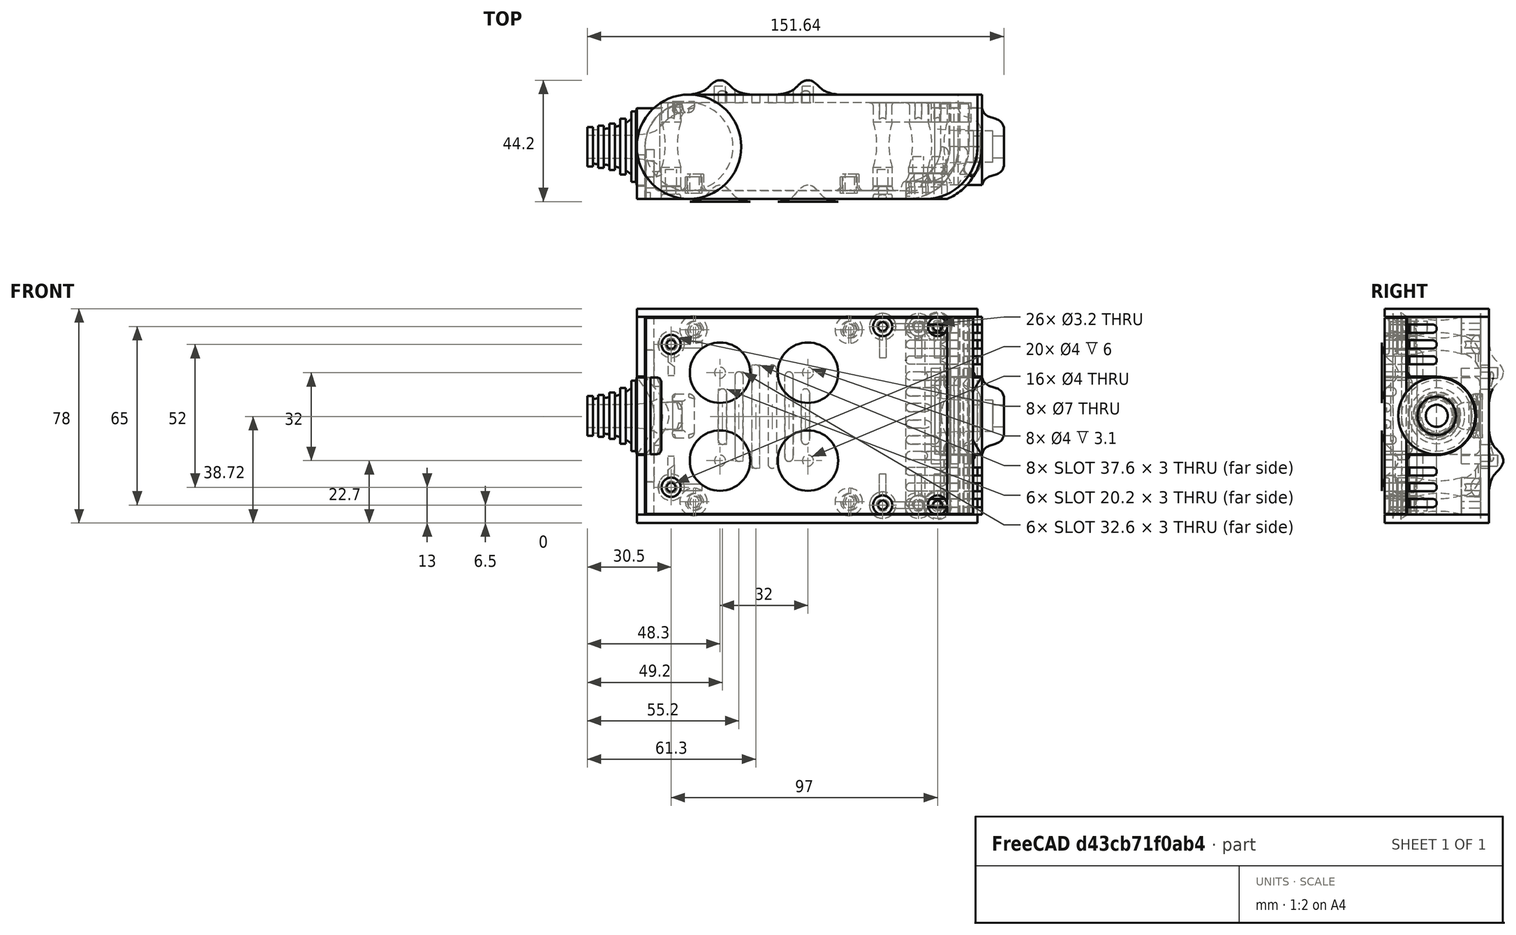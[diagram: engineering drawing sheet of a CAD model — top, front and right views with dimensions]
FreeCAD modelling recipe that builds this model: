
FCSTD DOCUMENT  (FreeCAD 0.19R0.19.2)
Label: enclosure_162
License: All rights reserved
LicenseURL: http://en.wikipedia.org/wiki/All_rights_reserved
objects: Part::Feature×140, Part::Revolution×140, Part::MultiFuse×121, Sketcher::SketchObject×67, Part::Extrusion×52, Part::Fillet×51, Part::Cut×51, Part::Cylinder×50, Part::Box×33, App::MeasureDistance×4
note: 705 computed .brp shape members not serialized (recipe doc carries the construction recipe); baked Part::Feature solids carry a one-line shape summary decoded from their .brp

FEATURE [Sketcher::SketchObject] Sketch  label="topSketch"
  FullyConstrained = true
  sketch-geometry (20):
    g0: LineSegment StartX=5.21097e-06 StartY=3 StartZ=0 EndX=5.21097e-06 EndY=19 EndZ=0
    g1: ArcOfCircle CenterX=19 CenterY=19 CenterZ=0 NormalX=0 NormalY=0 NormalZ=1 AngleXU=0 Radius=19 StartAngle=1.5708 EndAngle=3.14159
    g2: ArcOfCircle CenterX=19 CenterY=19 CenterZ=0 NormalX=0 NormalY=0 NormalZ=1 AngleXU=0 Radius=16 StartAngle=1.5708 EndAngle=3.14159
    g3: LineSegment StartX=114 StartY=35 StartZ=0 EndX=19 EndY=35 EndZ=0
    g4: LineSegment StartX=5.21097e-06 StartY=3 StartZ=0 EndX=5.21097e-06 EndY=0 EndZ=0
    g5: LineSegment StartX=3 StartY=0 StartZ=0 EndX=5.21097e-06 EndY=0 EndZ=0
    g6: LineSegment StartX=3 StartY=19 StartZ=0 EndX=3 EndY=0 EndZ=0
    g7: LineSegment StartX=19 StartY=38 StartZ=0 EndX=124 EndY=38 EndZ=0
    g8: Circle CenterX=119 CenterY=35 CenterZ=0 NormalX=0 NormalY=0 NormalZ=1 AngleXU=0 Radius=1
    g9: Circle CenterX=121 CenterY=35 CenterZ=0 NormalX=0 NormalY=0 NormalZ=1 AngleXU=0 Radius=1
    g10: Circle CenterX=121 CenterY=33 CenterZ=0 NormalX=0 NormalY=0 NormalZ=1 AngleXU=0 Radius=1
    g11: BSplineCurve PolesCount=3 KnotsCount=2 Degree=2 IsPeriodic=0
    g12: GeomPoint X=119 Y=35 Z=0
    g13: GeomPoint X=121 Y=33 Z=0
    g14: LineSegment StartX=119 StartY=35 StartZ=0 EndX=114 EndY=35 EndZ=0
    g15: ArcOfCircle CenterX=105 CenterY=19 CenterZ=0 NormalX=0 NormalY=0 NormalZ=1 AngleXU=0 Radius=19 StartAngle=5.7297 EndAngle=6.28319
    g16: ArcOfCircle CenterX=105 CenterY=19 CenterZ=0 NormalX=0 NormalY=0 NormalZ=1 AngleXU=0 Radius=16 StartAngle=5.60905 EndAngle=6.28319
    g17: LineSegment StartX=121 StartY=33 StartZ=0 EndX=121 EndY=19 EndZ=0
    g18: LineSegment StartX=124 StartY=38 StartZ=0 EndX=124 EndY=19 EndZ=0
    g19: LineSegment StartX=117.5 StartY=9.01251 StartZ=0 EndX=121.163 EndY=9.0125 EndZ=0
  constraints (46):
    c: Vertical(g0)
    c: Block(g0)
    c: Coincident(g1,g0)
    c: Block(g1)
    c: Coincident(g2,g1)
    c: Block(g2)
    c: Coincident(g3,g2)
    c: Horizontal(g3)
    c: Tangent(g3,g2)
    c: Coincident(g4,g0)
    c: Distance(g4) = 3
    c: Vertical(g4)
    c: Coincident(g5,g4)
    c: Horizontal(g5)
    c: Coincident(g6,g2)
    c: Coincident(g6,g5)
    c: Vertical(g6)
    c: Horizontal(g7)
    c: Distance(g7) = 105
    c: Coincident(g7,g1)
    c: Block(g3)
    c: Weight(g8) = 1
    c: Equal(g8,g9)
    c: Equal(g8,g10)
    c: InternalAlignment(g8,g11)
    c: InternalAlignment(g9,g11)
    c: InternalAlignment(g10,g11)
    c: InternalAlignment(g12,g11)
    c: InternalAlignment(g13,g11)
    c: Block(g11)
    c: Coincident(g14,g11)
    c: Coincident(g14,g3)
    c: Horizontal(g14)
    c: Block(g15)
    c: Coincident(g16,g15)
    c: Block(g16)
    c: Coincident(g17,g11)
    c: Coincident(g17,g16)
    c: Vertical(g17)
    c: Distance(g17) = 14
    c: Coincident(g18,g7)
    c: Coincident(g18,g15)
    c: Vertical(g18)
    c: Distance(g18) = 19
    c: Coincident(g19,g16)
    c: Coincident(g19,g15)
FEATURE [Sketcher::SketchObject] Sketch001  label="bottomSketch"
  FullyConstrained = true
  sketch-geometry (32):
    g0: LineSegment StartX=3.3 StartY=-6.03275e-07 StartZ=0 EndX=98 EndY=-6.03275e-07 EndZ=0
    g1: ArcOfCircle CenterX=98 CenterY=19 CenterZ=0 NormalX=0 NormalY=0 NormalZ=1 AngleXU=0 Radius=19 StartAngle=4.71239 EndAngle=5.71103
    g2: LineSegment StartX=6.3 StartY=8 StartZ=0 EndX=3.3 EndY=8 EndZ=0
    g3: LineSegment StartX=3.3 StartY=8 StartZ=0 EndX=3.3 EndY=-6.03275e-07 EndZ=0
    g4: ArcOfCircle CenterX=8.3 CenterY=5 CenterZ=0 NormalX=0 NormalY=0 NormalZ=1 AngleXU=0 Radius=2 StartAngle=3.14159 EndAngle=4.71239
    g5: LineSegment StartX=6.3 StartY=8 StartZ=0 EndX=6.3 EndY=5 EndZ=0
    g6: ArcOfCircle CenterX=98 CenterY=19 CenterZ=0 NormalX=0 NormalY=0 NormalZ=1 AngleXU=0 Radius=12.7 StartAngle=4.71239 EndAngle=6.28319
    g7: LineSegment StartX=94.7 StartY=3 StartZ=0 EndX=8.3 EndY=3 EndZ=0
    g8-g12: Circle x5 (B-spline internal-alignment scaffolding for g13; pole/knot coordinates omitted)
    g13: BSplineCurve PolesCount=5 KnotsCount=3 Degree=3 IsPeriodic=0
    g14: GeomPoint X=98 Y=6.3 Z=0
    g15: GeomPoint X=96.3938 Y=4.71946 Z=0
    g16: GeomPoint X=94.7 Y=3 Z=0
    g17-g23: Circle x7 (B-spline internal-alignment scaffolding for g24; pole/knot coordinates omitted)
    g24: BSplineCurve PolesCount=7 KnotsCount=5 Degree=3 IsPeriodic=0
    g25-g29: GeomPoint x5 (B-spline internal-alignment scaffolding for g24; pole/knot coordinates omitted)
    g30: ArcOfCircle CenterX=98 CenterY=19 CenterZ=0 NormalX=0 NormalY=0 NormalZ=1 AngleXU=0 Radius=15.7 StartAngle=5.81226 EndAngle=6.28319
    g31: LineSegment StartX=110.7 StartY=19 StartZ=0 EndX=113.7 EndY=19 EndZ=0
  constraints (41):
    c: Horizontal(g0)
    c: Coincident(g1,g0)
    c: Block(g1)
    c: Horizontal(g2)
    c: Distance(g2) = 3
    c: Coincident(g3,g2)
    c: Vertical(g3)
    c: Coincident(g3,g0)
    c: Block(g4)
    c: Block(g2)
    c: Coincident(g5,g2)
    c: Coincident(g5,g4)
    c: Vertical(g5)
    c: Coincident(g6,g1)
    c: Block(g6)
    c: Coincident(g7,g4)
    c: Horizontal(g7)
    c: Block(g0)
    c: Block(g7)
    c: Block(g3)
    c: Coincident(g13,g6)
    c: Weight(g8) = 1
    c: Equal(g8, g9-g12) x4
    c: Coincident(g13,g7)
    c: InternalAlignment(g8-g12 -> g13) x5
    c: InternalAlignment(g14,g13)
    c: InternalAlignment(g15,g13)
    c: InternalAlignment(g16,g13)
    c: Block(g13)
    c: Weight(g17) = 1
    c: Equal(g17, g18-g23) x6
    c: Coincident(g24,g1)
    c: InternalAlignment(g17-g23 -> g24) x7
    c: InternalAlignment(g25-g29 -> g24) x5
    c: Block(g24)
    c: Coincident(g30,g24)
    c: Coincident(g31,g6)
    c: Coincident(g31,g30)
    c: Horizontal(g31)
    c: Block(g31)
    c: Block(g30)
FEATURE [Part::Extrusion] Extrude  label="top"
  Base = -> Sketch
  Dir = (0,0,1)
  DirMode = 2
  FaceMakerClass = Part::FaceMakerBullseye
  LengthFwd = 72
  LengthRev = 0
  Solid = true
  Symmetric = false
FEATURE [Part::Extrusion] Extrude001  label="bottom"
  Base = -> Sketch001
  Dir = (0,0,1)
  DirMode = 2
  FaceMakerClass = Part::FaceMakerBullseye
  LengthFwd = 71.4
  LengthRev = 0
  Placement = pos=(0,0,0.3) rot=(0,0,1;0rad)
  Solid = true
  Symmetric = false
FEATURE [Sketcher::SketchObject] Sketch002  label="topSketch001"
  FullyConstrained = true
  sketch-geometry (6):
    g0: ArcOfCircle CenterX=19 CenterY=19 CenterZ=0 NormalX=0 NormalY=0 NormalZ=1 AngleXU=0 Radius=19 StartAngle=1.5708 EndAngle=3.14159
    g1: LineSegment StartX=5.22862e-06 StartY=19 StartZ=0 EndX=5.22862e-06 EndY=1.19904e-11 EndZ=0
    g2: LineSegment StartX=19 StartY=38 StartZ=0 EndX=124 EndY=38 EndZ=0
    g3: LineSegment StartX=5.22862e-06 StartY=1.19904e-11 StartZ=0 EndX=105 EndY=1.19904e-11 EndZ=0
    g4: ArcOfCircle CenterX=105 CenterY=19 CenterZ=0 NormalX=0 NormalY=0 NormalZ=1 AngleXU=0 Radius=19 StartAngle=4.71239 EndAngle=6.28319
    g5: LineSegment StartX=124 StartY=38 StartZ=0 EndX=124 EndY=19 EndZ=0
  constraints (16):
    c: Block(g0)
    c: Coincident(g1,g0)
    c: Vertical(g1)
    c: Horizontal(g2)
    c: Distance(g2) = 105
    c: Coincident(g2,g0)
    c: Distance(g1) = 19
    c: Coincident(g3,g1)
    c: Horizontal(g3)
    c: Distance(g3) = 105
    c: Block(g4)
    c: Coincident(g4,g3)
    c: Coincident(g5,g2)
    c: Coincident(g5,g4)
    c: Vertical(g5)
    c: Distance(g5) = 19
FEATURE [Part::Extrusion] Extrude002  label="sideA"
  Base = -> Sketch002
  Dir = (0,0,1)
  DirMode = 2
  FaceMakerClass = Part::FaceMakerBullseye
  LengthFwd = 3
  LengthRev = 0
  Placement = pos=(0,0,-3) rot=(0,0,1;0rad)
  Solid = true
  Symmetric = false
FEATURE [Sketcher::SketchObject] Sketch003  label="topSketch002"
  FullyConstrained = true
  sketch-geometry (6):
    g0: LineSegment StartX=19 StartY=38 StartZ=0 EndX=117 EndY=38 EndZ=0
    g1: ArcOfCircle CenterX=19 CenterY=19 CenterZ=0 NormalX=0 NormalY=0 NormalZ=1 AngleXU=0 Radius=19 StartAngle=1.5708 EndAngle=3.14159
    g2: LineSegment StartX=117 StartY=38 StartZ=0 EndX=117 EndY=19 EndZ=0
    g3: LineSegment StartX=98 StartY=1.0161e-12 StartZ=0 EndX=5.22862e-06 EndY=1.0161e-12 EndZ=0
    g4: LineSegment StartX=5.22862e-06 StartY=19 StartZ=0 EndX=5.22862e-06 EndY=1.0161e-12 EndZ=0
    g5: ArcOfCircle CenterX=98 CenterY=19 CenterZ=0 NormalX=0 NormalY=0 NormalZ=1 AngleXU=0 Radius=19 StartAngle=4.71239 EndAngle=6.28319
  constraints (16):
    c: Horizontal(g0)
    c: Distance(g0) = 98
    c: Coincident(g1,g0)
    c: Block(g1)
    c: Coincident(g2,g0)
    c: Vertical(g2)
    c: Distance(g2) = 19
    c: Horizontal(g3)
    c: Coincident(g4,g1)
    c: Vertical(g4)
    c: Coincident(g3,g4)
    c: Block(g3)
    c: Coincident(g5,g2)
    c: Coincident(g5,g3)
    c: Block(g0)
    c: Block(g5)
FEATURE [Sketcher::SketchObject] Sketch004
  FullyConstrained = true
  MapMode = 3
  Placement = pos=(0,0,0) rot=(1,0,0;1.5708rad)
  Support = -> [Extrude]
  sketch-geometry (8):
    g0: Circle CenterX=80.351 CenterY=-67.6202 CenterZ=0 NormalX=0 NormalY=0 NormalZ=1 AngleXU=0 Radius=2
    g1: Circle CenterX=80.351 CenterY=-67.6202 CenterZ=0 NormalX=0 NormalY=0 NormalZ=1 AngleXU=0 Radius=3
    g2: Circle CenterX=80.351 CenterY=-4.92017 CenterZ=0 NormalX=0 NormalY=0 NormalZ=1 AngleXU=0 Radius=2
    g3: Circle CenterX=80.351 CenterY=-4.92017 CenterZ=0 NormalX=0 NormalY=0 NormalZ=1 AngleXU=0 Radius=3
    g4: Circle CenterX=23.851 CenterY=-4.92017 CenterZ=0 NormalX=0 NormalY=0 NormalZ=1 AngleXU=0 Radius=2
    g5: Circle CenterX=23.851 CenterY=-4.92017 CenterZ=0 NormalX=0 NormalY=0 NormalZ=1 AngleXU=0 Radius=3
    g6: Circle CenterX=23.851 CenterY=-67.6202 CenterZ=0 NormalX=0 NormalY=0 NormalZ=1 AngleXU=0 Radius=2
    g7: Circle CenterX=23.851 CenterY=-67.6202 CenterZ=0 NormalX=0 NormalY=0 NormalZ=1 AngleXU=0 Radius=3
  constraints (8):
    c: Block(g3)
    c: Block(g2)
    c: Block(g1)
    c: Block(g0)
    c: Block(g6)
    c: Block(g7)
    c: Block(g4)
    c: Block(g5)
FEATURE [Part::Extrusion] Extrude004
  Base = -> Sketch004
  Dir = (0,-1,2e-16)
  DirMode = 2
  FaceMakerClass = Part::FaceMakerBullseye
  LengthFwd = 6
  LengthRev = 0
  Placement = pos=(0,9,0) rot=(0,0,1;0rad)
  Solid = true
  Symmetric = false
FEATURE [Sketcher::SketchObject] Sketch005
  FullyConstrained = true
  MapMode = 3
  Placement = pos=(0,0,0) rot=(1,0,0;1.5708rad)
  Support = -> [Extrude]
  sketch-geometry (8):
    g0: Circle CenterX=80.351 CenterY=-67.6202 CenterZ=0 NormalX=0 NormalY=0 NormalZ=1 AngleXU=0 Radius=3
    g1: Circle CenterX=80.351 CenterY=-4.92017 CenterZ=0 NormalX=0 NormalY=0 NormalZ=1 AngleXU=0 Radius=3
    g2: Circle CenterX=23.851 CenterY=-4.92017 CenterZ=0 NormalX=0 NormalY=0 NormalZ=1 AngleXU=0 Radius=3
    g3: Circle CenterX=23.851 CenterY=-67.6202 CenterZ=0 NormalX=0 NormalY=0 NormalZ=1 AngleXU=0 Radius=3
    g4: Circle CenterX=23.851 CenterY=-67.6202 CenterZ=0 NormalX=0 NormalY=0 NormalZ=1 AngleXU=0 Radius=5
    g5: Circle CenterX=80.351 CenterY=-67.6202 CenterZ=0 NormalX=0 NormalY=0 NormalZ=1 AngleXU=0 Radius=5
    g6: Circle CenterX=23.851 CenterY=-4.92017 CenterZ=0 NormalX=0 NormalY=0 NormalZ=1 AngleXU=0 Radius=5
    g7: Circle CenterX=80.351 CenterY=-4.92017 CenterZ=0 NormalX=0 NormalY=0 NormalZ=1 AngleXU=0 Radius=5
  constraints (8):
    c: Block(g1)
    c: Block(g0)
    c: Block(g3)
    c: Block(g2)
    c: Block(g5)
    c: Block(g4)
    c: Block(g6)
    c: Block(g7)
FEATURE [Part::Extrusion] Extrude005
  Base = -> Sketch005
  Dir = (0,-1,2e-16)
  DirMode = 2
  FaceMakerClass = Part::FaceMakerBullseye
  LengthFwd = 2
  LengthRev = 0
  Solid = true
  Symmetric = false
FEATURE [Sketcher::SketchObject] Sketch006
  FullyConstrained = true
  MapMode = 3
  Placement = pos=(0,0,0) rot=(1,0,0;1.5708rad)
  sketch-geometry (8):
    g0: Circle CenterX=80.351 CenterY=-67.6202 CenterZ=0 NormalX=0 NormalY=0 NormalZ=1 AngleXU=0 Radius=3
    g1: Circle CenterX=80.351 CenterY=-4.92017 CenterZ=0 NormalX=0 NormalY=0 NormalZ=1 AngleXU=0 Radius=3
    g2: Circle CenterX=23.851 CenterY=-4.92017 CenterZ=0 NormalX=0 NormalY=0 NormalZ=1 AngleXU=0 Radius=3
    g3: Circle CenterX=23.851 CenterY=-67.6202 CenterZ=0 NormalX=0 NormalY=0 NormalZ=1 AngleXU=0 Radius=3
    g4: Circle CenterX=23.851 CenterY=-67.6202 CenterZ=0 NormalX=0 NormalY=0 NormalZ=1 AngleXU=0 Radius=5
    g5: Circle CenterX=80.351 CenterY=-67.6202 CenterZ=0 NormalX=0 NormalY=0 NormalZ=1 AngleXU=0 Radius=5
    g6: Circle CenterX=23.851 CenterY=-4.92017 CenterZ=0 NormalX=0 NormalY=0 NormalZ=1 AngleXU=0 Radius=5
    g7: Circle CenterX=80.351 CenterY=-4.92017 CenterZ=0 NormalX=0 NormalY=0 NormalZ=1 AngleXU=0 Radius=5
  constraints (8):
    c: Block(g1)
    c: Block(g0)
    c: Block(g3)
    c: Block(g2)
    c: Block(g5)
    c: Block(g4)
    c: Block(g6)
    c: Block(g7)
FEATURE [Part::Extrusion] Extrude007
  Base = -> Sketch006
  Dir = (0,-1,2e-16)
  DirMode = 2
  FaceMakerClass = Part::FaceMakerBullseye
  LengthFwd = 2
  LengthRev = 0
  Solid = true
  Symmetric = false
FEATURE [Part::Fillet] Fillet
  Base = -> Extrude007
  Edges = 4 edges r=1.99: [Edge6,Edge12,Edge18,Edge24]
FEATURE [Part::Cut] Cut
  Base = -> Extrude005
  Placement = pos=(0,5,0) rot=(0,0,1;0rad)
  Tool = -> Fillet
FEATURE [Part::MultiFuse] Fusion  label="pCBScrews"
  Placement = pos=(-2.5,0,72.3) rot=(0,0,1;0rad)
  Shapes = -> [Extrude004,Cut]
FEATURE [App::MeasureDistance] Distance  label="Distance: 0.69 mm"
  Distance = 0.685967
  P1 = (24.0138,2.9647,0.3)
  P2 = (23.8901,3,-0.373787)
FEATURE [App::MeasureDistance] Distance001  label="Distance: 0.53 mm"
  Distance = 0.533607
  P1 = (80.2939,3,72.2334)
  P2 = (80.281,2.99661,71.7)
FEATURE [Part::Fillet] Fillet001
  Base = -> Extrude001
  Edges = 1 edges r=2.4: [Edge17]
FEATURE [Part::Fillet] Fillet002  label="bottom001"
  Base = -> Fillet001
  Edges = 1 edges r=2.4: [Edge36]
FEATURE [Part::Fillet] Fillet003  label="top001"
  Base = -> Extrude
  Edges = 1 edges r=2: [Edge1]
FEATURE [Sketcher::SketchObject] Sketch007
  FullyConstrained = true
  sketch-geometry (16):
    g0: LineSegment StartX=4 StartY=0 StartZ=0 EndX=4 EndY=2.4 EndZ=0
    g1: LineSegment StartX=4 StartY=2.4 StartZ=0 EndX=7 EndY=2.4 EndZ=0
    g2: LineSegment StartX=4 StartY=0 StartZ=0 EndX=5.7 EndY=0 EndZ=0
    g3: LineSegment StartX=5.7 StartY=0 StartZ=0 EndX=5.7 EndY=-5.6 EndZ=0
    g4-g8: Circle x5 (B-spline internal-alignment scaffolding for g9; pole/knot coordinates omitted)
    g9: BSplineCurve PolesCount=5 KnotsCount=3 Degree=3 IsPeriodic=0
    g10: GeomPoint X=7 Y=2.4 Z=0
    g11: GeomPoint X=10.4582 Y=-1.55472 Z=0
    g12: GeomPoint X=14 Y=-5.6 Z=0
    g13: LineSegment StartX=14 StartY=-5.6 StartZ=0 EndX=14 EndY=-14.1 EndZ=0
    g14: LineSegment StartX=14 StartY=-14.1 StartZ=0 EndX=6.5 EndY=-14.1 EndZ=0
    g15: LineSegment StartX=5.7 StartY=-5.6 StartZ=0 EndX=6.5 EndY=-14.1 EndZ=0
  constraints (28):
    c: Distance(g0) = 2.4
    c: Vertical(g0)
    c: Block(g0)
    c: Coincident(g1,g0)
    c: Horizontal(g1)
    c: Distance(g1) = 3
    c: Coincident(g2,g0)
    c: Horizontal(g2)
    c: Distance(g2) = 1.7
    c: Coincident(g3,g2)
    c: Vertical(g3)
    c: Distance(g3) = 5.6
    c: Coincident(g9,g1)
    c: Weight(g4) = 1
    c: Equal(g4, g5-g8) x4
    c: InternalAlignment(g4-g8 -> g9) x5
    c: InternalAlignment(g10,g9)
    c: InternalAlignment(g11,g9)
    c: InternalAlignment(g12,g9)
    c: Block(g9)
    c: Coincident(g13,g9)
    c: Vertical(g13)
    c: Distance(g13) = 8.5
    c: Coincident(g14,g13)
    c: Horizontal(g14)
    c: Distance(g14) = 7.5
    c: Coincident(g15,g3)
    c: Coincident(g15,g14)
FEATURE [Part::Feature] Face
  shape: bbox 10 x 16.5 x 2e-07 mm, 1 faces, 0 solids (baked)
FEATURE [Part::Revolution] Revolve  label="plugHousing"
  Angle = 360
  Axis = (0,1,0)
  Base = (0,0,0)
  FaceMakerClass = Part::FaceMakerBullseye
  Placement = pos=(0,0,36.15) rot=(0,0,1;0rad)
  Solid = false
  Source = -> Face
  Symmetric = false
FEATURE [Part::Feature] Face001
  shape: bbox 10 x 16.5 x 2e-07 mm, 1 faces, 0 solids (baked)
FEATURE [Part::Revolution] Revolve001  label="plugHousing001"
  Angle = 360
  Axis = (0,1,0)
  Base = (0,0,0)
  FaceMakerClass = Part::FaceMakerBullseye
  Placement = pos=(0,0,36.15) rot=(0,0,1;0rad)
  Solid = false
  Source = -> Face001
  Symmetric = false
FEATURE [Part::MultiFuse] Fusion001  label="plugHousing002"
  Placement = pos=(0,0,0) rot=(0,0,1;1.5708rad)
  Shapes = -> [Revolve001,Revolve]
FEATURE [Part::Feature] Face002
  shape: bbox 10 x 16.5 x 2e-07 mm, 1 faces, 0 solids (baked)
FEATURE [Part::Revolution] Revolve003  label="plugHousing005"
  Angle = 360
  Axis = (0,1,0)
  Base = (0,0,0)
  FaceMakerClass = Part::FaceMakerBullseye
  Placement = pos=(0,0,36.15) rot=(0,0,1;0rad)
  Solid = false
  Source = -> Face002
  Symmetric = false
FEATURE [Part::Feature] Face003
  shape: bbox 10 x 16.5 x 2e-07 mm, 1 faces, 0 solids (baked)
FEATURE [Part::Revolution] Revolve002  label="plugHousing003"
  Angle = 360
  Axis = (0,1,0)
  Base = (0,0,0)
  FaceMakerClass = Part::FaceMakerBullseye
  Placement = pos=(0,0,36.15) rot=(0,0,1;0rad)
  Solid = false
  Source = -> Face003
  Symmetric = false
FEATURE [Part::MultiFuse] Fusion002  label="plugHousing004"
  Placement = pos=(0,0,0) rot=(0,0,1;1.5708rad)
  Shapes = -> [Revolve002,Revolve003]
FEATURE [Part::MultiFuse] Fusion003  label="plugHousing006"
  Placement = pos=(0,19,0) rot=(0,0,1;3.14159rad)
  Shapes = -> [Fusion002,Fusion001]
FEATURE [Part::Feature] Face004
  shape: bbox 10 x 16.5 x 2e-07 mm, 1 faces, 0 solids (baked)
FEATURE [Part::Revolution] Revolve006  label="plugHousing010"
  Angle = 360
  Axis = (0,1,0)
  Base = (0,0,0)
  FaceMakerClass = Part::FaceMakerBullseye
  Placement = pos=(0,0,36.15) rot=(0,0,1;0rad)
  Solid = false
  Source = -> Face004
  Symmetric = false
FEATURE [Part::Feature] Face005
  shape: bbox 10 x 16.5 x 2e-07 mm, 1 faces, 0 solids (baked)
FEATURE [Part::Revolution] Revolve007  label="plugHousing011"
  Angle = 360
  Axis = (0,1,0)
  Base = (0,0,0)
  FaceMakerClass = Part::FaceMakerBullseye
  Placement = pos=(0,0,36.15) rot=(0,0,1;0rad)
  Solid = false
  Source = -> Face005
  Symmetric = false
FEATURE [Part::Feature] Face006
  shape: bbox 10 x 16.5 x 2e-07 mm, 1 faces, 0 solids (baked)
FEATURE [Part::Revolution] Revolve004  label="plugHousing007"
  Angle = 360
  Axis = (0,1,0)
  Base = (0,0,0)
  FaceMakerClass = Part::FaceMakerBullseye
  Placement = pos=(0,0,36.15) rot=(0,0,1;0rad)
  Solid = false
  Source = -> Face006
  Symmetric = false
FEATURE [Part::MultiFuse] Fusion004  label="plugHousing009"
  Placement = pos=(0,0,0) rot=(0,0,1;1.5708rad)
  Shapes = -> [Revolve004,Revolve007]
FEATURE [Part::Feature] Face007
  shape: bbox 10 x 16.5 x 2e-07 mm, 1 faces, 0 solids (baked)
FEATURE [Part::Revolution] Revolve005  label="plugHousing008"
  Angle = 360
  Axis = (0,1,0)
  Base = (0,0,0)
  FaceMakerClass = Part::FaceMakerBullseye
  Placement = pos=(0,0,36.15) rot=(0,0,1;0rad)
  Solid = false
  Source = -> Face007
  Symmetric = false
FEATURE [Part::MultiFuse] Fusion005  label="plugHousing012"
  Placement = pos=(0,0,0) rot=(0,0,1;1.5708rad)
  Shapes = -> [Revolve006,Revolve005]
FEATURE [Part::MultiFuse] Fusion006  label="plugHousing013"
  Placement = pos=(0,19,0) rot=(0,0,1;3.14159rad)
  Shapes = -> [Fusion005,Fusion004]
FEATURE [Part::MultiFuse] Fusion007  label="plugHousing014"
  Placement = pos=(122.621,0,-0.15) rot=(0,0,1;0rad)
  Shapes = -> [Fusion003,Fusion006]
FEATURE [Part::Cylinder] Cylinder002
  Angle = 360
  AttacherType = Attacher::AttachEngine3D
  Height = 20
  Placement = pos=(0,0,36.15) rot=(0,0,1;0rad)
  Radius = 4
FEATURE [Part::Cylinder] Cylinder003
  Angle = 360
  AttacherType = Attacher::AttachEngine3D
  Height = 10
  Placement = pos=(0,0,36.15) rot=(0,0,1;0rad)
  Radius = 4
FEATURE [Part::MultiFuse] Fusion009  label="removeToCreateHoleForPlugHousing"
  Placement = pos=(70,19,36.15) rot=(0,1,0;1.5708rad)
  Shapes = -> [Cylinder002,Cylinder003]
FEATURE [Part::Cylinder] Cylinder004
  Angle = 360
  AttacherType = Attacher::AttachEngine3D
  Height = 20
  Placement = pos=(0,0,36.15) rot=(0,0,1;0rad)
  Radius = 4
FEATURE [Part::Cylinder] Cylinder005
  Angle = 360
  AttacherType = Attacher::AttachEngine3D
  Height = 10
  Placement = pos=(0,0,36.15) rot=(0,0,1;0rad)
  Radius = 4
FEATURE [Part::MultiFuse] Fusion010  label="removeToCreateHoleForPlugHousing001"
  Placement = pos=(70,19,36.15) rot=(0,1,0;1.5708rad)
  Shapes = -> [Cylinder004,Cylinder005]
FEATURE [Part::Cut] Cut001
  Base = -> Fillet003
  Tool = -> Fusion010
FEATURE [Part::Cut] Cut002  label="Bottom"
  Base = -> Fillet002
  Tool = -> Fusion009
FEATURE [Part::Feature] Face008
  shape: bbox 10 x 16.5 x 2e-07 mm, 1 faces, 0 solids (baked)
FEATURE [Part::Revolution] Revolve011  label="plugHousing021"
  Angle = 360
  Axis = (0,1,0)
  Base = (0,0,0)
  FaceMakerClass = Part::FaceMakerBullseye
  Placement = pos=(0,0,36.15) rot=(0,0,1;0rad)
  Solid = false
  Source = -> Face008
  Symmetric = false
FEATURE [Part::Feature] Face009
  shape: bbox 10 x 16.5 x 2e-07 mm, 1 faces, 0 solids (baked)
FEATURE [Part::Revolution] Revolve012  label="plugHousing022"
  Angle = 360
  Axis = (0,1,0)
  Base = (0,0,0)
  FaceMakerClass = Part::FaceMakerBullseye
  Placement = pos=(0,0,36.15) rot=(0,0,1;0rad)
  Solid = false
  Source = -> Face009
  Symmetric = false
FEATURE [Part::Feature] Face010 .. Face013  x4 (patterned run collapsed; names and placements below)
  shape: bbox 10 x 16.5 x 2e-07 mm, 1 faces, 0 solids (baked)
FEATURE [Part::Revolution] Revolve015  label="plugHousing027"
  Angle = 360
  Axis = (0,1,0)
  Base = (0,0,0)
  FaceMakerClass = Part::FaceMakerBullseye
  Placement = pos=(0,0,36.15) rot=(0,0,1;0rad)
  Solid = false
  Source = -> Face013
  Symmetric = false
FEATURE [Part::Feature] Face014
  shape: bbox 10 x 16.5 x 2e-07 mm, 1 faces, 0 solids (baked)
FEATURE [Part::Feature] Face015
  shape: bbox 10 x 16.5 x 2e-07 mm, 1 faces, 0 solids (baked)
FEATURE [Part::Feature] Face016
  shape: bbox 10 x 16.5 x 2e-07 mm, 1 faces, 0 solids (baked)
FEATURE [Part::Revolution] Revolve019  label="plugHousing033"
  Angle = 360
  Axis = (0,1,0)
  Base = (0,0,0)
  FaceMakerClass = Part::FaceMakerBullseye
  Placement = pos=(0,0,36.15) rot=(0,0,1;0rad)
  Solid = false
  Source = -> Face016
  Symmetric = false
FEATURE [Part::Feature] Face017
  shape: bbox 10 x 16.5 x 2e-07 mm, 1 faces, 0 solids (baked)
FEATURE [Part::Revolution] Revolve020  label="plugHousing034"
  Angle = 360
  Axis = (0,1,0)
  Base = (0,0,0)
  FaceMakerClass = Part::FaceMakerBullseye
  Placement = pos=(0,0,36.15) rot=(0,0,1;0rad)
  Solid = false
  Source = -> Face017
  Symmetric = false
FEATURE [Part::Feature] Face018
  shape: bbox 10 x 16.5 x 2e-07 mm, 1 faces, 0 solids (baked)
FEATURE [Part::Revolution] Revolve016  label="plugHousing030"
  Angle = 360
  Axis = (0,1,0)
  Base = (0,0,0)
  FaceMakerClass = Part::FaceMakerBullseye
  Placement = pos=(0,0,36.15) rot=(0,0,1;0rad)
  Solid = false
  Source = -> Face018
  Symmetric = false
FEATURE [Part::MultiFuse] Fusion020  label="plugHousing038"
  Placement = pos=(0,0,0) rot=(0,0,1;1.5708rad)
  Shapes = -> [Revolve016,Revolve020]
FEATURE [Part::Feature] Face019
  shape: bbox 10 x 16.5 x 2e-07 mm, 1 faces, 0 solids (baked)
FEATURE [Part::Feature] Face020
  shape: bbox 10 x 16.5 x 2e-07 mm, 1 faces, 0 solids (baked)
FEATURE [Part::Revolution] Revolve017  label="plugHousing031"
  Angle = 360
  Axis = (0,1,0)
  Base = (0,0,0)
  FaceMakerClass = Part::FaceMakerBullseye
  Placement = pos=(0,0,36.15) rot=(0,0,1;0rad)
  Solid = false
  Source = -> Face020
  Symmetric = false
FEATURE [Part::MultiFuse] Fusion021  label="plugHousing039"
  Placement = pos=(0,0,0) rot=(0,0,1;1.5708rad)
  Shapes = -> [Revolve019,Revolve017]
FEATURE [Part::MultiFuse] Fusion023  label="plugHousing041"
  Placement = pos=(0,19,0) rot=(0,0,1;3.14159rad)
  Shapes = -> [Fusion021,Fusion020]
FEATURE [Part::Revolution] Revolve022  label="plugHousing043"
  Angle = 360
  Axis = (0,1,0)
  Base = (0,0,0)
  FaceMakerClass = Part::FaceMakerBullseye
  Placement = pos=(0,0,36.15) rot=(0,0,1;0rad)
  Solid = false
  Source = -> Face019
  Symmetric = false
FEATURE [Part::Feature] Face021
  shape: bbox 10 x 16.5 x 2e-07 mm, 1 faces, 0 solids (baked)
FEATURE [Part::Revolution] Revolve023  label="plugHousing044"
  Angle = 360
  Axis = (0,1,0)
  Base = (0,0,0)
  FaceMakerClass = Part::FaceMakerBullseye
  Placement = pos=(0,0,36.15) rot=(0,0,1;0rad)
  Solid = false
  Source = -> Face021
  Symmetric = false
FEATURE [Part::Feature] Face022
  shape: bbox 10 x 16.5 x 2e-07 mm, 1 faces, 0 solids (baked)
FEATURE [Part::Revolution] Revolve018  label="plugHousing032"
  Angle = 360
  Axis = (0,1,0)
  Base = (0,0,0)
  FaceMakerClass = Part::FaceMakerBullseye
  Placement = pos=(0,0,36.15) rot=(0,0,1;0rad)
  Solid = false
  Source = -> Face022
  Symmetric = false
FEATURE [Part::MultiFuse] Fusion022  label="plugHousing040"
  Placement = pos=(0,0,0) rot=(0,0,1;1.5708rad)
  Shapes = -> [Revolve018,Revolve023]
FEATURE [Part::Feature] Face023
  shape: bbox 10 x 16.5 x 2e-07 mm, 1 faces, 0 solids (baked)
FEATURE [Part::Revolution] Revolve021  label="plugHousing035"
  Angle = 360
  Axis = (0,1,0)
  Base = (0,0,0)
  FaceMakerClass = Part::FaceMakerBullseye
  Placement = pos=(0,0,36.15) rot=(0,0,1;0rad)
  Solid = false
  Source = -> Face023
  Symmetric = false
FEATURE [Part::MultiFuse] Fusion018  label="plugHousing036"
  Placement = pos=(0,0,0) rot=(0,0,1;1.5708rad)
  Shapes = -> [Revolve022,Revolve021]
FEATURE [Part::MultiFuse] Fusion019  label="plugHousing037"
  Placement = pos=(0,19,0) rot=(0,0,1;3.14159rad)
  Shapes = -> [Fusion018,Fusion022]
FEATURE [Part::MultiFuse] Fusion024  label="plugHousing042"
  Placement = pos=(122.621,0,-0.15) rot=(0,0,1;0rad)
  Shapes = -> [Fusion023,Fusion019]
FEATURE [Part::Cylinder] Cylinder006
  Angle = 360
  AttacherType = Attacher::AttachEngine3D
  Height = 20
  Placement = pos=(0,0,36.15) rot=(0,0,1;0rad)
  Radius = 14.3
FEATURE [Part::Cylinder] Cylinder007
  Angle = 360
  AttacherType = Attacher::AttachEngine3D
  Height = 10
  Placement = pos=(0,0,36.15) rot=(0,0,1;0rad)
  Radius = 4
FEATURE [Part::MultiFuse] Fusion026  label="removeToCreteHoleForPlugHousing"
  Placement = pos=(70,19,36) rot=(0,1,0;1.5708rad)
  Shapes = -> [Cylinder006,Cylinder007]
FEATURE [Part::Box] Box001  label="Cube001"
  AttacherType = Attacher::AttachEngine3D
  Height = 28
  Length = 3
  Placement = pos=(110.7,19,22) rot=(0,0,1;0rad)
  Width = 15.7
FEATURE [Part::Cut] Cut003  label="top002"
  Base = -> Cut001
  Tool = -> Fusion007
FEATURE [Part::Revolution] Revolve008  label="plugHousing015"
  Angle = 360
  Axis = (0,1,0)
  Base = (0,0,0)
  FaceMakerClass = Part::FaceMakerBullseye
  Placement = pos=(0,0,36.15) rot=(0,0,1;0rad)
  Solid = false
  Source = -> Face010
  Symmetric = false
FEATURE [Part::MultiFuse] Fusion013  label="plugHousing020"
  Placement = pos=(0,0,0) rot=(0,0,1;1.5708rad)
  Shapes = -> [Revolve008,Revolve012]
FEATURE [Part::Cut] Cut004  label="top003"
  Base = -> Cut003
  Placement = pos=(1,0,0) rot=(0,0,1;0rad)
  Tool = -> Fusion026
FEATURE [Part::Cylinder] Cylinder008
  Angle = 360
  AttacherType = Attacher::AttachEngine3D
  Height = 20
  Placement = pos=(0,0,36.15) rot=(0,0,1;0rad)
  Radius = 10.3
FEATURE [Part::Cylinder] Cylinder009
  Angle = 360
  AttacherType = Attacher::AttachEngine3D
  Height = 10
  Placement = pos=(0,0,36.15) rot=(0,0,1;0rad)
  Radius = 4
FEATURE [Part::MultiFuse] Fusion027  label="removeToCreteHoleForPlugHousing001"
  Placement = pos=(70,19,36) rot=(0,1,0;1.5708rad)
  Shapes = -> [Cylinder008,Cylinder009]
FEATURE [Part::Cut] Cut005  label="plugHousingTab"
  Base = -> Box001
  Tool = -> Fusion027
FEATURE [Part::MultiFuse] Fusion028  label="plugHousing045"
  Shapes = -> [Fusion024,Cut005]
FEATURE [Part::Box] Box002  label="Cube002"
  AttacherType = Attacher::AttachEngine3D
  Height = 28.8
  Length = 3
  Placement = pos=(107.3,28,21.6) rot=(0,0,1;0rad)
  Width = 7
FEATURE [Part::Box] Box003  label="Cube003"
  AttacherType = Attacher::AttachEngine3D
  Height = 3
  Length = 6.4
  Placement = pos=(107.3,28,18.6) rot=(0,0,1;0rad)
  Width = 7
FEATURE [Part::Box] Box004  label="Cube004"
  AttacherType = Attacher::AttachEngine3D
  Height = 3
  Length = 6.4
  Placement = pos=(107.3,28,50.4) rot=(0,0,1;0rad)
  Width = 7
FEATURE [Part::MultiFuse] Fusion029  label="plugHousingBracketHolder"
  Shapes = -> [Box004,Box002,Box003]
FEATURE [Part::Cylinder] Cylinder010
  Angle = 360
  AttacherType = Attacher::AttachEngine3D
  Height = 20
  Placement = pos=(0,0,36.15) rot=(0,0,1;0rad)
  Radius = 14.3
FEATURE [Part::Cylinder] Cylinder011
  Angle = 360
  AttacherType = Attacher::AttachEngine3D
  Height = 10
  Placement = pos=(0,0,36.15) rot=(0,0,1;0rad)
  Radius = 4
FEATURE [Part::MultiFuse] Fusion030  label="removeToCreteHoleForPlugHousing002"
  Placement = pos=(70,19,36) rot=(0,1,0;1.5708rad)
  Shapes = -> [Cylinder010,Cylinder011]
FEATURE [Part::Cut] Cut006  label="plugHousingBracketHolder001"
  Base = -> Fusion029
  Tool = -> Fusion030
FEATURE [Part::Cylinder] Cylinder012
  Angle = 360
  AttacherType = Attacher::AttachEngine3D
  Height = 20
  Placement = pos=(0,0,36.15) rot=(0,0,1;0rad)
  Radius = 7
FEATURE [Part::Cylinder] Cylinder013
  Angle = 360
  AttacherType = Attacher::AttachEngine3D
  Height = 10
  Placement = pos=(0,0,36.15) rot=(0,0,1;0rad)
  Radius = 4
FEATURE [Part::MultiFuse] Fusion032  label="removeToCreteHoleForPlugHousing003"
  Placement = pos=(70,19,36) rot=(0,1,0;1.5708rad)
  Shapes = -> [Cylinder012,Cylinder013]
FEATURE [Part::Cut] Cut007  label="bottom002"
  Base = -> Cut002
  Tool = -> Fusion032
FEATURE [Sketcher::SketchObject] Sketch008
  FullyConstrained = true
  sketch-geometry (54):
    g0: LineSegment StartX=-4.2 StartY=0 StartZ=0 EndX=-6.2 EndY=0 EndZ=0
    g1: LineSegment StartX=-14 StartY=-18 StartZ=0 EndX=-14 EndY=-26.5 EndZ=0
    g2: LineSegment StartX=-4.2 StartY=0 StartZ=0 EndX=-4.2 EndY=-13.4877 EndZ=0
    g3: Circle CenterX=-4.2 CenterY=-13.4877 CenterZ=0 NormalX=0 NormalY=0 NormalZ=1 AngleXU=0 Radius=1
    g4: Circle CenterX=-4.2 CenterY=-26.5 CenterZ=0 NormalX=0 NormalY=0 NormalZ=1 AngleXU=0 Radius=1
    g5: Circle CenterX=-8.2 CenterY=-26.5 CenterZ=0 NormalX=0 NormalY=0 NormalZ=1 AngleXU=0 Radius=1
    g6: BSplineCurve PolesCount=3 KnotsCount=2 Degree=2 IsPeriodic=0
    g7: GeomPoint X=-4.2 Y=-13.4877 Z=0
    g8: GeomPoint X=-8.2 Y=-26.5 Z=0
    g9: LineSegment StartX=-14 StartY=-26.5 StartZ=0 EndX=-8.2 EndY=-26.5 EndZ=0
    g10: LineSegment StartX=-10.15 StartY=-12 StartZ=0 EndX=-10.15 EndY=-14 EndZ=0
    g11: LineSegment StartX=-12.8401 StartY=-16 StartZ=0 EndX=-10.1571 EndY=-16 EndZ=0
    g12: LineSegment StartX=-10.15 StartY=-14 StartZ=0 EndX=-8.70761 EndY=-14 EndZ=0
    g13: LineSegment StartX=-12.8401 StartY=-16 StartZ=0 EndX=-12.8401 EndY=-17.6958 EndZ=0
    g14: LineSegment StartX=-10.15 StartY=-12 StartZ=0 EndX=-7.79258 EndY=-12 EndZ=0
    g15: Circle CenterX=-6.2215 CenterY=-2 CenterZ=0 NormalX=0 NormalY=0 NormalZ=1 AngleXU=0 Radius=1
    g16: Circle CenterX=-6.22762 CenterY=-2.58724 CenterZ=0 NormalX=0 NormalY=0 NormalZ=1 AngleXU=0 Radius=1
    g17: Circle CenterX=-6.32538 CenterY=-4 CenterZ=0 NormalX=0 NormalY=0 NormalZ=1 AngleXU=0 Radius=1
    g18: BSplineCurve PolesCount=3 KnotsCount=2 Degree=2 IsPeriodic=0
    g19: GeomPoint X=-6.2215 Y=-2 Z=0
    g20: GeomPoint X=-6.32538 Y=-4 Z=0
    g21: Circle CenterX=-6.48644 CenterY=-5.99526 CenterZ=0 NormalX=0 NormalY=0 NormalZ=1 AngleXU=0 Radius=1
    g22: Circle CenterX=-6.58486 CenterY=-6.99526 CenterZ=0 NormalX=0 NormalY=0 NormalZ=1 AngleXU=0 Radius=1
    g23: Circle CenterX=-6.77343 CenterY=-8 CenterZ=0 NormalX=0 NormalY=0 NormalZ=1 AngleXU=0 Radius=1
    g24: BSplineCurve PolesCount=3 KnotsCount=2 Degree=2 IsPeriodic=0
    g25: GeomPoint X=-6.48644 Y=-5.99526 Z=0
    g26: GeomPoint X=-6.77343 Y=-8 Z=0
    g27: Circle CenterX=-7.19003 CenterY=-10 CenterZ=0 NormalX=0 NormalY=0 NormalZ=1 AngleXU=0 Radius=1
    g28: Circle CenterX=-7.44407 CenterY=-11.0915 CenterZ=0 NormalX=0 NormalY=0 NormalZ=1 AngleXU=0 Radius=1
    g29: Circle CenterX=-7.79258 CenterY=-12 CenterZ=0 NormalX=0 NormalY=0 NormalZ=1 AngleXU=0 Radius=1
    g30: BSplineCurve PolesCount=3 KnotsCount=2 Degree=2 IsPeriodic=0
    g31: GeomPoint X=-7.19003 Y=-10 Z=0
    g32: GeomPoint X=-7.79258 Y=-12 Z=0
    g33: Circle CenterX=-8.70761 CenterY=-14 CenterZ=0 NormalX=0 NormalY=0 NormalZ=1 AngleXU=0 Radius=1
    g34: Circle CenterX=-9.33087 CenterY=-15.1837 CenterZ=0 NormalX=0 NormalY=0 NormalZ=1 AngleXU=0 Radius=1
    g35: Circle CenterX=-10.1571 CenterY=-16 CenterZ=0 NormalX=0 NormalY=0 NormalZ=1 AngleXU=0 Radius=1
    g36: BSplineCurve PolesCount=3 KnotsCount=2 Degree=2 IsPeriodic=0
    g37: GeomPoint X=-8.70761 Y=-14 Z=0
    g38: GeomPoint X=-10.1571 Y=-16 Z=0
    g39: Circle CenterX=-12.8401 CenterY=-17.6958 CenterZ=0 NormalX=0 NormalY=0 NormalZ=1 AngleXU=0 Radius=1
    g40: Circle CenterX=-13.3521 CenterY=-17.9027 CenterZ=0 NormalX=0 NormalY=0 NormalZ=1 AngleXU=0 Radius=1
    g41: Circle CenterX=-14 CenterY=-18 CenterZ=0 NormalX=0 NormalY=0 NormalZ=1 AngleXU=0 Radius=1
    g42: BSplineCurve PolesCount=3 KnotsCount=2 Degree=2 IsPeriodic=0
    g43: GeomPoint X=-12.8401 Y=-17.6958 Z=0
    g44: GeomPoint X=-14 Y=-18 Z=0
    g45: LineSegment StartX=-6.2 StartY=0 StartZ=0 EndX=-7.2 EndY=0 EndZ=0
    g46: LineSegment StartX=-7.2 StartY=0 StartZ=0 EndX=-7.2 EndY=-2 EndZ=0
    g47: LineSegment StartX=-7.2 StartY=-2 StartZ=0 EndX=-6.2215 EndY=-2 EndZ=0
    g48: LineSegment StartX=-6.32538 StartY=-4 StartZ=0 EndX=-7.65538 EndY=-4 EndZ=0
    g49: LineSegment StartX=-7.65538 StartY=-4 StartZ=0 EndX=-7.65538 EndY=-5.99526 EndZ=0
    g50: LineSegment StartX=-7.65538 StartY=-5.99526 StartZ=0 EndX=-6.48644 EndY=-5.99526 EndZ=0
    g51: LineSegment StartX=-6.77343 StartY=-8 StartZ=0 EndX=-8.43343 EndY=-8 EndZ=0
    g52: LineSegment StartX=-8.43343 StartY=-8 StartZ=0 EndX=-8.43343 EndY=-10 EndZ=0
    g53: LineSegment StartX=-8.43343 StartY=-10 StartZ=0 EndX=-7.19003 EndY=-10 EndZ=0
  constraints (112):
    c: Horizontal(g0)
    c: Distance(g0) = 2
    c: Block(g0)
    c: Vertical(g1)
    c: Coincident(g2,g0)
    c: Vertical(g2)
    c: Block(g2)
    c: Coincident(g6,g2)
    c: Weight(g3) = 1
    c: Equal(g3,g4)
    c: Equal(g3,g5)
    c: InternalAlignment(g3,g6)
    c: InternalAlignment(g4,g6)
    c: InternalAlignment(g5,g6)
    c: InternalAlignment(g7,g6)
    c: InternalAlignment(g8,g6)
    c: Block(g6)
    c: Coincident(g9,g1)
    c: Coincident(g9,g6)
    c: Horizontal(g9)
    c: Vertical(g10)
    c: Block(g10)
    c: Horizontal(g11)
    c: Block(g11)
    c: Coincident(g12,g10)
    c: Horizontal(g12)
    c: Block(g12)
    c: Coincident(g13,g11)
    c: Vertical(g13)
    c: Block(g13)
    c: Coincident(g14,g10)
    c: Horizontal(g14)
    c: Block(g14)
    c: Block(g9)
    c: Block(g1)
    c: Weight(g15) = 1
    c: Equal(g15,g16)
    c: Equal(g15,g17)
    c: InternalAlignment(g15,g18)
    c: InternalAlignment(g16,g18)
    c: InternalAlignment(g17,g18)
    c: InternalAlignment(g19,g18)
    c: InternalAlignment(g20,g18)
    c: Weight(g21) = 1
    c: Equal(g21,g22)
    c: Equal(g21,g23)
    c: InternalAlignment(g21,g24)
    c: InternalAlignment(g22,g24)
    c: InternalAlignment(g23,g24)
    c: InternalAlignment(g25,g24)
    c: InternalAlignment(g26,g24)
    c: Weight(g27) = 1
    c: Equal(g27,g28)
    c: Equal(g27,g29)
    c: Coincident(g30,g14)
    c: InternalAlignment(g27,g30)
    c: InternalAlignment(g28,g30)
    c: InternalAlignment(g29,g30)
    c: InternalAlignment(g31,g30)
    c: InternalAlignment(g32,g30)
    c: Coincident(g36,g12)
    c: Weight(g33) = 1
    c: Equal(g33,g34)
    c: Equal(g33,g35)
    c: Coincident(g36,g11)
    c: InternalAlignment(g33,g36)
    c: InternalAlignment(g34,g36)
    c: InternalAlignment(g35,g36)
    c: InternalAlignment(g37,g36)
    c: InternalAlignment(g38,g36)
    c: Coincident(g42,g13)
    c: Weight(g39) = 1
    c: Equal(g39,g40)
    c: Equal(g39,g41)
    c: Coincident(g42,g1)
    c: InternalAlignment(g39,g42)
    c: InternalAlignment(g40,g42)
    c: InternalAlignment(g41,g42)
    c: InternalAlignment(g43,g42)
    c: InternalAlignment(g44,g42)
    c: Block(g18)
    c: Block(g24)
    c: Block(g30)
    c: Block(g36)
    c: Block(g42)
    c: Horizontal(g45)
    c: Coincident(g45,g0)
    c: Vertical(g46)
    c: Coincident(g46,g45)
    c: Coincident(g47,g46)
    c: Coincident(g47,g18)
    c: Horizontal(g47)
    c: Block(g46)
    c: Coincident(g48,g18)
    c: Horizontal(g48)
    c: Distance(g48) = 1.33
    c: Vertical(g49)
    c: Coincident(g49,g48)
    c: Coincident(g50,g49)
    c: Coincident(g50,g24)
    c: Horizontal(g50)
    c: Tangent(g50,g22)
    c: Horizontal(g51)
    c: Coincident(g51,g24)
    c: Block(g51)
    c: Vertical(g52)
    c: Block(g52)
    c: Coincident(g52,g51)
    c: Coincident(g53,g52)
    c: Coincident(g53,g30)
    c: Horizontal(g53)
    c: Distance(g1) = 8.5
FEATURE [Part::Feature] Face024
  shape: bbox 9.8 x 26.5 x 2e-07 mm, 1 faces, 0 solids (baked)
FEATURE [Part::Revolution] Revolve024
  Angle = 360
  Axis = (0,1,0)
  Base = (0,0,0)
  FaceMakerClass = Part::FaceMakerBullseye
  Placement = pos=(0,0,0) rot=(0,0,1;1.5708rad)
  Solid = false
  Source = -> Face024
  Symmetric = false
FEATURE [Part::Feature] Face025
  shape: bbox 9.8 x 26.5 x 2e-07 mm, 1 faces, 0 solids (baked)
FEATURE [Part::Revolution] Revolve025
  Angle = 360
  Axis = (0,1,0)
  Base = (0,0,0)
  FaceMakerClass = Part::FaceMakerBullseye
  Placement = pos=(0,0,0) rot=(0,0,1;1.5708rad)
  Solid = false
  Source = -> Face025
  Symmetric = false
FEATURE [Part::MultiFuse] Fusion033
  Placement = pos=(-18,19,36) rot=(0,0,1;0rad)
  Shapes = -> [Revolve025,Revolve024]
FEATURE [Part::Cylinder] Cylinder014
  Angle = 360
  AttacherType = Attacher::AttachEngine3D
  Height = 20
  Placement = pos=(0,0,36.15) rot=(0,0,1;0rad)
  Radius = 14.3
FEATURE [Part::Cylinder] Cylinder015
  Angle = 360
  AttacherType = Attacher::AttachEngine3D
  Height = 10
  Placement = pos=(0,0,36.15) rot=(0,0,1;0rad)
  Radius = 4
FEATURE [Part::MultiFuse] Fusion034  label="removeToCreteHoleForPlugHousing004"
  Placement = pos=(-42,19,36) rot=(0,1,0;1.5708rad)
  Shapes = -> [Cylinder014,Cylinder015]
FEATURE [Part::Cut] Cut008  label="top004"
  Base = -> Cut004
  Placement = pos=(-1,0,0) rot=(0,0,1;0rad)
  Tool = -> Fusion034
FEATURE [Part::Box] Box005  label="Cube005"
  AttacherType = Attacher::AttachEngine3D
  Height = 28
  Length = 3
  Placement = pos=(110.7,19,22) rot=(0,0,1;0rad)
  Width = 15.7
FEATURE [Part::Cylinder] Cylinder016
  Angle = 360
  AttacherType = Attacher::AttachEngine3D
  Height = 10
  Placement = pos=(0,0,36.15) rot=(0,0,1;0rad)
  Radius = 4
FEATURE [Part::Cylinder] Cylinder017
  Angle = 360
  AttacherType = Attacher::AttachEngine3D
  Height = 20
  Placement = pos=(0,0,36.15) rot=(0,0,1;0rad)
  Radius = 10.3
FEATURE [Part::MultiFuse] Fusion035  label="removeToCreteHoleForPlugHousing005"
  Placement = pos=(70,19,36) rot=(0,1,0;1.5708rad)
  Shapes = -> [Cylinder017,Cylinder016]
FEATURE [Part::Cut] Cut009  label="plugHousingTab001"
  Base = -> Box005
  Placement = pos=(-107.4,-14,0) rot=(0,0,1;0rad)
  Tool = -> Fusion035
FEATURE [Part::Box] Box006  label="Cube006"
  AttacherType = Attacher::AttachEngine3D
  Height = 28
  Length = 3
  Placement = pos=(110.7,19,22) rot=(0,0,1;0rad)
  Width = 15.7
FEATURE [Part::Cylinder] Cylinder018
  Angle = 360
  AttacherType = Attacher::AttachEngine3D
  Height = 10
  Placement = pos=(0,0,36.15) rot=(0,0,1;0rad)
  Radius = 4
FEATURE [Part::Cylinder] Cylinder019
  Angle = 360
  AttacherType = Attacher::AttachEngine3D
  Height = 20
  Placement = pos=(0,0,36.15) rot=(0,0,1;0rad)
  Radius = 10.3
FEATURE [Part::MultiFuse] Fusion036  label="removeToCreteHoleForPlugHousing006"
  Placement = pos=(70,19,36) rot=(0,1,0;1.5708rad)
  Shapes = -> [Cylinder019,Cylinder018]
FEATURE [Part::Cut] Cut010  label="plugHousingTab002"
  Base = -> Box006
  Placement = pos=(-107.4,-14,0) rot=(0,0,1;0rad)
  Tool = -> Fusion036
FEATURE [Part::MultiFuse] Fusion037
  Placement = pos=(9.6,23,0) rot=(0,0,1;3.14159rad)
  Shapes = -> [Cut009,Cut010]
FEATURE [Part::Box] Box  label="Cube"
  AttacherType = Attacher::AttachEngine3D
  Height = 10
  Length = 3
  Placement = pos=(3.3,4,12) rot=(0,0,1;0rad)
  Width = 10
FEATURE [Part::Fillet] Fillet004
  Base = -> Fusion028
  Edges = 1 edges r=2: [Edge25]
FEATURE [Part::Fillet] Fillet005  label="plugHousing046"
  Base = -> Fillet004
  Edges = 1 edges r=2: [Edge8]
FEATURE [Part::Fillet] Fillet006
  Base = -> Box
  Edges = 1 edges r=2: [Edge11]
FEATURE [Part::Box] Box007  label="Cube007"
  AttacherType = Attacher::AttachEngine3D
  Height = 10
  Length = 3
  Placement = pos=(3.3,4,50) rot=(0,0,1;0rad)
  Width = 10
FEATURE [Part::Fillet] Fillet007
  Base = -> Box007
  Edges = 1 edges r=2: [Edge12]
FEATURE [Part::Box] Box008  label="Cube008"
  AttacherType = Attacher::AttachEngine3D
  Height = 28
  Length = 4
  Placement = pos=(5,0,22) rot=(0,0,1;0rad)
  Width = 10
FEATURE [Part::Fillet] Fillet008
  Base = -> Box008
  Edges = 1 edges r=1: [Edge7]
FEATURE [Part::Fillet] Fillet009
  Base = -> Fillet008
  Edges = 1 edges r=2: [Edge5]
FEATURE [Part::Fillet] Fillet010
  Base = -> Fillet009
  Edges = 1 edges r=2: [Edge2]
FEATURE [Sketcher::SketchObject] Sketch009  label="topSketch003"
  FullyConstrained = true
  sketch-geometry (4):
    g0: LineSegment StartX=16.8446 StartY=31.512 StartZ=0 EndX=16.3251 EndY=34.4666 EndZ=0
    g1: ArcOfCircle CenterX=19 CenterY=19.2524 CenterZ=0 NormalX=0 NormalY=0 NormalZ=1 AngleXU=0 Radius=15.4476 StartAngle=1.74483 EndAngle=2.72717
    g2: ArcOfCircle CenterX=19 CenterY=19.2524 CenterZ=0 NormalX=0 NormalY=0 NormalZ=1 AngleXU=0 Radius=12.4476 StartAngle=1.74483 EndAngle=2.73189
    g3: LineSegment StartX=4.86004 StartY=25.4725 StartZ=0 EndX=7.58253 EndY=24.2107 EndZ=0
  constraints (7):
    c: Block(g0)
    c: Coincident(g1,g0)
    c: Coincident(g2,g0)
    c: Coincident(g3,g1)
    c: Coincident(g3,g2)
    c: Block(g1)
    c: Block(g2)
FEATURE [Part::Extrusion] Extrude008
  Base = -> Sketch009
  Dir = (0,0,1)
  DirMode = 2
  FaceMakerClass = Part::FaceMakerBullseye
  LengthFwd = 10
  LengthRev = 0
  Placement = pos=(0,0,31) rot=(0,0,1;0rad)
  Solid = true
  Symmetric = false
FEATURE [Part::Cylinder] Cylinder020
  Angle = 360
  AttacherType = Attacher::AttachEngine3D
  Height = 20
  Placement = pos=(0,0,36.15) rot=(0,0,1;0rad)
  Radius = 8.2
FEATURE [Part::Cylinder] Cylinder021
  Angle = 360
  AttacherType = Attacher::AttachEngine3D
  Height = 10
  Placement = pos=(0,0,36.15) rot=(0,0,1;0rad)
  Radius = 4
FEATURE [Part::MultiFuse] Fusion038  label="removeToCreteHoleForPlugHousing007"
  Placement = pos=(-42,19,36) rot=(0,1,0;1.5708rad)
  Shapes = -> [Cylinder020,Cylinder021]
FEATURE [Part::Cut] Cut011
  Base = -> Extrude008
  Tool = -> Fusion038
FEATURE [Part::Fillet] Fillet011
  Base = -> Cut011
  Edges = 1 edges r=2: [Edge1]
FEATURE [Part::Fillet] Fillet012
  Base = -> Fillet011
  Edges = 1 edges r=2.5: [Edge1]
FEATURE [Part::Fillet] Fillet013
  Base = -> Fillet012
  Edges = 1 edges r=2.5: [Edge2]
FEATURE [Part::Box] Box010  label="Cube010"
  AttacherType = Attacher::AttachEngine3D
  Height = 16
  Length = 8
  Placement = pos=(12.7,31.52,28) rot=(0,0,1;0rad)
  Width = 4
FEATURE [Sketcher::SketchObject] Sketch010  label="topSketch004"
  FullyConstrained = true
  sketch-geometry (4):
    g0: LineSegment StartX=16.8446 StartY=31.512 StartZ=0 EndX=16.3251 EndY=34.4666 EndZ=0
    g1: ArcOfCircle CenterX=19 CenterY=19.2524 CenterZ=0 NormalX=0 NormalY=0 NormalZ=1 AngleXU=0 Radius=15.4476 StartAngle=1.74483 EndAngle=2.72717
    g2: ArcOfCircle CenterX=19 CenterY=19.2524 CenterZ=0 NormalX=0 NormalY=0 NormalZ=1 AngleXU=0 Radius=12.4476 StartAngle=1.74483 EndAngle=2.73189
    g3: LineSegment StartX=4.86004 StartY=25.4725 StartZ=0 EndX=7.58253 EndY=24.2107 EndZ=0
  constraints (7):
    c: Block(g0)
    c: Coincident(g1,g0)
    c: Coincident(g2,g0)
    c: Coincident(g3,g1)
    c: Coincident(g3,g2)
    c: Block(g1)
    c: Block(g2)
FEATURE [Part::Cylinder] Cylinder022
  Angle = 360
  AttacherType = Attacher::AttachEngine3D
  Height = 10
  Placement = pos=(0,0,36.15) rot=(0,0,1;0rad)
  Radius = 4
FEATURE [Sketcher::SketchObject] Sketch011  label="topSketch005"
  FullyConstrained = true
  sketch-geometry (4):
    g0: LineSegment StartX=16.8446 StartY=31.512 StartZ=0 EndX=16.3251 EndY=34.4666 EndZ=0
    g1: ArcOfCircle CenterX=19 CenterY=19.2524 CenterZ=0 NormalX=0 NormalY=0 NormalZ=1 AngleXU=0 Radius=15.4476 StartAngle=1.74483 EndAngle=2.72717
    g2: ArcOfCircle CenterX=19 CenterY=19.2524 CenterZ=0 NormalX=0 NormalY=0 NormalZ=1 AngleXU=0 Radius=12.4476 StartAngle=1.74483 EndAngle=2.73189
    g3: LineSegment StartX=4.86004 StartY=25.4725 StartZ=0 EndX=7.58253 EndY=24.2107 EndZ=0
  constraints (7):
    c: Block(g0)
    c: Coincident(g1,g0)
    c: Coincident(g2,g0)
    c: Coincident(g3,g1)
    c: Coincident(g3,g2)
    c: Block(g1)
    c: Block(g2)
FEATURE [Part::Extrusion] Extrude010
  Base = -> Sketch011
  Dir = (0,0,1)
  DirMode = 2
  FaceMakerClass = Part::FaceMakerBullseye
  LengthFwd = 10.6
  LengthRev = 0
  Placement = pos=(0,0,31) rot=(0,0,1;0rad)
  Solid = true
  Symmetric = false
FEATURE [Part::Cylinder] Cylinder023
  Angle = 360
  AttacherType = Attacher::AttachEngine3D
  Height = 20
  Placement = pos=(0,0,36.15) rot=(0,0,1;0rad)
  Radius = 8.2
FEATURE [Part::MultiFuse] Fusion039  label="removeToCreteHoleForPlugHousing008"
  Placement = pos=(-42,19,36) rot=(0,1,0;1.5708rad)
  Shapes = -> [Cylinder023,Cylinder022]
FEATURE [Part::Cut] Cut012
  Base = -> Extrude010
  Placement = pos=(0,0,-0.3) rot=(0,0,1;0rad)
  Tool = -> Fusion039
FEATURE [Part::Cut] Cut013
  Base = -> Box010
  Tool = -> Cut012
FEATURE [Part::Fillet] Fillet014
  Base = -> Cut013
  Edges = 1 edges r=0.7: [Edge13]
FEATURE [Part::Fillet] Fillet015
  Base = -> Fillet014
  Edges = 1 edges r=0.7: [Edge13]
FEATURE [Part::Fillet] Fillet016
  Base = -> Fillet015
  Edges = 1 edges r=0.7: [Edge16]
FEATURE [Part::Fillet] Fillet017
  Base = -> Fillet016
  Edges = 1 edges r=0.7: [Edge11]
FEATURE [Part::Fillet] Fillet018
  Base = -> Fillet017
  Edges = 1 edges r=0.7: [Edge10]
FEATURE [Part::Fillet] Fillet019
  Base = -> Fillet018
  Edges = 1 edges r=1.2: [Edge5]
FEATURE [Part::Fillet] Fillet020
  Base = -> Fillet019
  Edges = 1 edges r=1.2: [Edge12]
FEATURE [Part::Fillet] Fillet021
  Base = -> Fillet020
  Edges = 1 edges r=2: [Edge1]
  Placement = pos=(0.3,0,0) rot=(0,0,1;0rad)
FEATURE [Part::MultiFuse] Fusion040  label="top005"
  Shapes = -> [Cut008,Fillet021]
FEATURE [Part::MultiFuse] Fusion041  label="wireHolder"
  Shapes = -> [Fusion033,Fillet013]
FEATURE [Part::MultiFuse] Fusion042
  Shapes = -> [Fillet007,Fusion041]
FEATURE [Part::MultiFuse] Fusion043  label="wireHolder001"
  Shapes = -> [Fusion042,Fillet010]
FEATURE [Part::MultiFuse] Fusion044  label="wireHolder002"
  Shapes = -> [Fillet006,Fusion037,Fusion043]
FEATURE [Part::Feature] Face026
  shape: bbox 11 x 6 x 2e-07 mm, 1 faces, 0 solids (baked)
FEATURE [Part::Revolution] Revolve026
  Angle = 360
  Axis = (0,1,0)
  Base = (0,0,0)
  FaceMakerClass = Part::FaceMakerBullseye
  Placement = pos=(30.3,-1,19.7) rot=(0,0,1;0rad)
  Solid = false
  Source = -> Face026
  Symmetric = false
FEATURE [Sketcher::SketchObject] Sketch013  label="topSketch006"
  FullyConstrained = true
  sketch-geometry (13):
    g0: LineSegment StartX=117 StartY=19 StartZ=0 EndX=117 EndY=38 EndZ=0
    g1: ArcOfCircle CenterX=98 CenterY=19 CenterZ=0 NormalX=0 NormalY=0 NormalZ=1 AngleXU=0 Radius=19 StartAngle=5.7297 EndAngle=6.28319
    g2: LineSegment StartX=0 StartY=3 StartZ=0 EndX=0 EndY=19 EndZ=0
    g3: LineSegment StartX=19 StartY=38 StartZ=0 EndX=117 EndY=38 EndZ=0
    g4: ArcOfCircle CenterX=19 CenterY=19 CenterZ=0 NormalX=0 NormalY=0 NormalZ=1 AngleXU=0 Radius=19 StartAngle=1.5708 EndAngle=3.14159
    g5: ArcOfCircle CenterX=19 CenterY=19 CenterZ=0 NormalX=0 NormalY=0 NormalZ=1 AngleXU=0 Radius=16 StartAngle=1.5708 EndAngle=3.14159
    g6: ArcOfCircle CenterX=98 CenterY=19 CenterZ=0 NormalX=0 NormalY=0 NormalZ=1 AngleXU=0 Radius=16 StartAngle=5.60905 EndAngle=6.28319
    g7: LineSegment StartX=114 StartY=19 StartZ=0 EndX=114 EndY=35 EndZ=0
    g8: LineSegment StartX=110.5 StartY=9.01251 StartZ=0 EndX=114.163 EndY=9.01251 EndZ=0
    g9: LineSegment StartX=114 StartY=35 StartZ=0 EndX=19 EndY=35 EndZ=0
    g10: LineSegment StartX=0 StartY=3 StartZ=0 EndX=0 EndY=0 EndZ=0
    g11: LineSegment StartX=3 StartY=0 StartZ=0 EndX=0 EndY=0 EndZ=0
    g12: LineSegment StartX=3 StartY=19 StartZ=0 EndX=3 EndY=0 EndZ=0
  constraints (33):
    c: Vertical(g0)
    c: Distance(g0) = 19
    c: Block(g0)
    c: Coincident(g1,g0)
    c: Block(g1)
    c: Vertical(g2)
    c: Block(g2)
    c: Coincident(g3,g0)
    c: Horizontal(g3)
    c: Distance(g3) = 98
    c: Coincident(g4,g3)
    c: Coincident(g4,g2)
    c: Block(g4)
    c: Coincident(g5,g4)
    c: Coincident(g6,g1)
    c: Block(g6)
    c: Block(g5)
    c: Coincident(g7,g6)
    c: Vertical(g7)
    c: Coincident(g8,g6)
    c: Coincident(g8,g1)
    c: Coincident(g9,g7)
    c: Coincident(g9,g5)
    c: Horizontal(g9)
    c: Tangent(g9,g5)
    c: Coincident(g10,g2)
    c: Distance(g10) = 3
    c: Vertical(g10)
    c: Coincident(g11,g10)
    c: Horizontal(g11)
    c: Coincident(g12,g5)
    c: Coincident(g12,g11)
    c: Vertical(g12)
FEATURE [Part::Extrusion] Extrude011  label="top006"
  Base = -> Sketch013
  Dir = (0,0,1)
  DirMode = 2
  FaceMakerClass = Part::FaceMakerBullseye
  LengthFwd = 72
  LengthRev = 0
  Solid = true
  Symmetric = false
FEATURE [Sketcher::SketchObject] Sketch014
  FullyConstrained = true
  MapMode = 3
  Placement = pos=(0,0,0) rot=(1,0,0;1.5708rad)
  Support = -> [Extrude011]
  sketch-geometry (8):
    g0: Circle CenterX=80.351 CenterY=-67.6202 CenterZ=0 NormalX=0 NormalY=0 NormalZ=1 AngleXU=0 Radius=2
    g1: Circle CenterX=80.351 CenterY=-67.6202 CenterZ=0 NormalX=0 NormalY=0 NormalZ=1 AngleXU=0 Radius=3
    g2: Circle CenterX=80.351 CenterY=-4.92017 CenterZ=0 NormalX=0 NormalY=0 NormalZ=1 AngleXU=0 Radius=2
    g3: Circle CenterX=80.351 CenterY=-4.92017 CenterZ=0 NormalX=0 NormalY=0 NormalZ=1 AngleXU=0 Radius=3
    g4: Circle CenterX=23.851 CenterY=-4.92017 CenterZ=0 NormalX=0 NormalY=0 NormalZ=1 AngleXU=0 Radius=2
    g5: Circle CenterX=23.851 CenterY=-4.92017 CenterZ=0 NormalX=0 NormalY=0 NormalZ=1 AngleXU=0 Radius=3
    g6: Circle CenterX=23.851 CenterY=-67.6202 CenterZ=0 NormalX=0 NormalY=0 NormalZ=1 AngleXU=0 Radius=2
    g7: Circle CenterX=23.851 CenterY=-67.6202 CenterZ=0 NormalX=0 NormalY=0 NormalZ=1 AngleXU=0 Radius=3
  constraints (8):
    c: Block(g3)
    c: Block(g2)
    c: Block(g1)
    c: Block(g0)
    c: Block(g6)
    c: Block(g7)
    c: Block(g4)
    c: Block(g5)
FEATURE [Part::Feature] Face027
  shape: bbox 11 x 6 x 2e-07 mm, 1 faces, 0 solids (baked)
FEATURE [Part::Revolution] Revolve027
  Angle = 360
  Axis = (0,1,0)
  Base = (0,0,0)
  FaceMakerClass = Part::FaceMakerBullseye
  Placement = pos=(30.3,-1,51.7) rot=(0,0,1;0rad)
  Solid = false
  Source = -> Face027
  Symmetric = false
FEATURE [Part::Feature] Face028
  shape: bbox 11 x 6 x 2e-07 mm, 1 faces, 0 solids (baked)
FEATURE [Part::Revolution] Revolve028
  Angle = 360
  Axis = (0,1,0)
  Base = (0,0,0)
  FaceMakerClass = Part::FaceMakerBullseye
  Placement = pos=(62.3,-1,19.7) rot=(0,0,1;0rad)
  Solid = false
  Source = -> Face028
  Symmetric = false
FEATURE [Part::Feature] Face029
  shape: bbox 11 x 6 x 2e-07 mm, 1 faces, 0 solids (baked)
FEATURE [Part::Revolution] Revolve029
  Angle = 360
  Axis = (0,1,0)
  Base = (0,0,0)
  FaceMakerClass = Part::FaceMakerBullseye
  Placement = pos=(62.3,-1,51.7) rot=(0,0,1;0rad)
  Solid = false
  Source = -> Face029
  Symmetric = false
FEATURE [Part::Feature] Wire
  shape: bbox 11 x 5.2 x 2e-07 mm, 0 faces, 0 solids (baked)
FEATURE [Part::Revolution] Revolve030
  Angle = 360
  Axis = (0,1,0)
  Base = (0,0,0)
  FaceMakerClass = Part::FaceMakerBullseye
  Placement = pos=(30.3,38,19.7) rot=(0,0,1;0rad)
  Solid = true
  Source = -> Wire
  Symmetric = false
FEATURE [Part::Feature] Wire001
  shape: bbox 11 x 5.2 x 2e-07 mm, 0 faces, 0 solids (baked)
FEATURE [Part::Revolution] Revolve031
  Angle = 360
  Axis = (0,1,0)
  Base = (0,0,0)
  FaceMakerClass = Part::FaceMakerBullseye
  Placement = pos=(30.3,38,51.7) rot=(0,0,1;0rad)
  Solid = true
  Source = -> Wire001
  Symmetric = false
FEATURE [Part::Feature] Wire002
  shape: bbox 11 x 5.2 x 2e-07 mm, 0 faces, 0 solids (baked)
FEATURE [Part::Revolution] Revolve032
  Angle = 360
  Axis = (0,1,0)
  Base = (0,0,0)
  FaceMakerClass = Part::FaceMakerBullseye
  Placement = pos=(62.3,38,51.7) rot=(0,0,1;0rad)
  Solid = true
  Source = -> Wire002
  Symmetric = false
FEATURE [Part::Feature] Wire003
  shape: bbox 11 x 5.2 x 2e-07 mm, 0 faces, 0 solids (baked)
FEATURE [Part::Revolution] Revolve033
  Angle = 360
  Axis = (0,1,0)
  Base = (0,0,0)
  FaceMakerClass = Part::FaceMakerBullseye
  Placement = pos=(62.3,38,19.7) rot=(0,0,1;0rad)
  Solid = true
  Source = -> Wire003
  Symmetric = false
FEATURE [Part::MultiFuse] Fusion045  label="altRandScrewHousing"
  Shapes = -> [Revolve029,Revolve027,Revolve028,Revolve026]
FEATURE [Part::MultiFuse] Fusion046  label="fanScrewHousing"
  Shapes = -> [Revolve033,Revolve032,Revolve031,Revolve030]
FEATURE [Sketcher::SketchObject] Sketch015
  FullyConstrained = true
  sketch-geometry (17):
    g0: Circle CenterX=-3.5 CenterY=23.5 CenterZ=0 NormalX=0 NormalY=0 NormalZ=1 AngleXU=0 Radius=1
    g1: Circle CenterX=-1 CenterY=15.25 CenterZ=0 NormalX=0 NormalY=0 NormalZ=1 AngleXU=0 Radius=1
    g2: Circle CenterX=-3.5 CenterY=7 CenterZ=0 NormalX=0 NormalY=0 NormalZ=1 AngleXU=0 Radius=1
    g3: BSplineCurve PolesCount=3 KnotsCount=2 Degree=2 IsPeriodic=0
    g4: GeomPoint X=-3.5 Y=23.5 Z=0
    g5: GeomPoint X=-3.5 Y=7 Z=0
    g6: Circle CenterX=-4.8 CenterY=30.5 CenterZ=0 NormalX=0 NormalY=0 NormalZ=1 AngleXU=0 Radius=1
    g7: Circle CenterX=-3.5 CenterY=30.5 CenterZ=0 NormalX=0 NormalY=0 NormalZ=1 AngleXU=0 Radius=1
    g8: Circle CenterX=-3.5 CenterY=29.2 CenterZ=0 NormalX=0 NormalY=0 NormalZ=1 AngleXU=0 Radius=1
    g9: BSplineCurve PolesCount=3 KnotsCount=2 Degree=2 IsPeriodic=0
    g10: GeomPoint X=-4.8 Y=30.5 Z=0
    g11: GeomPoint X=-3.5 Y=29.2 Z=0
    g12: LineSegment StartX=-3.5 StartY=29.2 StartZ=0 EndX=-3.5 EndY=23.5 EndZ=0
    g13: LineSegment StartX=-4.8 StartY=30.5 StartZ=0 EndX=0 EndY=30.5 EndZ=0
    g14: LineSegment StartX=-3.5 StartY=0.3 StartZ=0 EndX=0 EndY=0.3 EndZ=0
    g15: LineSegment StartX=-3.5 StartY=0.3 StartZ=0 EndX=-3.5 EndY=7 EndZ=0
    g16: LineSegment StartX=0 StartY=0.3 StartZ=0 EndX=0 EndY=30.5 EndZ=0
  constraints (33):
    c: Weight(g0) = 1
    c: Equal(g0,g1)
    c: Equal(g0,g2)
    c: InternalAlignment(g0,g3)
    c: InternalAlignment(g1,g3)
    c: InternalAlignment(g2,g3)
    c: InternalAlignment(g4,g3)
    c: InternalAlignment(g5,g3)
    c: Block(g3)
    c: Weight(g6) = 1
    c: Equal(g6,g7)
    c: Equal(g6,g8)
    c: InternalAlignment(g6,g9)
    c: InternalAlignment(g7,g9)
    c: InternalAlignment(g8,g9)
    c: InternalAlignment(g10,g9)
    c: InternalAlignment(g11,g9)
    c: Block(g9)
    c: Coincident(g12,g9)
    c: Coincident(g12,g3)
    c: Vertical(g12)
    c: Coincident(g13,g9)
    c: Horizontal(g13)
    c: Distance(g13) = 4.8
    c: Horizontal(g14)
    c: Block(g14)
    c: Coincident(g15,g14)
    c: Coincident(g15,g3)
    c: Vertical(g15)
    c: Coincident(g16,g14)
    c: Coincident(g16,g13)
    c: Vertical(g16)
    c: Tangent(g16,g1)
FEATURE [Sketcher::SketchObject] Sketch016
  FullyConstrained = true
  sketch-geometry (16):
    g0: Circle CenterX=-3.5 CenterY=23.5 CenterZ=0 NormalX=0 NormalY=0 NormalZ=1 AngleXU=0 Radius=1
    g1: Circle CenterX=-1 CenterY=15.25 CenterZ=0 NormalX=0 NormalY=0 NormalZ=1 AngleXU=0 Radius=1
    g2: Circle CenterX=-3.5 CenterY=7 CenterZ=0 NormalX=0 NormalY=0 NormalZ=1 AngleXU=0 Radius=1
    g3: BSplineCurve PolesCount=3 KnotsCount=2 Degree=2 IsPeriodic=0
    g4: GeomPoint X=-3.5 Y=23.5 Z=0
    g5: GeomPoint X=-3.5 Y=7 Z=0
    g6: LineSegment StartX=-3.5 StartY=28.2 StartZ=0 EndX=-3.5 EndY=23.5 EndZ=0
    g7: LineSegment StartX=0 StartY=29.5 StartZ=0 EndX=0 EndY=30 EndZ=0
    g8: LineSegment StartX=-3.5 StartY=28.2 StartZ=0 EndX=-3.5 EndY=30 EndZ=0
    g9: LineSegment StartX=0 StartY=30 StartZ=0 EndX=0 EndY=30.5 EndZ=0
    g10: LineSegment StartX=0 StartY=30.5 StartZ=0 EndX=-3.5 EndY=30.5 EndZ=0
    g11: LineSegment StartX=-3.5 StartY=30.5 StartZ=0 EndX=-3.5 EndY=30 EndZ=0
    g12: LineSegment StartX=0 StartY=29.5 StartZ=0 EndX=0 EndY=5 EndZ=0
    g13: LineSegment StartX=-3.5 StartY=0.3 StartZ=0 EndX=-3.5 EndY=7 EndZ=0
    g14: LineSegment StartX=-3.5 StartY=0.3 StartZ=0 EndX=0 EndY=0.3 EndZ=0
    g15: LineSegment StartX=0 StartY=5 StartZ=0 EndX=0 EndY=0.3 EndZ=0
  constraints (39):
    c: Weight(g0) = 1
    c: Equal(g0,g1)
    c: Equal(g0,g2)
    c: InternalAlignment(g0,g3)
    c: InternalAlignment(g1,g3)
    c: InternalAlignment(g2,g3)
    c: InternalAlignment(g4,g3)
    c: InternalAlignment(g5,g3)
    c: Block(g3)
    c: Coincident(g6,g3)
    c: Vertical(g6)
    c: Vertical(g7)
    c: Distance(g7) = 0.5
    c: Coincident(g8,g6)
    c: Vertical(g8)
    c: Block(g6)
    c: Block(g7)
    c: Vertical(g9)
    c: Equal(g7,g9) = 0.5
    c: Block(g9)
    c: Coincident(g9,g7)
    c: Horizontal(g10)
    c: Coincident(g10,g9)
    c: Coincident(g11,g10)
    c: Coincident(g11,g8)
    c: Vertical(g11)
    c: Block(g11)
    c: Coincident(g12,g7)
    c: Vertical(g12)
    c: Coincident(g13,g3)
    c: Vertical(g13)
    c: Distance(g13) = 6.7
    c: Coincident(g14,g13)
    c: Horizontal(g14)
    c: Block(g14)
    c: Coincident(g15,g12)
    c: Coincident(g15,g14)
    c: Vertical(g15)
    c: Block(g15)
FEATURE [Sketcher::SketchObject] Sketch017
  FullyConstrained = true
  sketch-geometry (11):
    g0: LineSegment StartX=-3.5 StartY=1e-16 StartZ=0 EndX=-1.6 EndY=1e-16 EndZ=0
    g1: LineSegment StartX=-1.6 StartY=1e-16 StartZ=0 EndX=-1.6 EndY=1.5 EndZ=0
    g2: LineSegment StartX=-3.5 StartY=1.5 StartZ=0 EndX=-1.6 EndY=1.5 EndZ=0
    g3: LineSegment StartX=-3.5 StartY=1e-16 StartZ=0 EndX=-4.8 EndY=1e-16 EndZ=0
    g4: Circle CenterX=-3.5 CenterY=1.3 CenterZ=0 NormalX=0 NormalY=0 NormalZ=1 AngleXU=0 Radius=1
    g5: Circle CenterX=-3.5 CenterY=1e-16 CenterZ=0 NormalX=0 NormalY=0 NormalZ=1 AngleXU=0 Radius=1
    g6: Circle CenterX=-4.8 CenterY=1e-16 CenterZ=0 NormalX=0 NormalY=0 NormalZ=1 AngleXU=0 Radius=1
    g7: BSplineCurve PolesCount=3 KnotsCount=2 Degree=2 IsPeriodic=0
    g8: GeomPoint X=-3.5 Y=1.3 Z=0
    g9: GeomPoint X=-4.8 Y=1e-16 Z=0
    g10: LineSegment StartX=-3.5 StartY=1.3 StartZ=0 EndX=-3.5 EndY=1.5 EndZ=0
  constraints (24):
    c: Horizontal(g0)
    c: Distance(g0) = 1.9
    c: Block(g0)
    c: Coincident(g1,g0)
    c: Vertical(g1)
    c: Coincident(g2,g1)
    c: Horizontal(g2)
    c: Coincident(g3,g0)
    c: Horizontal(g3)
    c: Distance(g3) = 1.3
    c: Weight(g4) = 1
    c: Equal(g4,g5)
    c: Coincident(g5,g0)
    c: Equal(g4,g6)
    c: Coincident(g7,g3)
    c: InternalAlignment(g4,g7)
    c: InternalAlignment(g5,g7)
    c: InternalAlignment(g6,g7)
    c: InternalAlignment(g8,g7)
    c: InternalAlignment(g9,g7)
    c: Coincident(g10,g7)
    c: Coincident(g10,g2)
    c: Vertical(g10)
    c: Block(g10)
FEATURE [Part::Feature] Face035
  shape: bbox 3.2 x 1.5 x 2e-07 mm, 1 faces, 0 solids (baked)
FEATURE [Part::Revolution] Revolve039  label="backCaseScrewRetainer"
  Angle = 360
  Axis = (0,1,0)
  Base = (0,0,0)
  FaceMakerClass = Part::FaceMakerBullseye
  Placement = pos=(12.5,3,62) rot=(0,0,1;0rad)
  Solid = false
  Source = -> Face035
  Symmetric = false
FEATURE [Part::Feature] Face036
  shape: bbox 3.2 x 1.5 x 2e-07 mm, 1 faces, 0 solids (baked)
FEATURE [Part::Feature] Face039
  shape: bbox 4.8 x 30.2 x 2e-07 mm, 1 faces, 0 solids (baked)
FEATURE [Part::Revolution] Revolve043  label="frontCaseScrewPost002"
  Angle = 360
  Axis = (0,1,0)
  Base = (0,0,0)
  FaceMakerClass = Part::FaceMakerBullseye
  Placement = pos=(89.5,4.5,3.5) rot=(0,0,1;0rad)
  Solid = false
  Source = -> Face039
  Symmetric = false
FEATURE [Part::Feature] Face042
  shape: bbox 4.8 x 30.2 x 2e-07 mm, 1 faces, 0 solids (baked)
FEATURE [Part::Revolution] Revolve046  label="frontCaseScrewPost003"
  Angle = 360
  Axis = (0,1,0)
  Base = (0,0,0)
  FaceMakerClass = Part::FaceMakerBullseye
  Placement = pos=(89.5,4.5,68.5) rot=(0,0,1;0rad)
  Solid = false
  Source = -> Face042
  Symmetric = false
FEATURE [Part::Feature] Face043
  shape: bbox 3.2 x 1.5 x 2e-07 mm, 1 faces, 0 solids (baked)
FEATURE [Part::Revolution] Revolve047  label="frontCaseScrewRetainer002"
  Angle = 360
  Axis = (0,1,0)
  Base = (0,0,0)
  FaceMakerClass = Part::FaceMakerBullseye
  Placement = pos=(89.5,3,68.5) rot=(0,0,1;0rad)
  Solid = false
  Source = -> Face043
  Symmetric = false
FEATURE [Part::Feature] Face044
  shape: bbox 3.2 x 1.5 x 2e-07 mm, 1 faces, 0 solids (baked)
FEATURE [Part::Revolution] Revolve048  label="frontCaseScrewRetainer003"
  Angle = 360
  Axis = (0,1,0)
  Base = (0,0,0)
  FaceMakerClass = Part::FaceMakerBullseye
  Placement = pos=(89.5,3,3.5) rot=(0,0,1;0rad)
  Solid = false
  Source = -> Face044
  Symmetric = false
FEATURE [App::MeasureDistance] Distance002  label="Distance: 1.67 mm"
  Distance = 1.66921
  P1 = (99.2361,4.7524,71.7)
  P2 = (99.2347,6.42161,71.7)
FEATURE [Sketcher::SketchObject] Sketch018
  FullyConstrained = true
  sketch-geometry (7):
    g0: LineSegment StartX=0 StartY=0 StartZ=0 EndX=0 EndY=6 EndZ=0
    g1: Circle CenterX=0 CenterY=0 CenterZ=0 NormalX=0 NormalY=0 NormalZ=1 AngleXU=0 Radius=1
    g2: Circle CenterX=8 CenterY=6 CenterZ=0 NormalX=0 NormalY=0 NormalZ=1 AngleXU=0 Radius=1
    g3: BSplineCurve PolesCount=3 KnotsCount=2 Degree=2 IsPeriodic=0
    g4: GeomPoint X=0 Y=0 Z=0
    g5: GeomPoint X=8 Y=6 Z=0
    g6: LineSegment StartX=0 StartY=6 StartZ=0 EndX=8 EndY=6 EndZ=0
  constraints (14):
    c: Coincident(g0,g-1)
    c: Distance(g0) = 6
    c: Vertical(g0)
    c: Coincident(g3,g0)
    c: Weight(g1) = 1
    c: Equal(g1,g2)
    c: InternalAlignment(g1,g3)
    c: InternalAlignment(g2,g3)
    c: InternalAlignment(g4,g3)
    c: InternalAlignment(g5,g3)
    c: Block(g3)
    c: Coincident(g6,g0)
    c: Coincident(g6,g3)
    c: Horizontal(g6)
FEATURE [Part::Extrusion] Extrude012  label="caseScrewPillarBracket"
  Base = -> Sketch018
  Dir = (0,0,1)
  DirMode = 2
  FaceMakerClass = Part::FaceMakerBullseye
  LengthFwd = 2.4
  LengthRev = 0
  Placement = pos=(15.76,29,8.8) rot=(0,1,0;0rad)
  Solid = true
  Symmetric = false
FEATURE [Sketcher::SketchObject] Sketch019
  FullyConstrained = true
  sketch-geometry (7):
    g0: LineSegment StartX=0 StartY=0 StartZ=0 EndX=0 EndY=6 EndZ=0
    g1: Circle CenterX=0 CenterY=0 CenterZ=0 NormalX=0 NormalY=0 NormalZ=1 AngleXU=0 Radius=1
    g2: Circle CenterX=8 CenterY=6 CenterZ=0 NormalX=0 NormalY=0 NormalZ=1 AngleXU=0 Radius=1
    g3: BSplineCurve PolesCount=3 KnotsCount=2 Degree=2 IsPeriodic=0
    g4: GeomPoint X=0 Y=0 Z=0
    g5: GeomPoint X=8 Y=6 Z=0
    g6: LineSegment StartX=0 StartY=6 StartZ=0 EndX=8 EndY=6 EndZ=0
  constraints (14):
    c: Coincident(g0,g-1)
    c: Distance(g0) = 6
    c: Vertical(g0)
    c: Coincident(g3,g0)
    c: Weight(g1) = 1
    c: Equal(g1,g2)
    c: InternalAlignment(g1,g3)
    c: InternalAlignment(g2,g3)
    c: InternalAlignment(g4,g3)
    c: InternalAlignment(g5,g3)
    c: Block(g3)
    c: Coincident(g6,g0)
    c: Coincident(g6,g3)
    c: Horizontal(g6)
FEATURE [Part::Extrusion] Extrude013  label="caseScrewPillarBracket001"
  Base = -> Sketch019
  Dir = (0,0,1)
  DirMode = 2
  FaceMakerClass = Part::FaceMakerBullseye
  LengthFwd = 2.4
  LengthRev = 0
  Placement = pos=(15.76,29,60.8) rot=(0,0,1;0rad)
  Solid = true
  Symmetric = false
FEATURE [Sketcher::SketchObject] Sketch020
  FullyConstrained = true
  sketch-geometry (7):
    g0: LineSegment StartX=0 StartY=0 StartZ=0 EndX=0 EndY=6 EndZ=0
    g1: Circle CenterX=0 CenterY=0 CenterZ=0 NormalX=0 NormalY=0 NormalZ=1 AngleXU=0 Radius=1
    g2: Circle CenterX=8 CenterY=6 CenterZ=0 NormalX=0 NormalY=0 NormalZ=1 AngleXU=0 Radius=1
    g3: BSplineCurve PolesCount=3 KnotsCount=2 Degree=2 IsPeriodic=0
    g4: GeomPoint X=0 Y=0 Z=0
    g5: GeomPoint X=8 Y=6 Z=0
    g6: LineSegment StartX=0 StartY=6 StartZ=0 EndX=8 EndY=6 EndZ=0
  constraints (14):
    c: Coincident(g0,g-1)
    c: Distance(g0) = 6
    c: Vertical(g0)
    c: Coincident(g3,g0)
    c: Weight(g1) = 1
    c: Equal(g1,g2)
    c: InternalAlignment(g1,g3)
    c: InternalAlignment(g2,g3)
    c: InternalAlignment(g4,g3)
    c: InternalAlignment(g5,g3)
    c: Block(g3)
    c: Coincident(g6,g0)
    c: Coincident(g6,g3)
    c: Horizontal(g6)
FEATURE [Part::Extrusion] Extrude014  label="caseScrewPillarBracket002"
  Base = -> Sketch020
  Dir = (0,0,1)
  DirMode = 2
  FaceMakerClass = Part::FaceMakerBullseye
  LengthFwd = 2.4
  LengthRev = 0
  Placement = pos=(13.7,29,13.26) rot=(0,-1,0;1.5708rad)
  Solid = true
  Symmetric = false
FEATURE [Sketcher::SketchObject] Sketch021
  FullyConstrained = true
  sketch-geometry (7):
    g0: LineSegment StartX=0 StartY=0 StartZ=0 EndX=0 EndY=6 EndZ=0
    g1: Circle CenterX=0 CenterY=0 CenterZ=0 NormalX=0 NormalY=0 NormalZ=1 AngleXU=0 Radius=1
    g2: Circle CenterX=8 CenterY=6 CenterZ=0 NormalX=0 NormalY=0 NormalZ=1 AngleXU=0 Radius=1
    g3: BSplineCurve PolesCount=3 KnotsCount=2 Degree=2 IsPeriodic=0
    g4: GeomPoint X=0 Y=0 Z=0
    g5: GeomPoint X=8 Y=6 Z=0
    g6: LineSegment StartX=0 StartY=6 StartZ=0 EndX=8 EndY=6 EndZ=0
  constraints (14):
    c: Coincident(g0,g-1)
    c: Distance(g0) = 6
    c: Vertical(g0)
    c: Coincident(g3,g0)
    c: Weight(g1) = 1
    c: Equal(g1,g2)
    c: InternalAlignment(g1,g3)
    c: InternalAlignment(g2,g3)
    c: InternalAlignment(g4,g3)
    c: InternalAlignment(g5,g3)
    c: Block(g3)
    c: Coincident(g6,g0)
    c: Coincident(g6,g3)
    c: Horizontal(g6)
FEATURE [Part::Extrusion] Extrude015  label="caseScrewPillarBracket003"
  Base = -> Sketch021
  Dir = (0,0,1)
  DirMode = 2
  FaceMakerClass = Part::FaceMakerBullseye
  LengthFwd = 2.4
  LengthRev = 0
  Placement = pos=(11.3,29,58.74) rot=(0,1,0;1.5708rad)
  Solid = true
  Symmetric = false
FEATURE [Sketcher::SketchObject] Sketch022
  FullyConstrained = true
  sketch-geometry (7):
    g0: LineSegment StartX=0 StartY=0 StartZ=0 EndX=0 EndY=6 EndZ=0
    g1: Circle CenterX=0 CenterY=0 CenterZ=0 NormalX=0 NormalY=0 NormalZ=1 AngleXU=0 Radius=1
    g2: Circle CenterX=8 CenterY=6 CenterZ=0 NormalX=0 NormalY=0 NormalZ=1 AngleXU=0 Radius=1
    g3: BSplineCurve PolesCount=3 KnotsCount=2 Degree=2 IsPeriodic=0
    g4: GeomPoint X=0 Y=0 Z=0
    g5: GeomPoint X=8 Y=6 Z=0
    g6: LineSegment StartX=0 StartY=6 StartZ=0 EndX=8 EndY=6 EndZ=0
  constraints (14):
    c: Coincident(g0,g-1)
    c: Distance(g0) = 6
    c: Vertical(g0)
    c: Coincident(g3,g0)
    c: Weight(g1) = 1
    c: Equal(g1,g2)
    c: InternalAlignment(g1,g3)
    c: InternalAlignment(g2,g3)
    c: InternalAlignment(g4,g3)
    c: InternalAlignment(g5,g3)
    c: Block(g3)
    c: Coincident(g6,g0)
    c: Coincident(g6,g3)
    c: Horizontal(g6)
FEATURE [Part::Extrusion] Extrude016  label="caseScrewPillarBracket004"
  Base = -> Sketch022
  Dir = (0,0,1)
  DirMode = 2
  FaceMakerClass = Part::FaceMakerBullseye
  LengthFwd = 2.4
  LengthRev = 0
  Placement = pos=(88.3,29,65.23) rot=(0,1,0;1.5708rad)
  Solid = true
  Symmetric = false
FEATURE [Sketcher::SketchObject] Sketch023
  FullyConstrained = true
  sketch-geometry (7):
    g0: LineSegment StartX=0 StartY=0 StartZ=0 EndX=0 EndY=6 EndZ=0
    g1: Circle CenterX=0 CenterY=0 CenterZ=0 NormalX=0 NormalY=0 NormalZ=1 AngleXU=0 Radius=1
    g2: Circle CenterX=8 CenterY=6 CenterZ=0 NormalX=0 NormalY=0 NormalZ=1 AngleXU=0 Radius=1
    g3: BSplineCurve PolesCount=3 KnotsCount=2 Degree=2 IsPeriodic=0
    g4: GeomPoint X=0 Y=0 Z=0
    g5: GeomPoint X=8 Y=6 Z=0
    g6: LineSegment StartX=0 StartY=6 StartZ=0 EndX=8 EndY=6 EndZ=0
  constraints (14):
    c: Coincident(g0,g-1)
    c: Distance(g0) = 6
    c: Vertical(g0)
    c: Coincident(g3,g0)
    c: Weight(g1) = 1
    c: Equal(g1,g2)
    c: InternalAlignment(g1,g3)
    c: InternalAlignment(g2,g3)
    c: InternalAlignment(g4,g3)
    c: InternalAlignment(g5,g3)
    c: Block(g3)
    c: Coincident(g6,g0)
    c: Coincident(g6,g3)
    c: Horizontal(g6)
FEATURE [Part::Extrusion] Extrude017  label="caseScrewPillarBracket005"
  Base = -> Sketch023
  Dir = (0,0,1)
  DirMode = 2
  FaceMakerClass = Part::FaceMakerBullseye
  LengthFwd = 2.4
  LengthRev = 0
  Placement = pos=(90.7,29,6.77) rot=(0,-1,0;1.5708rad)
  Solid = true
  Symmetric = false
FEATURE [Sketcher::SketchObject] Sketch024
  FullyConstrained = true
  sketch-geometry (7):
    g0: LineSegment StartX=0 StartY=0 StartZ=0 EndX=0 EndY=6 EndZ=0
    g1: Circle CenterX=0 CenterY=0 CenterZ=0 NormalX=0 NormalY=0 NormalZ=1 AngleXU=0 Radius=1
    g2: Circle CenterX=8 CenterY=6 CenterZ=0 NormalX=0 NormalY=0 NormalZ=1 AngleXU=0 Radius=1
    g3: BSplineCurve PolesCount=3 KnotsCount=2 Degree=2 IsPeriodic=0
    g4: GeomPoint X=0 Y=0 Z=0
    g5: GeomPoint X=8 Y=6 Z=0
    g6: LineSegment StartX=0 StartY=6 StartZ=0 EndX=8 EndY=6 EndZ=0
  constraints (14):
    c: Coincident(g0,g-1)
    c: Distance(g0) = 6
    c: Vertical(g0)
    c: Coincident(g3,g0)
    c: Weight(g1) = 1
    c: Equal(g1,g2)
    c: InternalAlignment(g1,g3)
    c: InternalAlignment(g2,g3)
    c: InternalAlignment(g4,g3)
    c: InternalAlignment(g5,g3)
    c: Block(g3)
    c: Coincident(g6,g0)
    c: Coincident(g6,g3)
    c: Horizontal(g6)
FEATURE [Part::Extrusion] Extrude018  label="caseScrewPillarBracket006"
  Base = -> Sketch024
  Dir = (0,0,1)
  DirMode = 2
  FaceMakerClass = Part::FaceMakerBullseye
  LengthFwd = 2.4
  LengthRev = 0
  Placement = pos=(103.7,29,6.77) rot=(0,-1,0;1.5708rad)
  Solid = true
  Symmetric = false
FEATURE [Sketcher::SketchObject] Sketch025
  FullyConstrained = true
  sketch-geometry (7):
    g0: LineSegment StartX=0 StartY=0 StartZ=0 EndX=0 EndY=6 EndZ=0
    g1: Circle CenterX=0 CenterY=0 CenterZ=0 NormalX=0 NormalY=0 NormalZ=1 AngleXU=0 Radius=1
    g2: Circle CenterX=8 CenterY=6 CenterZ=0 NormalX=0 NormalY=0 NormalZ=1 AngleXU=0 Radius=1
    g3: BSplineCurve PolesCount=3 KnotsCount=2 Degree=2 IsPeriodic=0
    g4: GeomPoint X=0 Y=0 Z=0
    g5: GeomPoint X=8 Y=6 Z=0
    g6: LineSegment StartX=0 StartY=6 StartZ=0 EndX=8 EndY=6 EndZ=0
  constraints (14):
    c: Coincident(g0,g-1)
    c: Distance(g0) = 6
    c: Vertical(g0)
    c: Coincident(g3,g0)
    c: Weight(g1) = 1
    c: Equal(g1,g2)
    c: InternalAlignment(g1,g3)
    c: InternalAlignment(g2,g3)
    c: InternalAlignment(g4,g3)
    c: InternalAlignment(g5,g3)
    c: Block(g3)
    c: Coincident(g6,g0)
    c: Coincident(g6,g3)
    c: Horizontal(g6)
FEATURE [Part::Extrusion] Extrude019  label="caseScrewPillarBracket007"
  Base = -> Sketch025
  Dir = (0,0,1)
  DirMode = 2
  FaceMakerClass = Part::FaceMakerBullseye
  LengthFwd = 2.4
  LengthRev = 0
  Placement = pos=(101.3,29,65.23) rot=(0,1,0;1.5708rad)
  Solid = true
  Symmetric = false
FEATURE [Part::Box] Box011  label="frontCaseScrewPillarBracket"
  AttacherType = Attacher::AttachEngine3D
  Height = 2.4
  Length = 16
  Placement = pos=(87,28,2.3) rot=(0,0,1;0rad)
  Width = 7
FEATURE [Part::Box] Box012  label="frontCaseScrewPillarBracket001"
  AttacherType = Attacher::AttachEngine3D
  Height = 2.4
  Length = 16
  Placement = pos=(87,28,67.3) rot=(0,0,1;0rad)
  Width = 7
FEATURE [Sketcher::SketchObject] Sketch026
  FullyConstrained = true
  sketch-geometry (17):
    g0: Circle CenterX=-3.5 CenterY=23.5 CenterZ=0 NormalX=0 NormalY=0 NormalZ=1 AngleXU=0 Radius=1
    g1: Circle CenterX=-1 CenterY=15.25 CenterZ=0 NormalX=0 NormalY=0 NormalZ=1 AngleXU=0 Radius=1
    g2: Circle CenterX=-3.5 CenterY=7 CenterZ=0 NormalX=0 NormalY=0 NormalZ=1 AngleXU=0 Radius=1
    g3: BSplineCurve PolesCount=3 KnotsCount=2 Degree=2 IsPeriodic=0
    g4: GeomPoint X=-3.5 Y=23.5 Z=0
    g5: GeomPoint X=-3.5 Y=7 Z=0
    g6: Circle CenterX=-4.8 CenterY=30.5 CenterZ=0 NormalX=0 NormalY=0 NormalZ=1 AngleXU=0 Radius=1
    g7: Circle CenterX=-3.5 CenterY=30.5 CenterZ=0 NormalX=0 NormalY=0 NormalZ=1 AngleXU=0 Radius=1
    g8: Circle CenterX=-3.5 CenterY=29.2 CenterZ=0 NormalX=0 NormalY=0 NormalZ=1 AngleXU=0 Radius=1
    g9: BSplineCurve PolesCount=3 KnotsCount=2 Degree=2 IsPeriodic=0
    g10: GeomPoint X=-4.8 Y=30.5 Z=0
    g11: GeomPoint X=-3.5 Y=29.2 Z=0
    g12: LineSegment StartX=-3.5 StartY=29.2 StartZ=0 EndX=-3.5 EndY=23.5 EndZ=0
    g13: LineSegment StartX=-4.8 StartY=30.5 StartZ=0 EndX=0 EndY=30.5 EndZ=0
    g14: LineSegment StartX=-3.5 StartY=5 StartZ=0 EndX=-3.5 EndY=7 EndZ=0
    g15: LineSegment StartX=0 StartY=5 StartZ=0 EndX=0 EndY=30.5 EndZ=0
    g16: LineSegment StartX=-3.5 StartY=5 StartZ=0 EndX=0 EndY=5 EndZ=0
  constraints (33):
    c: Weight(g0) = 1
    c: Equal(g0,g1)
    c: Equal(g0,g2)
    c: InternalAlignment(g0,g3)
    c: InternalAlignment(g1,g3)
    c: InternalAlignment(g2,g3)
    c: InternalAlignment(g4,g3)
    c: InternalAlignment(g5,g3)
    c: Block(g3)
    c: Weight(g6) = 1
    c: Equal(g6,g7)
    c: Equal(g6,g8)
    c: InternalAlignment(g6,g9)
    c: InternalAlignment(g7,g9)
    c: InternalAlignment(g8,g9)
    c: InternalAlignment(g10,g9)
    c: InternalAlignment(g11,g9)
    c: Block(g9)
    c: Coincident(g12,g9)
    c: Coincident(g12,g3)
    c: Vertical(g12)
    c: Coincident(g13,g9)
    c: Horizontal(g13)
    c: Distance(g13) = 4.8
    c: Coincident(g14,g3)
    c: Vertical(g14)
    c: Coincident(g15,g13)
    c: Vertical(g15)
    c: Tangent(g15,g1)
    c: Distance(g14) = 2
    c: Coincident(g16,g14)
    c: Horizontal(g16)
    c: Coincident(g15,g16)
FEATURE [Part::Feature] Face050
  shape: bbox 4.8 x 25.5 x 2e-07 mm, 1 faces, 0 solids (baked)
FEATURE [Part::Revolution] Revolve054  label="moreFrontCaseScrewPost001"
  Angle = 360
  Axis = (0,1,0)
  Base = (0,0,0)
  FaceMakerClass = Part::FaceMakerBullseye
  Placement = pos=(102.5,4.5,3.5) rot=(0,0,1;0rad)
  Solid = false
  Source = -> Face050
  Symmetric = false
FEATURE [Part::Feature] Face051
  shape: bbox 4.8 x 25.5 x 2e-07 mm, 1 faces, 0 solids (baked)
FEATURE [Part::Revolution] Revolve055  label="moreFrontCaseScrewPost002"
  Angle = 360
  Axis = (0,1,0)
  Base = (0,0,0)
  FaceMakerClass = Part::FaceMakerBullseye
  Placement = pos=(102.5,4.5,68.5) rot=(0,0,1;0rad)
  Solid = false
  Source = -> Face051
  Symmetric = false
FEATURE [Sketcher::SketchObject] Sketch027
  FullyConstrained = true
  sketch-geometry (10):
    g0: LineSegment StartX=-1.6 StartY=4.7 StartZ=0 EndX=-1.6 EndY=1.7 EndZ=0
    g1: LineSegment StartX=-3.5 StartY=4.7 StartZ=0 EndX=-1.6 EndY=4.7 EndZ=0
    g2: LineSegment StartX=-1.6 StartY=1.7 StartZ=0 EndX=-1.6 EndY=1.5 EndZ=0
    g3: LineSegment StartX=-1.6 StartY=1.5 StartZ=0 EndX=-5.2 EndY=1.5 EndZ=0
    g4: Circle CenterX=-3.5 CenterY=4.7 CenterZ=0 NormalX=0 NormalY=0 NormalZ=1 AngleXU=0 Radius=1
    g5: Circle CenterX=-3.59627 CenterY=2.99743 CenterZ=0 NormalX=0 NormalY=0 NormalZ=1 AngleXU=0 Radius=1
    g6: Circle CenterX=-5.2 CenterY=1.5 CenterZ=0 NormalX=0 NormalY=0 NormalZ=1 AngleXU=0 Radius=1
    g7: BSplineCurve PolesCount=3 KnotsCount=2 Degree=2 IsPeriodic=0
    g8: GeomPoint X=-3.5 Y=4.7 Z=0
    g9: GeomPoint X=-5.2 Y=1.5 Z=0
  constraints (23):
    c: Vertical(g0)
    c: Distance(g0) = 3
    c: Coincident(g1,g0)
    c: Horizontal(g1)
    c: Block(g0)
    c: Block(g1)
    c: Coincident(g2,g0)
    c: Vertical(g2)
    c: Distance(g2) = 0.2
    c: Coincident(g3,g2)
    c: Horizontal(g3)
    c: Block(g3)
    c: Coincident(g7,g1)
    c: Weight(g4) = 1
    c: Equal(g4,g5)
    c: Equal(g4,g6)
    c: Coincident(g7,g3)
    c: InternalAlignment(g4,g7)
    c: InternalAlignment(g5,g7)
    c: InternalAlignment(g6,g7)
    c: InternalAlignment(g8,g7)
    c: InternalAlignment(g9,g7)
    c: Block(g7)
FEATURE [Sketcher::SketchObject] Sketch028
  FullyConstrained = true
  sketch-geometry (18):
    g0: LineSegment StartX=0 StartY=3e-16 StartZ=0 EndX=0 EndY=1.7 EndZ=0
    g1: LineSegment StartX=-3.5 StartY=0 StartZ=0 EndX=-3.5 EndY=0.9 EndZ=0
    g2: Circle CenterX=-2.7 CenterY=1.7 CenterZ=0 NormalX=0 NormalY=0 NormalZ=1 AngleXU=0 Radius=1
    g3: Circle CenterX=-3.5 CenterY=1.7 CenterZ=0 NormalX=0 NormalY=0 NormalZ=1 AngleXU=0 Radius=1
    g4: Circle CenterX=-3.5 CenterY=0.9 CenterZ=0 NormalX=0 NormalY=0 NormalZ=1 AngleXU=0 Radius=1
    g5: BSplineCurve PolesCount=3 KnotsCount=2 Degree=2 IsPeriodic=0
    g6: GeomPoint X=-2.7 Y=1.7 Z=0
    g7: GeomPoint X=-3.5 Y=0.9 Z=0
    g8: LineSegment StartX=-3.5 StartY=0 StartZ=0 EndX=-3.5 EndY=-7 EndZ=0
    g9: LineSegment StartX=0 StartY=3e-16 StartZ=0 EndX=0 EndY=-7 EndZ=0
    g10: LineSegment StartX=-3.5 StartY=-7 StartZ=0 EndX=0 EndY=-7 EndZ=0
    g11: LineSegment StartX=-2.7 StartY=1.7 StartZ=0 EndX=-1.6 EndY=1.7 EndZ=0
    g12: LineSegment StartX=0 StartY=1.7 StartZ=0 EndX=0 EndY=4.5 EndZ=0
    g13: LineSegment StartX=0 StartY=4.5 StartZ=0 EndX=0 EndY=10.8 EndZ=0
    g14: LineSegment StartX=0 StartY=10.8 StartZ=0 EndX=-2 EndY=10.8 EndZ=0
    g15: LineSegment StartX=-1.6 StartY=4.7 StartZ=0 EndX=-1.6 EndY=1.7 EndZ=0
    g16: LineSegment StartX=-1.6 StartY=4.7 StartZ=0 EndX=-2 EndY=4.7 EndZ=0
    g17: LineSegment StartX=-2 StartY=4.7 StartZ=0 EndX=-2 EndY=10.8 EndZ=0
  constraints (44):
    c: Vertical(g0)
    c: Vertical(g1)
    c: Distance(g1) = 0.9
    c: Block(g0)
    c: Distance(g0) = 1.7
    c: Weight(g2) = 1
    c: Equal(g2,g3)
    c: Equal(g2,g4)
    c: Coincident(g5,g1)
    c: InternalAlignment(g2,g5)
    c: InternalAlignment(g3,g5)
    c: InternalAlignment(g4,g5)
    c: InternalAlignment(g6,g5)
    c: InternalAlignment(g7,g5)
    c: Block(g5)
    c: Coincident(g8,g1)
    c: Vertical(g8)
    c: Distance(g8) = 7
    c: Vertical(g9)
    c: Equal(g8,g9) = 7
    c: Coincident(g9,g0)
    c: Coincident(g10,g8)
    c: Coincident(g10,g9)
    c: Horizontal(g10)
    c: Coincident(g11,g5)
    c: Horizontal(g11)
    c: Coincident(g12,g0)
    c: Vertical(g12)
    c: Distance(g12) = 2.8
    c: Coincident(g13,g12)
    c: Vertical(g13)
    c: Distance(g13) = 6.3
    c: Coincident(g14,g13)
    c: Horizontal(g14)
    c: Distance(g14) = 2
    c: Vertical(g15)
    c: Distance(g15) = 3
    c: Block(g11)
    c: Coincident(g15,g11)
    c: Coincident(g16,g15)
    c: Horizontal(g16)
    c: Coincident(g17,g16)
    c: Coincident(g17,g14)
    c: Vertical(g17)
FEATURE [Part::Revolution] Revolve040  label="backCaseScrewRetainer001"
  Angle = 360
  Axis = (0,1,0)
  Base = (0,0,0)
  FaceMakerClass = Part::FaceMakerBullseye
  Placement = pos=(12.5,3,10) rot=(0,0,1;0rad)
  Solid = false
  Source = -> Face036
  Symmetric = false
FEATURE [Part::Feature] Face055
  shape: bbox 3.5 x 30.2 x 2e-07 mm, 1 faces, 0 solids (baked)
FEATURE [Part::Revolution] Revolve059  label="backCaseScrewPost"
  Angle = 360
  Axis = (0,1,0)
  Base = (0,0,0)
  FaceMakerClass = Part::FaceMakerBullseye
  Placement = pos=(12.5,4.5,10) rot=(0,0,1;0rad)
  Solid = false
  Source = -> Face055
  Symmetric = false
FEATURE [Part::Feature] Face056
  shape: bbox 3.5 x 30.2 x 2e-07 mm, 1 faces, 0 solids (baked)
FEATURE [Part::Revolution] Revolve060  label="backCaseScrewPost001"
  Angle = 360
  Axis = (0,1,0)
  Base = (0,0,0)
  FaceMakerClass = Part::FaceMakerBullseye
  Placement = pos=(12.5,4.5,62) rot=(0,0,1;0rad)
  Solid = false
  Source = -> Face056
  Symmetric = false
FEATURE [Part::Feature] Face057
  shape: bbox 3.5 x 17.8 x 2e-07 mm, 1 faces, 0 solids (baked)
FEATURE [Part::Revolution] Revolve061  label="removeToCreateScrewAndThreadedInsertHole"
  Angle = 360
  Axis = (0,1,0)
  Base = (0,0,0)
  FaceMakerClass = Part::FaceMakerBullseye
  Placement = pos=(12.5,0,10) rot=(0,0,1;0rad)
  Solid = false
  Source = -> Face057
  Symmetric = false
FEATURE [Part::Feature] Face058
  shape: bbox 3.5 x 17.8 x 2e-07 mm, 1 faces, 0 solids (baked)
FEATURE [Part::Revolution] Revolve062  label="removeToCreateScrewAndThreadedInsertHole001"
  Angle = 360
  Axis = (0,1,0)
  Base = (0,0,0)
  FaceMakerClass = Part::FaceMakerBullseye
  Placement = pos=(12.5,0,62) rot=(0,0,1;0rad)
  Solid = false
  Source = -> Face058
  Symmetric = false
FEATURE [Part::Feature] Face059
  shape: bbox 3.5 x 17.8 x 2e-07 mm, 1 faces, 0 solids (baked)
FEATURE [Part::Revolution] Revolve063  label="removeToCreateScrewAndThreadedInsertHole002"
  Angle = 360
  Axis = (0,1,0)
  Base = (0,0,0)
  FaceMakerClass = Part::FaceMakerBullseye
  Placement = pos=(89.5,0,68.5) rot=(0,0,1;0rad)
  Solid = false
  Source = -> Face059
  Symmetric = false
FEATURE [Part::Feature] Face060
  shape: bbox 3.5 x 17.8 x 2e-07 mm, 1 faces, 0 solids (baked)
FEATURE [Part::Revolution] Revolve064  label="removeToCreateScrewAndThreadedInsertHole003"
  Angle = 360
  Axis = (0,1,0)
  Base = (0,0,0)
  FaceMakerClass = Part::FaceMakerBullseye
  Placement = pos=(89.5,0,3.5) rot=(0,0,1;0rad)
  Solid = false
  Source = -> Face060
  Symmetric = false
FEATURE [Part::Feature] Face061
  shape: bbox 3.5 x 17.8 x 2e-07 mm, 1 faces, 0 solids (baked)
FEATURE [Part::Revolution] Revolve065  label="removeToCreateScrewAndThreadedInsertHole004"
  Angle = 360
  Axis = (0,1,0)
  Base = (0,0,0)
  FaceMakerClass = Part::FaceMakerBullseye
  Placement = pos=(102.5,4.7,3.5) rot=(0,0,1;0rad)
  Solid = false
  Source = -> Face061
  Symmetric = false
FEATURE [Part::Feature] Face062
  shape: bbox 3.5 x 17.8 x 2e-07 mm, 1 faces, 0 solids (baked)
FEATURE [Part::Revolution] Revolve066  label="removeToCreateScrewAndThreadedInsertHole005"
  Angle = 360
  Axis = (0,1,0)
  Base = (0,0,0)
  FaceMakerClass = Part::FaceMakerBullseye
  Placement = pos=(102.5,4.7,68.5) rot=(0,0,1;0rad)
  Solid = false
  Source = -> Face062
  Symmetric = false
FEATURE [Part::MultiFuse] Fusion047  label="makeHoles"
  Shapes = -> [Revolve066,Revolve065,Revolve064,Revolve063,Revolve062,Revolve061]
FEATURE [Part::Feature] Face063
  shape: bbox 3.6 x 3.2 x 2e-07 mm, 1 faces, 0 solids (baked)
FEATURE [Part::Revolution] Revolve067  label="moreFrontCaseScrewRetainer002"
  Angle = 360
  Axis = (0,1,0)
  Base = (0,0,0)
  FaceMakerClass = Part::FaceMakerBullseye
  Placement = pos=(102.5,4.5,68.5) rot=(0,0,1;0rad)
  Solid = false
  Source = -> Face063
  Symmetric = false
FEATURE [Part::Feature] Face064
  shape: bbox 3.6 x 3.2 x 2e-07 mm, 1 faces, 0 solids (baked)
FEATURE [Part::Revolution] Revolve068  label="moreFrontCaseScrewRetainer003"
  Angle = 360
  Axis = (0,1,0)
  Base = (0,0,0)
  FaceMakerClass = Part::FaceMakerBullseye
  Placement = pos=(102.5,4.5,3.5) rot=(0,0,1;0rad)
  Solid = false
  Source = -> Face064
  Symmetric = false
FEATURE [Part::Feature] Face065
  shape: bbox 3.5 x 17.8 x 2e-07 mm, 1 faces, 0 solids (baked)
FEATURE [Part::Revolution] Revolve069  label="removeToCreateScrewAndThreadedInsertHole006"
  Angle = 360
  Axis = (0,1,0)
  Base = (0,0,0)
  FaceMakerClass = Part::FaceMakerBullseye
  Placement = pos=(12.5,0,10) rot=(0,0,1;0rad)
  Solid = false
  Source = -> Face065
  Symmetric = false
FEATURE [Part::Feature] Face066
  shape: bbox 3.5 x 17.8 x 2e-07 mm, 1 faces, 0 solids (baked)
FEATURE [Part::Revolution] Revolve070  label="removeToCreateScrewAndThreadedInsertHole007"
  Angle = 360
  Axis = (0,1,0)
  Base = (0,0,0)
  FaceMakerClass = Part::FaceMakerBullseye
  Placement = pos=(12.5,0,62) rot=(0,0,1;0rad)
  Solid = false
  Source = -> Face066
  Symmetric = false
FEATURE [Part::Feature] Face067
  shape: bbox 3.5 x 17.8 x 2e-07 mm, 1 faces, 0 solids (baked)
FEATURE [Part::Revolution] Revolve071  label="removeToCreateScrewAndThreadedInsertHole008"
  Angle = 360
  Axis = (0,1,0)
  Base = (0,0,0)
  FaceMakerClass = Part::FaceMakerBullseye
  Placement = pos=(89.5,0,68.5) rot=(0,0,1;0rad)
  Solid = false
  Source = -> Face067
  Symmetric = false
FEATURE [Part::Feature] Face068
  shape: bbox 3.5 x 17.8 x 2e-07 mm, 1 faces, 0 solids (baked)
FEATURE [Part::Revolution] Revolve072  label="removeToCreateScrewAndThreadedInsertHole009"
  Angle = 360
  Axis = (0,1,0)
  Base = (0,0,0)
  FaceMakerClass = Part::FaceMakerBullseye
  Placement = pos=(89.5,0,3.5) rot=(0,0,1;0rad)
  Solid = false
  Source = -> Face068
  Symmetric = false
FEATURE [Part::Feature] Face069
  shape: bbox 3.5 x 17.8 x 2e-07 mm, 1 faces, 0 solids (baked)
FEATURE [Part::Feature] Face070
  shape: bbox 3.5 x 17.8 x 2e-07 mm, 1 faces, 0 solids (baked)
FEATURE [Part::Revolution] Revolve073  label="removeToCreateScrewAndThreadedInsertHole010"
  Angle = 360
  Axis = (0,1,0)
  Base = (0,0,0)
  FaceMakerClass = Part::FaceMakerBullseye
  Placement = pos=(102.5,4.7,3.5) rot=(0,0,1;0rad)
  Solid = false
  Source = -> Face069
  Symmetric = false
FEATURE [Part::Revolution] Revolve074  label="removeToCreateScrewAndThreadedInsertHole011"
  Angle = 360
  Axis = (0,1,0)
  Base = (0,0,0)
  FaceMakerClass = Part::FaceMakerBullseye
  Placement = pos=(102.5,4.7,68.5) rot=(0,0,1;0rad)
  Solid = false
  Source = -> Face070
  Symmetric = false
FEATURE [Part::MultiFuse] Fusion048  label="makeHoles001"
  Shapes = -> [Revolve074,Revolve073,Revolve072,Revolve071,Revolve070,Revolve069]
FEATURE [Part::MultiFuse] Fusion049  label="caseScrewRetainers"
  Shapes = -> [Revolve067,Revolve068,Revolve048,Revolve047,Revolve039,Revolve040]
FEATURE [Part::Cut] Cut015  label="caseScrewRetainers001"
  Base = -> Fusion049
  Tool = -> Fusion048
FEATURE [Part::MultiFuse] Fusion050  label="casePillars"
  Shapes = -> [Revolve055,Revolve054,Revolve043,Revolve046,Revolve059,Revolve060]
FEATURE [Part::Feature] Face071 .. Face076  x6 (patterned run collapsed; names and placements below)
  shape: bbox 3.5 x 17.8 x 2e-07 mm, 1 faces, 0 solids (baked)
FEATURE [Part::Revolution] Revolve075  label="removeToCreateScrewAndThreadedInsertHole012"
  Angle = 360
  Axis = (0,1,0)
  Base = (0,0,0)
  FaceMakerClass = Part::FaceMakerBullseye
  Placement = pos=(12.5,0,10) rot=(0,0,1;0rad)
  Solid = false
  Source = -> Face071
  Symmetric = false
FEATURE [Part::Revolution] Revolve076  label="removeToCreateScrewAndThreadedInsertHole013"
  Angle = 360
  Axis = (0,1,0)
  Base = (0,0,0)
  FaceMakerClass = Part::FaceMakerBullseye
  Placement = pos=(12.5,0,62) rot=(0,0,1;0rad)
  Solid = false
  Source = -> Face072
  Symmetric = false
FEATURE [Part::Revolution] Revolve077  label="removeToCreateScrewAndThreadedInsertHole014"
  Angle = 360
  Axis = (0,1,0)
  Base = (0,0,0)
  FaceMakerClass = Part::FaceMakerBullseye
  Placement = pos=(89.5,0,68.5) rot=(0,0,1;0rad)
  Solid = false
  Source = -> Face073
  Symmetric = false
FEATURE [Part::Revolution] Revolve078  label="removeToCreateScrewAndThreadedInsertHole015"
  Angle = 360
  Axis = (0,1,0)
  Base = (0,0,0)
  FaceMakerClass = Part::FaceMakerBullseye
  Placement = pos=(89.5,0,3.5) rot=(0,0,1;0rad)
  Solid = false
  Source = -> Face074
  Symmetric = false
FEATURE [Part::Revolution] Revolve079  label="removeToCreateScrewAndThreadedInsertHole016"
  Angle = 360
  Axis = (0,1,0)
  Base = (0,0,0)
  FaceMakerClass = Part::FaceMakerBullseye
  Placement = pos=(102.5,4.7,3.5) rot=(0,0,1;0rad)
  Solid = false
  Source = -> Face075
  Symmetric = false
FEATURE [Part::Revolution] Revolve080  label="removeToCreateScrewAndThreadedInsertHole017"
  Angle = 360
  Axis = (0,1,0)
  Base = (0,0,0)
  FaceMakerClass = Part::FaceMakerBullseye
  Placement = pos=(102.5,4.7,68.5) rot=(0,0,1;0rad)
  Solid = false
  Source = -> Face076
  Symmetric = false
FEATURE [Part::MultiFuse] Fusion051  label="makeHoles002"
  Shapes = -> [Revolve080,Revolve079,Revolve078,Revolve077,Revolve076,Revolve075]
FEATURE [Part::Cut] Cut016  label="caesPillars"
  Base = -> Fusion050
  Tool = -> Fusion051
FEATURE [Part::Revolution] Revolve009  label="plugHousing016"
  Angle = 360
  Axis = (0,1,0)
  Base = (0,0,0)
  FaceMakerClass = Part::FaceMakerBullseye
  Placement = pos=(0,0,36.15) rot=(0,0,1;0rad)
  Solid = false
  Source = -> Face012
  Symmetric = false
FEATURE [Part::MultiFuse] Fusion014  label="plugHousing023"
  Placement = pos=(0,0,0) rot=(0,0,1;1.5708rad)
  Shapes = -> [Revolve011,Revolve009]
FEATURE [Part::Revolution] Revolve010  label="plugHousing017"
  Angle = 360
  Axis = (0,1,0)
  Base = (0,0,0)
  FaceMakerClass = Part::FaceMakerBullseye
  Placement = pos=(0,0,36.15) rot=(0,0,1;0rad)
  Solid = false
  Source = -> Face014
  Symmetric = false
FEATURE [Part::MultiFuse] Fusion015  label="plugHousing024"
  Placement = pos=(0,0,0) rot=(0,0,1;1.5708rad)
  Shapes = -> [Revolve010,Revolve015]
FEATURE [Part::Revolution] Revolve014  label="plugHousing026"
  Angle = 360
  Axis = (0,1,0)
  Base = (0,0,0)
  FaceMakerClass = Part::FaceMakerBullseye
  Placement = pos=(0,0,36.15) rot=(0,0,1;0rad)
  Solid = false
  Source = -> Face011
  Symmetric = false
FEATURE [Part::Revolution] Revolve013  label="plugHousing025"
  Angle = 360
  Axis = (0,1,0)
  Base = (0,0,0)
  FaceMakerClass = Part::FaceMakerBullseye
  Placement = pos=(0,0,36.15) rot=(0,0,1;0rad)
  Solid = false
  Source = -> Face015
  Symmetric = false
FEATURE [Part::MultiFuse] Fusion016  label="plugHousing028"
  Placement = pos=(0,19,0) rot=(0,0,1;3.14159rad)
  Shapes = -> [Fusion014,Fusion013]
FEATURE [Part::MultiFuse] Fusion011  label="plugHousing018"
  Placement = pos=(0,0,0) rot=(0,0,1;1.5708rad)
  Shapes = -> [Revolve014,Revolve013]
FEATURE [Part::MultiFuse] Fusion012  label="plugHousing019"
  Placement = pos=(0,19,0) rot=(0,0,1;3.14159rad)
  Shapes = -> [Fusion011,Fusion015]
FEATURE [Part::MultiFuse] Fusion017  label="plugHousing029"
  Placement = pos=(122.621,0,-0.15) rot=(0,0,1;0rad)
  Shapes = -> [Fusion016,Fusion012]
FEATURE [Part::MultiFuse] Fusion052  label="casePillarRetainers"
  Shapes = -> [Extrude012,Extrude013,Extrude014,Extrude015,Extrude016,Extrude017,Extrude018,Extrude019,Box011,Box012]
FEATURE [Part::Feature] Face077
  shape: bbox 3.5 x 17.8 x 2e-07 mm, 1 faces, 0 solids (baked)
FEATURE [Part::Revolution] Revolve081  label="removeToCreateScrewAndThreadedInsertHole018"
  Angle = 360
  Axis = (0,1,0)
  Base = (0,0,0)
  FaceMakerClass = Part::FaceMakerBullseye
  Placement = pos=(62.3,30.3,19.7) rot=(0,0,1;0rad)
  Solid = false
  Source = -> Face077
  Symmetric = false
FEATURE [Part::Feature] Face078
  shape: bbox 3.5 x 17.8 x 2e-07 mm, 1 faces, 0 solids (baked)
FEATURE [Part::Revolution] Revolve082  label="removeToCreateScrewAndThreadedInsertHole019"
  Angle = 360
  Axis = (0,1,0)
  Base = (0,0,0)
  FaceMakerClass = Part::FaceMakerBullseye
  Placement = pos=(62.3,30.3,51.7) rot=(0,0,1;0rad)
  Solid = false
  Source = -> Face078
  Symmetric = false
FEATURE [Part::Feature] Face079
  shape: bbox 3.5 x 17.8 x 2e-07 mm, 1 faces, 0 solids (baked)
FEATURE [Part::Revolution] Revolve083  label="removeToCreateScrewAndThreadedInsertHole020"
  Angle = 360
  Axis = (0,1,0)
  Base = (0,0,0)
  FaceMakerClass = Part::FaceMakerBullseye
  Placement = pos=(30.3,30.3,19.7) rot=(0,0,1;0rad)
  Solid = false
  Source = -> Face079
  Symmetric = false
FEATURE [Part::Feature] Face080
  shape: bbox 3.5 x 17.8 x 2e-07 mm, 1 faces, 0 solids (baked)
FEATURE [Part::Revolution] Revolve084  label="removeToCreateScrewAndThreadedInsertHole021"
  Angle = 360
  Axis = (0,1,0)
  Base = (0,0,0)
  FaceMakerClass = Part::FaceMakerBullseye
  Placement = pos=(30.3,30.3,51.7) rot=(0,0,1;0rad)
  Solid = false
  Source = -> Face080
  Symmetric = false
FEATURE [Part::MultiFuse] Fusion053  label="createThreadedInsertHolesForFan"
  Shapes = -> [Revolve081,Revolve082,Revolve083,Revolve084]
FEATURE [Part::Cut] Cut017  label="fanScrewHousing001"
  Base = -> Fusion046
  Tool = -> Fusion053
FEATURE [Part::Feature] Face081
  shape: bbox 3.5 x 17.8 x 2e-07 mm, 1 faces, 0 solids (baked)
FEATURE [Part::Revolution] Revolve085  label="removeToCreateScrewAndThreadedInsertHole022"
  Angle = 360
  Axis = (0,1,0)
  Base = (0,0,0)
  FaceMakerClass = Part::FaceMakerBullseye
  Placement = pos=(62.3,30.3,19.7) rot=(0,0,1;0rad)
  Solid = false
  Source = -> Face081
  Symmetric = false
FEATURE [Part::Feature] Face082
  shape: bbox 3.5 x 17.8 x 2e-07 mm, 1 faces, 0 solids (baked)
FEATURE [Part::Revolution] Revolve086  label="removeToCreateScrewAndThreadedInsertHole023"
  Angle = 360
  Axis = (0,1,0)
  Base = (0,0,0)
  FaceMakerClass = Part::FaceMakerBullseye
  Placement = pos=(62.3,30.3,51.7) rot=(0,0,1;0rad)
  Solid = false
  Source = -> Face082
  Symmetric = false
FEATURE [Part::Feature] Face083
  shape: bbox 3.5 x 17.8 x 2e-07 mm, 1 faces, 0 solids (baked)
FEATURE [Part::Revolution] Revolve087  label="removeToCreateScrewAndThreadedInsertHole024"
  Angle = 360
  Axis = (0,1,0)
  Base = (0,0,0)
  FaceMakerClass = Part::FaceMakerBullseye
  Placement = pos=(30.3,30.3,19.7) rot=(0,0,1;0rad)
  Solid = false
  Source = -> Face083
  Symmetric = false
FEATURE [Part::Feature] Face084
  shape: bbox 3.5 x 17.8 x 2e-07 mm, 1 faces, 0 solids (baked)
FEATURE [Part::Revolution] Revolve088  label="removeToCreateScrewAndThreadedInsertHole025"
  Angle = 360
  Axis = (0,1,0)
  Base = (0,0,0)
  FaceMakerClass = Part::FaceMakerBullseye
  Placement = pos=(30.3,30.3,51.7) rot=(0,0,1;0rad)
  Solid = false
  Source = -> Face084
  Symmetric = false
FEATURE [Part::MultiFuse] Fusion054  label="createThreadedInsertHolesForFan001"
  Shapes = -> [Revolve085,Revolve086,Revolve087,Revolve088]
FEATURE [Part::Cut] Cut018  label="top007"
  Base = -> Fusion040
  Tool = -> Fusion054
FEATURE [Sketcher::SketchObject] Sketch029
  FullyConstrained = false
  Placement = pos=(0,0,0) rot=(1,0,0;1.5708rad)
  sketch-geometry (24):
    g0: ArcOfCircle CenterX=-4 CenterY=-10.5 CenterZ=0 NormalX=0 NormalY=0 NormalZ=1 AngleXU=0 Radius=1.5 StartAngle=6e-16 EndAngle=3.14159
    g1: ArcOfCircle CenterX=-34.2 CenterY=-10.5 CenterZ=0 NormalX=0 NormalY=0 NormalZ=1 AngleXU=0 Radius=1.5 StartAngle=0 EndAngle=3.14159
    g2: ArcOfCircle CenterX=-34.2 CenterY=-27.7 CenterZ=0 NormalX=0 NormalY=0 NormalZ=1 AngleXU=0 Radius=1.5 StartAngle=3.14159 EndAngle=6.28319
    g3: ArcOfCircle CenterX=-4 CenterY=-27.7 CenterZ=0 NormalX=0 NormalY=0 NormalZ=1 AngleXU=0 Radius=1.5 StartAngle=3.1416 EndAngle=6.28319
    g4: ArcOfCircle CenterX=-10 CenterY=-4.3 CenterZ=0 NormalX=0 NormalY=0 NormalZ=1 AngleXU=0 Radius=1.5 StartAngle=2e-16 EndAngle=3.14159
    g5: ArcOfCircle CenterX=-16.1 CenterY=-1.8 CenterZ=0 NormalX=0 NormalY=0 NormalZ=1 AngleXU=0 Radius=1.5 StartAngle=5e-16 EndAngle=3.14159
    g6: ArcOfCircle CenterX=-22.1 CenterY=-1.8 CenterZ=0 NormalX=0 NormalY=0 NormalZ=1 AngleXU=0 Radius=1.5 StartAngle=5e-16 EndAngle=3.14159
    g7: ArcOfCircle CenterX=-28.2 CenterY=-4.3 CenterZ=0 NormalX=0 NormalY=0 NormalZ=1 AngleXU=0 Radius=1.5 StartAngle=2e-16 EndAngle=3.14159
    g8: ArcOfCircle CenterX=-10 CenterY=-33.9 CenterZ=0 NormalX=0 NormalY=0 NormalZ=1 AngleXU=0 Radius=1.5 StartAngle=3.14159 EndAngle=6.28319
    g9: ArcOfCircle CenterX=-16.1 CenterY=-36.4 CenterZ=0 NormalX=0 NormalY=0 NormalZ=1 AngleXU=0 Radius=1.5 StartAngle=3.14159 EndAngle=6.28319
    g10: ArcOfCircle CenterX=-22.1 CenterY=-36.4 CenterZ=0 NormalX=0 NormalY=0 NormalZ=1 AngleXU=0 Radius=1.5 StartAngle=3.14159 EndAngle=6.28319
    g11: ArcOfCircle CenterX=-28.2 CenterY=-33.9 CenterZ=0 NormalX=0 NormalY=0 NormalZ=1 AngleXU=0 Radius=1.5 StartAngle=3.14159 EndAngle=6.28319
    g12: LineSegment StartX=-35.7 StartY=-10.5 StartZ=0 EndX=-35.7 EndY=-27.7 EndZ=0
    g13: LineSegment StartX=-32.7 StartY=-10.5 StartZ=0 EndX=-32.7 EndY=-27.7 EndZ=0
    g14: LineSegment StartX=-29.7 StartY=-33.9 StartZ=0 EndX=-29.7 EndY=-4.3 EndZ=0
    g15: LineSegment StartX=-26.7 StartY=-33.9 StartZ=0 EndX=-26.7 EndY=-4.3 EndZ=0
    g16: LineSegment StartX=-2.5 StartY=-10.5 StartZ=0 EndX=-2.5 EndY=-27.7 EndZ=0
    g17: LineSegment StartX=-8.5 StartY=-4.3 StartZ=0 EndX=-8.5 EndY=-33.9 EndZ=0
    g18: LineSegment StartX=-5.5 StartY=-10.5 StartZ=0 EndX=-5.5 EndY=-27.7 EndZ=0
    g19: LineSegment StartX=-11.5 StartY=-4.3 StartZ=0 EndX=-11.5 EndY=-33.9 EndZ=0
    g20: LineSegment StartX=-14.6 StartY=-1.8 StartZ=0 EndX=-14.6 EndY=-36.4 EndZ=0
    g21: LineSegment StartX=-17.6 StartY=-1.8 StartZ=0 EndX=-17.6 EndY=-36.4 EndZ=0
    g22: LineSegment StartX=-20.6 StartY=-36.4 StartZ=0 EndX=-20.6 EndY=-1.8 EndZ=0
    g23: LineSegment StartX=-23.6 StartY=-1.8 StartZ=0 EndX=-23.6 EndY=-36.4 EndZ=0
  constraints (48):
    c: Block(g0)
    c: Block(g1)
    c: Block(g2)
    c: Block(g3)
    c: Block(g4)
    c: Block(g5)
    c: Block(g6)
    c: Block(g7)
    c: Block(g8)
    c: Block(g9)
    c: Block(g10)
    c: Block(g11)
    c: Coincident(g12,g1)
    c: Coincident(g12,g2)
    c: Vertical(g12)
    c: Coincident(g13,g1)
    c: Coincident(g13,g2)
    c: Vertical(g13)
    c: Coincident(g14,g11)
    c: Coincident(g14,g7)
    c: Vertical(g14)
    c: Coincident(g15,g11)
    c: Coincident(g15,g7)
    c: Vertical(g15)
    c: Coincident(g16,g0)
    c: Coincident(g16,g3)
    c: Vertical(g16)
    c: Coincident(g17,g4)
    c: Coincident(g17,g8)
    c: Vertical(g17)
    c: Coincident(g18,g0)
    c: Coincident(g18,g3)
    c: Vertical(g18)
    c: Coincident(g19,g4)
    c: Coincident(g19,g8)
    c: Vertical(g19)
    c: Coincident(g20,g5)
    c: Coincident(g20,g9)
    c: Vertical(g20)
    c: Coincident(g21,g5)
    c: Coincident(g21,g9)
    c: Vertical(g21)
    c: Coincident(g22,g10)
    c: Coincident(g22,g6)
    c: Vertical(g22)
    c: Coincident(g23,g6)
    c: Coincident(g23,g10)
    c: Vertical(g23)
FEATURE [Part::Extrusion] Extrude020  label="removeToCreateFanGrillHoles"
  Base = -> Sketch029
  Dir = (0,-1,6e-16)
  DirMode = 2
  FaceMakerClass = Part::FaceMakerBullseye
  LengthFwd = 10
  LengthRev = 0
  Placement = pos=(65.4,44,54.82) rot=(0,0,1;0rad)
  Solid = true
  Symmetric = false
FEATURE [Part::MultiFuse] Fusion055  label="top008"
  Shapes = -> [Cut017,Cut018]
FEATURE [Part::Cut] Cut019  label="top009"
  Base = -> Fusion055
  Tool = -> Extrude020
FEATURE [App::MeasureDistance] Distance003  label="Distance: 71.95 mm"
  Distance = 71.9513
  P1 = (117,38,72)
  P2 = (117,38,0.0487319)
FEATURE [Sketcher::SketchObject] Sketch030
  FullyConstrained = true
  Placement = pos=(117,19,0) rot=(0.57735,0.57735,0.57735;2.0944rad)
  sketch-geometry (48):
    g0: LineSegment StartX=-49.19 StartY=69.25 StartZ=0 EndX=-49.19 EndY=66.25 EndZ=0
    g1: LineSegment StartX=-49.19 StartY=63.5 StartZ=0 EndX=-49.19 EndY=60.5 EndZ=0
    g2: LineSegment StartX=-49.19 StartY=57.75 StartZ=0 EndX=-49.19 EndY=54.75 EndZ=0
    g3: LineSegment StartX=-49.19 StartY=52 StartZ=0 EndX=-49.19 EndY=49 EndZ=0
    g4: LineSegment StartX=-49.19 StartY=46.25 StartZ=0 EndX=-49.19 EndY=43.25 EndZ=0
    g5: LineSegment StartX=-49.19 StartY=40.5 StartZ=0 EndX=-49.19 EndY=37.5 EndZ=0
    g6: LineSegment StartX=-49.19 StartY=34.5 StartZ=0 EndX=-49.19 EndY=31.5 EndZ=0
    g7: LineSegment StartX=-49.19 StartY=28.75 StartZ=0 EndX=-49.19 EndY=25.75 EndZ=0
    g8: LineSegment StartX=-49.19 StartY=23 StartZ=0 EndX=-49.19 EndY=20 EndZ=0
    g9: LineSegment StartX=-49.19 StartY=17.25 StartZ=0 EndX=-49.19 EndY=14.25 EndZ=0
    g10: LineSegment StartX=-49.19 StartY=11.5 StartZ=0 EndX=-49.19 EndY=8.5 EndZ=0
    g11: LineSegment StartX=-49.19 StartY=5.75 StartZ=0 EndX=-49.19 EndY=2.75 EndZ=0
    g12: ArcOfCircle CenterX=-1.5 CenterY=67.75 CenterZ=0 NormalX=0 NormalY=0 NormalZ=1 AngleXU=0 Radius=1.5 StartAngle=4.71239 EndAngle=7.85398
    g13: ArcOfCircle CenterX=-1.5 CenterY=62 CenterZ=0 NormalX=0 NormalY=0 NormalZ=1 AngleXU=0 Radius=1.5 StartAngle=4.71239 EndAngle=7.85398
    g14: ArcOfCircle CenterX=-1.5 CenterY=56.25 CenterZ=0 NormalX=0 NormalY=0 NormalZ=1 AngleXU=0 Radius=1.5 StartAngle=4.71239 EndAngle=7.85398
    g15: ArcOfCircle CenterX=-11.49 CenterY=50.5 CenterZ=0 NormalX=0 NormalY=0 NormalZ=1 AngleXU=0 Radius=1.5 StartAngle=4.71239 EndAngle=7.85398
    g16: ArcOfCircle CenterX=-16.28 CenterY=44.75 CenterZ=0 NormalX=0 NormalY=0 NormalZ=1 AngleXU=0 Radius=1.5 StartAngle=4.71239 EndAngle=7.85398
    g17: ArcOfCircle CenterX=-18.2337 CenterY=39 CenterZ=0 NormalX=0 NormalY=0 NormalZ=1 AngleXU=0 Radius=1.5 StartAngle=4.71485 EndAngle=7.85398
    g18: ArcOfCircle CenterX=-16.2837 CenterY=27.25 CenterZ=0 NormalX=0 NormalY=0 NormalZ=1 AngleXU=0 Radius=1.5 StartAngle=4.71485 EndAngle=7.85398
    g19: ArcOfCircle CenterX=-18.2337 CenterY=33 CenterZ=0 NormalX=0 NormalY=0 NormalZ=1 AngleXU=0 Radius=1.5 StartAngle=4.71485 EndAngle=7.85398
    g20: ArcOfCircle CenterX=-11.49 CenterY=21.5 CenterZ=0 NormalX=0 NormalY=0 NormalZ=1 AngleXU=0 Radius=1.5 StartAngle=4.71239 EndAngle=7.85398
    g21: ArcOfCircle CenterX=-1.5 CenterY=4.25 CenterZ=0 NormalX=0 NormalY=0 NormalZ=1 AngleXU=0 Radius=1.5 StartAngle=4.71239 EndAngle=7.85398
    g22: ArcOfCircle CenterX=-1.5 CenterY=10 CenterZ=0 NormalX=0 NormalY=0 NormalZ=1 AngleXU=0 Radius=1.5 StartAngle=4.71239 EndAngle=7.85398
    g23: ArcOfCircle CenterX=-1.5 CenterY=15.75 CenterZ=0 NormalX=0 NormalY=0 NormalZ=1 AngleXU=0 Radius=1.5 StartAngle=4.71239 EndAngle=7.85398
    g24: LineSegment StartX=-49.19 StartY=69.25 StartZ=0 EndX=-1.5 EndY=69.25 EndZ=0
    g25: LineSegment StartX=-49.19 StartY=66.25 StartZ=0 EndX=-1.5 EndY=66.25 EndZ=0
    g26: LineSegment StartX=-49.19 StartY=63.5 StartZ=0 EndX=-1.5 EndY=63.5 EndZ=0
    g27: LineSegment StartX=-49.19 StartY=60.5 StartZ=0 EndX=-1.5 EndY=60.5 EndZ=0
    g28: LineSegment StartX=-49.19 StartY=57.75 StartZ=0 EndX=-1.5 EndY=57.75 EndZ=0
    g29: LineSegment StartX=-49.19 StartY=54.75 StartZ=0 EndX=-1.5 EndY=54.75 EndZ=0
    g30: LineSegment StartX=-49.19 StartY=52 StartZ=0 EndX=-11.49 EndY=52 EndZ=0
    g31: LineSegment StartX=-49.19 StartY=49 StartZ=0 EndX=-11.49 EndY=49 EndZ=0
    g32: LineSegment StartX=-49.19 StartY=46.25 StartZ=0 EndX=-16.28 EndY=46.25 EndZ=0
    g33: LineSegment StartX=-49.19 StartY=43.25 StartZ=0 EndX=-16.28 EndY=43.25 EndZ=0
    g34: LineSegment StartX=-49.19 StartY=40.5 StartZ=0 EndX=-18.2337 EndY=40.5 EndZ=0
    g35: LineSegment StartX=-49.19 StartY=37.5 StartZ=0 EndX=-18.23 EndY=37.5 EndZ=0
    g36: LineSegment StartX=-49.19 StartY=34.5 StartZ=0 EndX=-18.2337 EndY=34.5 EndZ=0
    g37: LineSegment StartX=-49.19 StartY=31.5 StartZ=0 EndX=-18.23 EndY=31.5 EndZ=0
    g38: LineSegment StartX=-49.19 StartY=28.75 StartZ=0 EndX=-16.2837 EndY=28.75 EndZ=0
    g39: LineSegment StartX=-49.19 StartY=25.75 StartZ=0 EndX=-16.28 EndY=25.75 EndZ=0
    g40: LineSegment StartX=-49.19 StartY=23 StartZ=0 EndX=-11.49 EndY=23 EndZ=0
    g41: LineSegment StartX=-49.19 StartY=20 StartZ=0 EndX=-11.49 EndY=20 EndZ=0
    g42: LineSegment StartX=-49.19 StartY=17.25 StartZ=0 EndX=-1.5 EndY=17.25 EndZ=0
    g43: LineSegment StartX=-49.19 StartY=14.25 StartZ=0 EndX=-1.5 EndY=14.25 EndZ=0
    g44: LineSegment StartX=-49.19 StartY=11.5 StartZ=0 EndX=-1.5 EndY=11.5 EndZ=0
    g45: LineSegment StartX=-49.19 StartY=8.5 StartZ=0 EndX=-1.5 EndY=8.5 EndZ=0
    g46: LineSegment StartX=-49.19 StartY=5.75 StartZ=0 EndX=-1.5 EndY=5.75 EndZ=0
    g47: LineSegment StartX=-49.19 StartY=2.75 StartZ=0 EndX=-1.5 EndY=2.75 EndZ=0
  constraints (120):
    c: Vertical(g0)
    c: Distance(g0) = 3
    c: Block(g0)
    c: Vertical(g1)
    c: Distance(g1) = 3
    c: Vertical(g2)
    c: Equal(g0,g2) = 3
    c: Block(g2)
    c: Vertical(g3)
    c: Equal(g1,g3) = 3
    c: Vertical(g4)
    c: Equal(g0,g4) = 3
    c: Block(g4)
    c: Vertical(g5)
    c: Equal(g1,g5) = 3
    c: Vertical(g6)
    c: Equal(g0,g6) = 3
    c: Block(g6)
    c: Vertical(g7)
    c: Equal(g1,g7) = 3
    c: Vertical(g8)
    c: Equal(g0,g8) = 3
    c: Block(g8)
    c: Vertical(g9)
    c: Equal(g1,g9) = 3
    c: Vertical(g10)
    c: Equal(g0,g10) = 3
    c: Block(g10)
    c: Vertical(g11)
    c: Equal(g1,g11) = 3
    c: Block(g12)
    c: Block(g13)
    c: Block(g14)
    c: Block(g15)
    c: Block(g16)
    c: Block(g17)
    c: Block(g18)
    c: Block(g19)
    c: Block(g20)
    c: Block(g21)
    c: Block(g22)
    c: Block(g23)
    c: Block(g11)
    c: Block(g9)
    c: Block(g7)
    c: Block(g5)
    c: Block(g3)
    c: Block(g1)
    c: Coincident(g24,g0)
    c: Coincident(g24,g12)
    c: Horizontal(g24)
    c: Coincident(g25,g0)
    c: Coincident(g25,g12)
    c: Horizontal(g25)
    c: Coincident(g26,g1)
    c: Coincident(g26,g13)
    c: Horizontal(g26)
    c: Coincident(g27,g1)
    c: Coincident(g27,g13)
    c: Horizontal(g27)
    c: Coincident(g28,g2)
    c: Coincident(g28,g14)
    c: Horizontal(g28)
    c: Coincident(g29,g2)
    c: Coincident(g29,g14)
    c: Horizontal(g29)
    c: Coincident(g30,g3)
    c: Coincident(g30,g15)
    c: Horizontal(g30)
    c: Coincident(g31,g3)
    c: Coincident(g31,g15)
    c: Horizontal(g31)
    c: Coincident(g32,g4)
    c: Coincident(g32,g16)
    c: Horizontal(g32)
    c: Coincident(g33,g4)
    c: Coincident(g33,g16)
    c: Horizontal(g33)
    c: Coincident(g34,g5)
    c: Coincident(g34,g17)
    c: Horizontal(g34)
    c: Coincident(g35,g5)
    c: Coincident(g35,g17)
    c: Horizontal(g35)
    c: Coincident(g36,g6)
    c: Coincident(g36,g19)
    c: Horizontal(g36)
    c: Coincident(g37,g6)
    c: Coincident(g37,g19)
    c: Horizontal(g37)
    c: Coincident(g38,g7)
    c: Coincident(g38,g18)
    c: Horizontal(g38)
    c: Coincident(g39,g7)
    c: Coincident(g39,g18)
    c: Horizontal(g39)
    c: Coincident(g40,g8)
    c: Coincident(g40,g20)
    c: Horizontal(g40)
    c: Coincident(g41,g8)
    c: Coincident(g41,g20)
    c: Horizontal(g41)
    c: Coincident(g42,g9)
    c: Coincident(g42,g23)
    c: Horizontal(g42)
    c: Coincident(g43,g9)
    c: Coincident(g43,g23)
    c: Horizontal(g43)
    c: Coincident(g44,g10)
    c: Coincident(g44,g22)
    c: Horizontal(g44)
    c: Coincident(g45,g10)
    c: Coincident(g45,g22)
    c: Horizontal(g45)
    c: Coincident(g46,g11)
    c: Coincident(g46,g21)
    c: Horizontal(g46)
    c: Coincident(g47,g11)
    c: Coincident(g47,g21)
    c: Horizontal(g47)
FEATURE [Sketcher::SketchObject] Sketch031
  FullyConstrained = true
  Placement = pos=(117,19,0) rot=(0.57735,0.57735,0.57735;2.0944rad)
  sketch-geometry (24):
    g0: ArcOfCircle CenterX=-49.19 CenterY=67.75 CenterZ=0 NormalX=0 NormalY=0 NormalZ=1 AngleXU=0 Radius=1.5 StartAngle=1.5708 EndAngle=4.71239
    g1: ArcOfCircle CenterX=-49.19 CenterY=62 CenterZ=0 NormalX=0 NormalY=0 NormalZ=1 AngleXU=0 Radius=1.5 StartAngle=1.5708 EndAngle=4.71239
    g2: ArcOfCircle CenterX=-49.19 CenterY=56.25 CenterZ=0 NormalX=0 NormalY=0 NormalZ=1 AngleXU=0 Radius=1.5 StartAngle=1.5708 EndAngle=4.71239
    g3: ArcOfCircle CenterX=-49.19 CenterY=50.5 CenterZ=0 NormalX=0 NormalY=0 NormalZ=1 AngleXU=0 Radius=1.5 StartAngle=1.5708 EndAngle=4.71239
    g4: ArcOfCircle CenterX=-49.19 CenterY=44.75 CenterZ=0 NormalX=0 NormalY=0 NormalZ=1 AngleXU=0 Radius=1.5 StartAngle=1.5708 EndAngle=4.71239
    g5: ArcOfCircle CenterX=-49.19 CenterY=39 CenterZ=0 NormalX=0 NormalY=0 NormalZ=1 AngleXU=0 Radius=1.5 StartAngle=1.5708 EndAngle=4.71239
    g6: ArcOfCircle CenterX=-49.19 CenterY=33 CenterZ=0 NormalX=0 NormalY=0 NormalZ=1 AngleXU=0 Radius=1.5 StartAngle=1.5708 EndAngle=4.71239
    g7: ArcOfCircle CenterX=-49.19 CenterY=27.25 CenterZ=0 NormalX=0 NormalY=0 NormalZ=1 AngleXU=0 Radius=1.5 StartAngle=1.5708 EndAngle=4.71239
    g8: ArcOfCircle CenterX=-49.19 CenterY=21.5 CenterZ=0 NormalX=0 NormalY=0 NormalZ=1 AngleXU=0 Radius=1.5 StartAngle=1.5708 EndAngle=4.71239
    g9: ArcOfCircle CenterX=-49.19 CenterY=15.75 CenterZ=0 NormalX=0 NormalY=0 NormalZ=1 AngleXU=0 Radius=1.5 StartAngle=1.5708 EndAngle=4.71239
    g10: ArcOfCircle CenterX=-49.19 CenterY=10 CenterZ=0 NormalX=0 NormalY=0 NormalZ=1 AngleXU=0 Radius=1.5 StartAngle=1.5708 EndAngle=4.71239
    g11: ArcOfCircle CenterX=-49.19 CenterY=4.25 CenterZ=0 NormalX=0 NormalY=0 NormalZ=1 AngleXU=0 Radius=1.5 StartAngle=1.5708 EndAngle=4.71239
    g12: LineSegment StartX=-49.19 StartY=69.25 StartZ=0 EndX=-49.19 EndY=66.25 EndZ=0
    g13: LineSegment StartX=-49.19 StartY=63.5 StartZ=0 EndX=-49.19 EndY=60.5 EndZ=0
    g14: LineSegment StartX=-49.19 StartY=57.75 StartZ=0 EndX=-49.19 EndY=54.75 EndZ=0
    g15: LineSegment StartX=-49.19 StartY=52 StartZ=0 EndX=-49.19 EndY=49 EndZ=0
    g16: LineSegment StartX=-49.19 StartY=46.25 StartZ=0 EndX=-49.19 EndY=43.25 EndZ=0
    g17: LineSegment StartX=-49.19 StartY=40.5 StartZ=0 EndX=-49.19 EndY=37.5 EndZ=0
    g18: LineSegment StartX=-49.19 StartY=34.5 StartZ=0 EndX=-49.19 EndY=31.5 EndZ=0
    g19: LineSegment StartX=-49.19 StartY=28.75 StartZ=0 EndX=-49.19 EndY=25.75 EndZ=0
    g20: LineSegment StartX=-49.19 StartY=23 StartZ=0 EndX=-49.19 EndY=20 EndZ=0
    g21: LineSegment StartX=-49.19 StartY=17.25 StartZ=0 EndX=-49.19 EndY=14.25 EndZ=0
    g22: LineSegment StartX=-49.19 StartY=11.5 StartZ=0 EndX=-49.19 EndY=8.5 EndZ=0
    g23: LineSegment StartX=-49.19 StartY=5.75 StartZ=0 EndX=-49.19 EndY=2.75 EndZ=0
  constraints (48):
    c: Block(g0)
    c: Block(g1)
    c: Block(g2)
    c: Block(g3)
    c: Block(g4)
    c: Block(g5)
    c: Block(g6)
    c: Block(g7)
    c: Block(g8)
    c: Block(g9)
    c: Block(g10)
    c: Block(g11)
    c: Coincident(g12,g0)
    c: Coincident(g12,g0)
    c: Vertical(g12)
    c: Vertical(g13)
    c: Coincident(g13,g1)
    c: Vertical(g14)
    c: Coincident(g14,g2)
    c: Vertical(g15)
    c: Coincident(g15,g3)
    c: Vertical(g16)
    c: Coincident(g16,g4)
    c: Vertical(g17)
    c: Coincident(g17,g5)
    c: Vertical(g18)
    c: Coincident(g18,g6)
    c: Vertical(g19)
    c: Coincident(g19,g7)
    c: Vertical(g20)
    c: Coincident(g20,g8)
    c: Vertical(g21)
    c: Coincident(g21,g9)
    c: Vertical(g22)
    c: Coincident(g22,g10)
    c: Vertical(g23)
    c: Coincident(g23,g11)
    c: Block(g23)
    c: Block(g22)
    c: Block(g21)
    c: Block(g20)
    c: Block(g13)
    c: Block(g14)
    c: Block(g15)
    c: Block(g16)
    c: Block(g17)
    c: Block(g18)
    c: Block(g19)
FEATURE [Part::Extrusion] Extrude022
  Base = -> Sketch030
  Dir = (1,-2e-16,2e-16)
  DirMode = 2
  FaceMakerClass = Part::FaceMakerBullseye
  LengthFwd = 19
  LengthRev = 0
  Placement = pos=(-19,0,0) rot=(0,0,1;0rad)
  Solid = true
  Symmetric = false
FEATURE [Part::Fillet] Fillet022
  Base = -> Extrude022
  Edges = 24 edges r=1.49: [Edge6,Edge11,Edge18,Edge23,Edge30,Edge35,Edge42,Edge47,Edge54,Edge59,Edge66,Edge71,Edge78,Edge83,Edge90,Edge95,Edge102,Edge107,Edge114,Edge119,Edge126,Edge131,Edge138,Edge143]
FEATURE [Part::Cut] Cut020  label="top010"
  Base = -> Cut019
  Tool = -> Fillet022
FEATURE [Sketcher::SketchObject] Sketch032
  FullyConstrained = true
  Placement = pos=(117,19,0) rot=(0.57735,0.57735,0.57735;2.0944rad)
  sketch-geometry (48):
    g0: LineSegment StartX=-49.19 StartY=69.25 StartZ=0 EndX=-49.19 EndY=66.25 EndZ=0
    g1: LineSegment StartX=-49.19 StartY=63.5 StartZ=0 EndX=-49.19 EndY=60.5 EndZ=0
    g2: LineSegment StartX=-49.19 StartY=57.75 StartZ=0 EndX=-49.19 EndY=54.75 EndZ=0
    g3: LineSegment StartX=-49.19 StartY=52 StartZ=0 EndX=-49.19 EndY=49 EndZ=0
    g4: LineSegment StartX=-49.19 StartY=46.25 StartZ=0 EndX=-49.19 EndY=43.25 EndZ=0
    g5: LineSegment StartX=-49.19 StartY=40.5 StartZ=0 EndX=-49.19 EndY=37.5 EndZ=0
    g6: LineSegment StartX=-49.19 StartY=34.5 StartZ=0 EndX=-49.19 EndY=31.5 EndZ=0
    g7: LineSegment StartX=-49.19 StartY=28.75 StartZ=0 EndX=-49.19 EndY=25.75 EndZ=0
    g8: LineSegment StartX=-49.19 StartY=23 StartZ=0 EndX=-49.19 EndY=20 EndZ=0
    g9: LineSegment StartX=-49.19 StartY=17.25 StartZ=0 EndX=-49.19 EndY=14.25 EndZ=0
    g10: LineSegment StartX=-49.19 StartY=11.5 StartZ=0 EndX=-49.19 EndY=8.5 EndZ=0
    g11: LineSegment StartX=-49.19 StartY=5.75 StartZ=0 EndX=-49.19 EndY=2.75 EndZ=0
    g12: ArcOfCircle CenterX=-1.5 CenterY=67.75 CenterZ=0 NormalX=0 NormalY=0 NormalZ=1 AngleXU=0 Radius=1.5 StartAngle=4.71239 EndAngle=7.85398
    g13: ArcOfCircle CenterX=-1.5 CenterY=62 CenterZ=0 NormalX=0 NormalY=0 NormalZ=1 AngleXU=0 Radius=1.5 StartAngle=4.71239 EndAngle=7.85398
    g14: ArcOfCircle CenterX=-1.5 CenterY=56.25 CenterZ=0 NormalX=0 NormalY=0 NormalZ=1 AngleXU=0 Radius=1.5 StartAngle=4.71239 EndAngle=7.85398
    g15: ArcOfCircle CenterX=-11.49 CenterY=50.5 CenterZ=0 NormalX=0 NormalY=0 NormalZ=1 AngleXU=0 Radius=1.5 StartAngle=4.71239 EndAngle=7.85398
    g16: ArcOfCircle CenterX=-16.28 CenterY=44.75 CenterZ=0 NormalX=0 NormalY=0 NormalZ=1 AngleXU=0 Radius=1.5 StartAngle=4.71239 EndAngle=7.85398
    g17: ArcOfCircle CenterX=-18.2337 CenterY=39 CenterZ=0 NormalX=0 NormalY=0 NormalZ=1 AngleXU=0 Radius=1.5 StartAngle=4.71485 EndAngle=7.85398
    g18: ArcOfCircle CenterX=-16.2837 CenterY=27.25 CenterZ=0 NormalX=0 NormalY=0 NormalZ=1 AngleXU=0 Radius=1.5 StartAngle=4.71485 EndAngle=7.85398
    g19: ArcOfCircle CenterX=-18.2337 CenterY=33 CenterZ=0 NormalX=0 NormalY=0 NormalZ=1 AngleXU=0 Radius=1.5 StartAngle=4.71485 EndAngle=7.85398
    g20: ArcOfCircle CenterX=-11.49 CenterY=21.5 CenterZ=0 NormalX=0 NormalY=0 NormalZ=1 AngleXU=0 Radius=1.5 StartAngle=4.71239 EndAngle=7.85398
    g21: ArcOfCircle CenterX=-1.5 CenterY=4.25 CenterZ=0 NormalX=0 NormalY=0 NormalZ=1 AngleXU=0 Radius=1.5 StartAngle=4.71239 EndAngle=7.85398
    g22: ArcOfCircle CenterX=-1.5 CenterY=10 CenterZ=0 NormalX=0 NormalY=0 NormalZ=1 AngleXU=0 Radius=1.5 StartAngle=4.71239 EndAngle=7.85398
    g23: ArcOfCircle CenterX=-1.5 CenterY=15.75 CenterZ=0 NormalX=0 NormalY=0 NormalZ=1 AngleXU=0 Radius=1.5 StartAngle=4.71239 EndAngle=7.85398
    g24: LineSegment StartX=-49.19 StartY=69.25 StartZ=0 EndX=-1.5 EndY=69.25 EndZ=0
    g25: LineSegment StartX=-49.19 StartY=66.25 StartZ=0 EndX=-1.5 EndY=66.25 EndZ=0
    g26: LineSegment StartX=-49.19 StartY=63.5 StartZ=0 EndX=-1.5 EndY=63.5 EndZ=0
    g27: LineSegment StartX=-49.19 StartY=60.5 StartZ=0 EndX=-1.5 EndY=60.5 EndZ=0
    g28: LineSegment StartX=-49.19 StartY=57.75 StartZ=0 EndX=-1.5 EndY=57.75 EndZ=0
    g29: LineSegment StartX=-49.19 StartY=54.75 StartZ=0 EndX=-1.5 EndY=54.75 EndZ=0
    g30: LineSegment StartX=-49.19 StartY=52 StartZ=0 EndX=-11.49 EndY=52 EndZ=0
    g31: LineSegment StartX=-49.19 StartY=49 StartZ=0 EndX=-11.49 EndY=49 EndZ=0
    g32: LineSegment StartX=-49.19 StartY=46.25 StartZ=0 EndX=-16.28 EndY=46.25 EndZ=0
    g33: LineSegment StartX=-49.19 StartY=43.25 StartZ=0 EndX=-16.28 EndY=43.25 EndZ=0
    g34: LineSegment StartX=-49.19 StartY=40.5 StartZ=0 EndX=-18.2337 EndY=40.5 EndZ=0
    g35: LineSegment StartX=-49.19 StartY=37.5 StartZ=0 EndX=-18.23 EndY=37.5 EndZ=0
    g36: LineSegment StartX=-49.19 StartY=34.5 StartZ=0 EndX=-18.2337 EndY=34.5 EndZ=0
    g37: LineSegment StartX=-49.19 StartY=31.5 StartZ=0 EndX=-18.23 EndY=31.5 EndZ=0
    g38: LineSegment StartX=-49.19 StartY=28.75 StartZ=0 EndX=-16.2837 EndY=28.75 EndZ=0
    g39: LineSegment StartX=-49.19 StartY=25.75 StartZ=0 EndX=-16.28 EndY=25.75 EndZ=0
    g40: LineSegment StartX=-49.19 StartY=23 StartZ=0 EndX=-11.49 EndY=23 EndZ=0
    g41: LineSegment StartX=-49.19 StartY=20 StartZ=0 EndX=-11.49 EndY=20 EndZ=0
    g42: LineSegment StartX=-49.19 StartY=17.25 StartZ=0 EndX=-1.5 EndY=17.25 EndZ=0
    g43: LineSegment StartX=-49.19 StartY=14.25 StartZ=0 EndX=-1.5 EndY=14.25 EndZ=0
    g44: LineSegment StartX=-49.19 StartY=11.5 StartZ=0 EndX=-1.5 EndY=11.5 EndZ=0
    g45: LineSegment StartX=-49.19 StartY=8.5 StartZ=0 EndX=-1.5 EndY=8.5 EndZ=0
    g46: LineSegment StartX=-49.19 StartY=5.75 StartZ=0 EndX=-1.5 EndY=5.75 EndZ=0
    g47: LineSegment StartX=-49.19 StartY=2.75 StartZ=0 EndX=-1.5 EndY=2.75 EndZ=0
  constraints (120):
    c: Vertical(g0)
    c: Distance(g0) = 3
    c: Block(g0)
    c: Vertical(g1)
    c: Distance(g1) = 3
    c: Vertical(g2)
    c: Equal(g0,g2) = 3
    c: Block(g2)
    c: Vertical(g3)
    c: Equal(g1,g3) = 3
    c: Vertical(g4)
    c: Equal(g0,g4) = 3
    c: Block(g4)
    c: Vertical(g5)
    c: Equal(g1,g5) = 3
    c: Vertical(g6)
    c: Equal(g0,g6) = 3
    c: Block(g6)
    c: Vertical(g7)
    c: Equal(g1,g7) = 3
    c: Vertical(g8)
    c: Equal(g0,g8) = 3
    c: Block(g8)
    c: Vertical(g9)
    c: Equal(g1,g9) = 3
    c: Vertical(g10)
    c: Equal(g0,g10) = 3
    c: Block(g10)
    c: Vertical(g11)
    c: Equal(g1,g11) = 3
    c: Block(g12)
    c: Block(g13)
    c: Block(g14)
    c: Block(g15)
    c: Block(g16)
    c: Block(g17)
    c: Block(g18)
    c: Block(g19)
    c: Block(g20)
    c: Block(g21)
    c: Block(g22)
    c: Block(g23)
    c: Block(g11)
    c: Block(g9)
    c: Block(g7)
    c: Block(g5)
    c: Block(g3)
    c: Block(g1)
    c: Coincident(g24,g0)
    c: Coincident(g24,g12)
    c: Horizontal(g24)
    c: Coincident(g25,g0)
    c: Coincident(g25,g12)
    c: Horizontal(g25)
    c: Coincident(g26,g1)
    c: Coincident(g26,g13)
    c: Horizontal(g26)
    c: Coincident(g27,g1)
    c: Coincident(g27,g13)
    c: Horizontal(g27)
    c: Coincident(g28,g2)
    c: Coincident(g28,g14)
    c: Horizontal(g28)
    c: Coincident(g29,g2)
    c: Coincident(g29,g14)
    c: Horizontal(g29)
    c: Coincident(g30,g3)
    c: Coincident(g30,g15)
    c: Horizontal(g30)
    c: Coincident(g31,g3)
    c: Coincident(g31,g15)
    c: Horizontal(g31)
    c: Coincident(g32,g4)
    c: Coincident(g32,g16)
    c: Horizontal(g32)
    c: Coincident(g33,g4)
    c: Coincident(g33,g16)
    c: Horizontal(g33)
    c: Coincident(g34,g5)
    c: Coincident(g34,g17)
    c: Horizontal(g34)
    c: Coincident(g35,g5)
    c: Coincident(g35,g17)
    c: Horizontal(g35)
    c: Coincident(g36,g6)
    c: Coincident(g36,g19)
    c: Horizontal(g36)
    c: Coincident(g37,g6)
    c: Coincident(g37,g19)
    c: Horizontal(g37)
    c: Coincident(g38,g7)
    c: Coincident(g38,g18)
    c: Horizontal(g38)
    c: Coincident(g39,g7)
    c: Coincident(g39,g18)
    c: Horizontal(g39)
    c: Coincident(g40,g8)
    c: Coincident(g40,g20)
    c: Horizontal(g40)
    c: Coincident(g41,g8)
    c: Coincident(g41,g20)
    c: Horizontal(g41)
    c: Coincident(g42,g9)
    c: Coincident(g42,g23)
    c: Horizontal(g42)
    c: Coincident(g43,g9)
    c: Coincident(g43,g23)
    c: Horizontal(g43)
    c: Coincident(g44,g10)
    c: Coincident(g44,g22)
    c: Horizontal(g44)
    c: Coincident(g45,g10)
    c: Coincident(g45,g22)
    c: Horizontal(g45)
    c: Coincident(g46,g11)
    c: Coincident(g46,g21)
    c: Horizontal(g46)
    c: Coincident(g47,g11)
    c: Coincident(g47,g21)
    c: Horizontal(g47)
FEATURE [Part::Extrusion] Extrude023
  Base = -> Sketch032
  Dir = (1,-2e-16,2e-16)
  DirMode = 2
  FaceMakerClass = Part::FaceMakerBullseye
  LengthFwd = 19
  LengthRev = 0
  Placement = pos=(-19,0,0) rot=(0,0,1;0rad)
  Solid = true
  Symmetric = false
FEATURE [Part::Fillet] Fillet023
  Base = -> Extrude023
  Edges = <same value as first occurrence — deduplicated (x4 in doc)>
  Placement = pos=(0,0.05,0) rot=(0,0,1;0rad)
FEATURE [Part::Cut] Cut014  label="bottom003"
  Base = -> Cut007
  Tool = -> Fusion047
FEATURE [Part::Cut] Cut021  label="bottom004"
  Base = -> Cut014
  Tool = -> Fillet023
FEATURE [Sketcher::SketchObject] Sketch033
  FullyConstrained = true
  Placement = pos=(117,19,0) rot=(0.57735,0.57735,0.57735;2.0944rad)
  sketch-geometry (8):
    g0: LineSegment StartX=-49.19 StartY=69.25 StartZ=0 EndX=-49.19 EndY=66.25 EndZ=0
    g1: LineSegment StartX=-49.19 StartY=5.75 StartZ=0 EndX=-49.19 EndY=2.75 EndZ=0
    g2: ArcOfCircle CenterX=-1.5 CenterY=67.75 CenterZ=0 NormalX=0 NormalY=0 NormalZ=1 AngleXU=0 Radius=1.5 StartAngle=4.71239 EndAngle=7.85398
    g3: ArcOfCircle CenterX=-1.5 CenterY=4.25 CenterZ=0 NormalX=0 NormalY=0 NormalZ=1 AngleXU=0 Radius=1.5 StartAngle=4.71239 EndAngle=7.85398
    g4: LineSegment StartX=-49.19 StartY=69.25 StartZ=0 EndX=-1.5 EndY=69.25 EndZ=0
    g5: LineSegment StartX=-49.19 StartY=66.25 StartZ=0 EndX=-1.5 EndY=66.25 EndZ=0
    g6: LineSegment StartX=-49.19 StartY=5.75 StartZ=0 EndX=-1.5 EndY=5.75 EndZ=0
    g7: LineSegment StartX=-49.19 StartY=2.75 StartZ=0 EndX=-1.5 EndY=2.75 EndZ=0
  constraints (19):
    c: Vertical(g0)
    c: Distance(g0) = 3
    c: Block(g0)
    c: Vertical(g1)
    c: Block(g2)
    c: Block(g3)
    c: Block(g1)
    c: Coincident(g4,g0)
    c: Coincident(g4,g2)
    c: Horizontal(g4)
    c: Coincident(g5,g0)
    c: Coincident(g5,g2)
    c: Horizontal(g5)
    c: Coincident(g6,g1)
    c: Coincident(g6,g3)
    c: Horizontal(g6)
    c: Coincident(g7,g1)
    c: Coincident(g7,g3)
    c: Horizontal(g7)
FEATURE [Sketcher::SketchObject] Sketch034
  FullyConstrained = true
  Placement = pos=(117,19,0) rot=(0.57735,0.57735,0.57735;2.0944rad)
  sketch-geometry (8):
    g0: LineSegment StartX=-49.19 StartY=63.5 StartZ=0 EndX=-49.19 EndY=60.5 EndZ=0
    g1: LineSegment StartX=-49.19 StartY=11.5 StartZ=0 EndX=-49.19 EndY=8.5 EndZ=0
    g2: ArcOfCircle CenterX=-1.5 CenterY=62 CenterZ=0 NormalX=0 NormalY=0 NormalZ=1 AngleXU=0 Radius=1.5 StartAngle=4.71239 EndAngle=7.85398
    g3: ArcOfCircle CenterX=-1.5 CenterY=10 CenterZ=0 NormalX=0 NormalY=0 NormalZ=1 AngleXU=0 Radius=1.5 StartAngle=4.71239 EndAngle=7.85398
    g4: LineSegment StartX=-49.19 StartY=63.5 StartZ=0 EndX=-1.5 EndY=63.5 EndZ=0
    g5: LineSegment StartX=-49.19 StartY=60.5 StartZ=0 EndX=-1.5 EndY=60.5 EndZ=0
    g6: LineSegment StartX=-49.19 StartY=11.5 StartZ=0 EndX=-1.5 EndY=11.5 EndZ=0
    g7: LineSegment StartX=-49.19 StartY=8.5 StartZ=0 EndX=-1.5 EndY=8.5 EndZ=0
  constraints (19):
    c: Vertical(g0)
    c: Distance(g0) = 3
    c: Vertical(g1)
    c: Block(g1)
    c: Block(g2)
    c: Block(g3)
    c: Block(g0)
    c: Coincident(g4,g0)
    c: Coincident(g4,g2)
    c: Horizontal(g4)
    c: Coincident(g5,g0)
    c: Coincident(g5,g2)
    c: Horizontal(g5)
    c: Coincident(g6,g1)
    c: Coincident(g6,g3)
    c: Horizontal(g6)
    c: Coincident(g7,g1)
    c: Coincident(g7,g3)
    c: Horizontal(g7)
FEATURE [Part::Extrusion] Extrude024
  Base = -> Sketch033
  Dir = (1,0,0)
  DirMode = 2
  FaceMakerClass = Part::FaceMakerBullseye
  LengthFwd = 10
  LengthRev = 0
  Solid = true
  Symmetric = false
FEATURE [Part::Extrusion] Extrude025
  Base = -> Sketch034
  Dir = (1,0,0)
  DirMode = 2
  FaceMakerClass = Part::FaceMakerBullseye
  LengthFwd = 10
  LengthRev = 0
  Solid = true
  Symmetric = false
FEATURE [Part::Fillet] Fillet024  label="removeFromtMoreFrontCaseScrewRetainers"
  Base = -> Extrude024
  Edges = 4 edges r=1.49: [Edge6,Edge11,Edge18,Edge23]
  Placement = pos=(-11,0,0) rot=(0,0,1;0rad)
FEATURE [Part::Fillet] Fillet025  label="removeFromtMoreFrontCaseScrewRetainers001"
  Base = -> Extrude025
  Edges = 4 edges r=1.49: [Edge6,Edge11,Edge18,Edge23]
  Placement = pos=(-19,0,0) rot=(0,0,1;0rad)
FEATURE [Part::Cut] Cut022
  Base = -> Cut015
  Tool = -> Fillet025
FEATURE [Part::Cut] Cut023  label="screwRetainers"
  Base = -> Cut022
  Tool = -> Fillet024
FEATURE [Part::MultiFuse] Fusion056  label="bottom005"
  Shapes = -> [Fusion044,Cut021]
FEATURE [Part::MultiFuse] Fusion057  label="casePillars001"
  Shapes = -> [Cut016,Fusion052]
FEATURE [Part::MultiFuse] Fusion058  label="bottom006"
  Shapes = -> [Fusion056,Cut023]
FEATURE [Part::MultiFuse] Fusion059  label="bottom007"
  Shapes = -> [Fusion058,Fillet005]
FEATURE [Part::MultiFuse] Fusion060  label="bottom008"
  Shapes = -> [Fusion059,Fusion]
FEATURE [Part::MultiFuse] Fusion061  label="top011"
  Shapes = -> [Cut006,Cut020]
FEATURE [Part::MultiFuse] Fusion062  label="top012"
  Shapes = -> [Fusion057,Fusion061]
FEATURE [Sketcher::SketchObject] Sketch035  label="topSketch007"
  FullyConstrained = true
  sketch-geometry (6):
    g0: LineSegment StartX=19 StartY=38 StartZ=0 EndX=117 EndY=38 EndZ=0
    g1: ArcOfCircle CenterX=19 CenterY=19 CenterZ=0 NormalX=0 NormalY=0 NormalZ=1 AngleXU=0 Radius=19 StartAngle=1.5708 EndAngle=3.14159
    g2: LineSegment StartX=117 StartY=38 StartZ=0 EndX=117 EndY=19 EndZ=0
    g3: LineSegment StartX=98 StartY=1.0161e-12 StartZ=0 EndX=5.22862e-06 EndY=1.0161e-12 EndZ=0
    g4: LineSegment StartX=5.22862e-06 StartY=19 StartZ=0 EndX=5.22862e-06 EndY=1.0161e-12 EndZ=0
    g5: ArcOfCircle CenterX=98 CenterY=19 CenterZ=0 NormalX=0 NormalY=0 NormalZ=1 AngleXU=0 Radius=19 StartAngle=4.71239 EndAngle=6.28319
  constraints (16):
    c: Horizontal(g0)
    c: Distance(g0) = 98
    c: Coincident(g1,g0)
    c: Block(g1)
    c: Coincident(g2,g0)
    c: Vertical(g2)
    c: Distance(g2) = 19
    c: Horizontal(g3)
    c: Coincident(g4,g1)
    c: Vertical(g4)
    c: Coincident(g3,g4)
    c: Block(g3)
    c: Coincident(g5,g2)
    c: Coincident(g5,g3)
    c: Block(g0)
    c: Block(g5)
FEATURE [Part::Extrusion] Extrude026  label="sideA001"
  Base = -> Sketch035
  Dir = (0,0,1)
  DirMode = 2
  FaceMakerClass = Part::FaceMakerBullseye
  LengthFwd = 3
  LengthRev = 0
  Placement = pos=(0,0,-2.7) rot=(0,0,1;0rad)
  Solid = true
  Symmetric = false
FEATURE [Sketcher::SketchObject] Sketch036  label="topSketch008"
  FullyConstrained = true
  sketch-geometry (6):
    g0: LineSegment StartX=19 StartY=38 StartZ=0 EndX=117 EndY=38 EndZ=0
    g1: ArcOfCircle CenterX=19 CenterY=19 CenterZ=0 NormalX=0 NormalY=0 NormalZ=1 AngleXU=0 Radius=19 StartAngle=1.5708 EndAngle=3.14159
    g2: LineSegment StartX=117 StartY=38 StartZ=0 EndX=117 EndY=19 EndZ=0
    g3: LineSegment StartX=98 StartY=1.0161e-12 StartZ=0 EndX=5.22862e-06 EndY=1.0161e-12 EndZ=0
    g4: LineSegment StartX=5.22862e-06 StartY=19 StartZ=0 EndX=5.22862e-06 EndY=1.0161e-12 EndZ=0
    g5: ArcOfCircle CenterX=98 CenterY=19 CenterZ=0 NormalX=0 NormalY=0 NormalZ=1 AngleXU=0 Radius=19 StartAngle=4.71239 EndAngle=6.28319
  constraints (16):
    c: Horizontal(g0)
    c: Distance(g0) = 98
    c: Coincident(g1,g0)
    c: Block(g1)
    c: Coincident(g2,g0)
    c: Vertical(g2)
    c: Distance(g2) = 19
    c: Horizontal(g3)
    c: Coincident(g4,g1)
    c: Vertical(g4)
    c: Coincident(g3,g4)
    c: Block(g3)
    c: Coincident(g5,g2)
    c: Coincident(g5,g3)
    c: Block(g0)
    c: Block(g5)
FEATURE [Part::Extrusion] Extrude027  label="sideB001"
  Base = -> Sketch036
  Dir = (0,0,1)
  DirMode = 2
  FaceMakerClass = Part::FaceMakerBullseye
  LengthFwd = 3
  LengthRev = 0
  Placement = pos=(0,0,71.7) rot=(0,0,1;0rad)
  Solid = true
  Symmetric = false
FEATURE [Part::MultiFuse] Fusion064  label="removeFromBottom"
  Shapes = -> [Extrude026,Extrude027]
FEATURE [Part::Cut] Cut024  label="bottom009"
  Base = -> Fusion060
  Tool = -> Fusion064
FEATURE [Sketcher::SketchObject] Sketch037  label="topSketch009"
  FullyConstrained = true
  sketch-geometry (6):
    g0: ArcOfCircle CenterX=19 CenterY=19 CenterZ=0 NormalX=0 NormalY=0 NormalZ=1 AngleXU=0 Radius=19 StartAngle=1.5708 EndAngle=3.14159
    g1: LineSegment StartX=5.22862e-06 StartY=19 StartZ=0 EndX=5.22862e-06 EndY=1.19904e-11 EndZ=0
    g2: LineSegment StartX=19 StartY=38 StartZ=0 EndX=124 EndY=38 EndZ=0
    g3: LineSegment StartX=5.22862e-06 StartY=1.19904e-11 StartZ=0 EndX=105 EndY=1.19904e-11 EndZ=0
    g4: ArcOfCircle CenterX=105 CenterY=19 CenterZ=0 NormalX=0 NormalY=0 NormalZ=1 AngleXU=0 Radius=19 StartAngle=4.71239 EndAngle=6.28319
    g5: LineSegment StartX=124 StartY=38 StartZ=0 EndX=124 EndY=19 EndZ=0
  constraints (16):
    c: Block(g0)
    c: Coincident(g1,g0)
    c: Vertical(g1)
    c: Horizontal(g2)
    c: Distance(g2) = 105
    c: Coincident(g2,g0)
    c: Distance(g1) = 19
    c: Coincident(g3,g1)
    c: Horizontal(g3)
    c: Distance(g3) = 105
    c: Block(g4)
    c: Coincident(g4,g3)
    c: Coincident(g5,g2)
    c: Coincident(g5,g4)
    c: Vertical(g5)
    c: Distance(g5) = 19
FEATURE [Part::Extrusion] Extrude028  label="sideB"
  Base = -> Sketch037
  Dir = (0,0,1)
  DirMode = 2
  FaceMakerClass = Part::FaceMakerBullseye
  LengthFwd = 3
  LengthRev = 0
  Placement = pos=(0,0,72) rot=(0,0,1;0rad)
  Solid = true
  Symmetric = false
FEATURE [Sketcher::SketchObject] Sketch038  label="topSketch010"
  FullyConstrained = true
  sketch-geometry (22):
    g0: LineSegment StartX=5.21097e-06 StartY=3 StartZ=0 EndX=5.21097e-06 EndY=19 EndZ=0
    g1: ArcOfCircle CenterX=19 CenterY=19 CenterZ=0 NormalX=0 NormalY=0 NormalZ=1 AngleXU=0 Radius=19 StartAngle=1.5708 EndAngle=3.14159
    g2: ArcOfCircle CenterX=19 CenterY=19 CenterZ=0 NormalX=0 NormalY=0 NormalZ=1 AngleXU=0 Radius=16 StartAngle=1.5708 EndAngle=3.14159
    g3: LineSegment StartX=114 StartY=35 StartZ=0 EndX=19 EndY=35 EndZ=0
    g4: LineSegment StartX=5.21097e-06 StartY=3 StartZ=0 EndX=5.21097e-06 EndY=0 EndZ=0
    g5: LineSegment StartX=3 StartY=0 StartZ=0 EndX=5.21097e-06 EndY=0 EndZ=0
    g6: LineSegment StartX=3 StartY=19 StartZ=0 EndX=3 EndY=0 EndZ=0
    g7: LineSegment StartX=19 StartY=38 StartZ=0 EndX=124 EndY=38 EndZ=0
    g8: Circle CenterX=119 CenterY=35 CenterZ=0 NormalX=0 NormalY=0 NormalZ=1 AngleXU=0 Radius=1
    g9: Circle CenterX=121 CenterY=35 CenterZ=0 NormalX=0 NormalY=0 NormalZ=1 AngleXU=0 Radius=1
    g10: Circle CenterX=121 CenterY=33 CenterZ=0 NormalX=0 NormalY=0 NormalZ=1 AngleXU=0 Radius=1
    g11: BSplineCurve PolesCount=3 KnotsCount=2 Degree=2 IsPeriodic=0
    g12: GeomPoint X=119 Y=35 Z=0
    g13: GeomPoint X=121 Y=33 Z=0
    g14: LineSegment StartX=119 StartY=35 StartZ=0 EndX=114 EndY=35 EndZ=0
    g15: ArcOfCircle CenterX=105 CenterY=19 CenterZ=0 NormalX=0 NormalY=0 NormalZ=1 AngleXU=0 Radius=16 StartAngle=5.60905 EndAngle=6.28319
    g16: LineSegment StartX=121 StartY=33 StartZ=0 EndX=121 EndY=19 EndZ=0
    g17: LineSegment StartX=117.5 StartY=9.01251 StartZ=0 EndX=121.163 EndY=9.0125 EndZ=0
    g18: ArcOfCircle CenterX=105 CenterY=19 CenterZ=0 NormalX=0 NormalY=0 NormalZ=1 AngleXU=0 Radius=20.6155 StartAngle=5.7297 EndAngle=6.28319
    g19: LineSegment StartX=121.163 StartY=9.0125 StartZ=0 EndX=122.538 EndY=8.16329 EndZ=0
    g20: LineSegment StartX=124 StartY=38 StartZ=0 EndX=125.616 EndY=38 EndZ=0
    g21: LineSegment StartX=125.616 StartY=19 StartZ=0 EndX=125.616 EndY=38 EndZ=0
  constraints (49):
    c: Vertical(g0)
    c: Block(g0)
    c: Coincident(g1,g0)
    c: Block(g1)
    c: Coincident(g2,g1)
    c: Block(g2)
    c: Coincident(g3,g2)
    c: Horizontal(g3)
    c: Tangent(g3,g2)
    c: Coincident(g4,g0)
    c: Distance(g4) = 3
    c: Vertical(g4)
    c: Coincident(g5,g4)
    c: Horizontal(g5)
    c: Coincident(g6,g2)
    c: Coincident(g6,g5)
    c: Vertical(g6)
    c: Horizontal(g7)
    c: Distance(g7) = 105
    c: Coincident(g7,g1)
    c: Block(g3)
    c: Weight(g8) = 1
    c: Equal(g8,g9)
    c: Equal(g8,g10)
    c: InternalAlignment(g8,g11)
    c: InternalAlignment(g9,g11)
    c: InternalAlignment(g10,g11)
    c: InternalAlignment(g12,g11)
    c: InternalAlignment(g13,g11)
    c: Block(g11)
    c: Coincident(g14,g11)
    c: Coincident(g14,g3)
    c: Horizontal(g14)
    c: Block(g15)
    c: Coincident(g16,g11)
    c: Coincident(g16,g15)
    c: Vertical(g16)
    c: Distance(g16) = 14
    c: Coincident(g17,g15)
    c: Block(g18)
    c: Coincident(g19,g18)
    c: Coincident(g20,g7)
    c: Horizontal(g20)
    c: Vertical(g21)
    c: Coincident(g20,g21)
    c: Block(g20)
    c: Block(g21)
    c: Block(g19)
    c: Block(g17)
FEATURE [Part::Extrusion] Extrude029
  Base = -> Sketch038
  Dir = (0,0,1)
  DirMode = 2
  FaceMakerClass = Part::FaceMakerBullseye
  LengthFwd = 72
  LengthRev = 0
  Solid = true
  Symmetric = false
FEATURE [Part::Feature] Face085
  shape: bbox 4.8 x 25.5 x 2e-07 mm, 1 faces, 0 solids (baked)
FEATURE [Part::Revolution] Revolve089  label="moreFrontCaseScrewPost003"
  Angle = 360
  Axis = (0,1,0)
  Base = (0,0,0)
  FaceMakerClass = Part::FaceMakerBullseye
  Placement = pos=(109.5,4.5,3.5) rot=(0,0,1;0rad)
  Solid = false
  Source = -> Face085
  Symmetric = false
FEATURE [Part::Feature] Face086
  shape: bbox 4.8 x 25.5 x 2e-07 mm, 1 faces, 0 solids (baked)
FEATURE [Part::Revolution] Revolve090  label="moreFrontCaseScrewPost004"
  Angle = 360
  Axis = (0,1,0)
  Base = (0,0,0)
  FaceMakerClass = Part::FaceMakerBullseye
  Placement = pos=(109.5,4.5,68.5) rot=(0,0,1;0rad)
  Solid = false
  Source = -> Face086
  Symmetric = false
FEATURE [Part::Fillet] Fillet026  label="top013"
  Base = -> Extrude029
  Edges = 1 edges r=2: [Edge35]
FEATURE [Sketcher::SketchObject] Sketch039
  FullyConstrained = true
  sketch-geometry (7):
    g0: LineSegment StartX=0 StartY=0 StartZ=0 EndX=0 EndY=6 EndZ=0
    g1: Circle CenterX=0 CenterY=0 CenterZ=0 NormalX=0 NormalY=0 NormalZ=1 AngleXU=0 Radius=1
    g2: Circle CenterX=8 CenterY=6 CenterZ=0 NormalX=0 NormalY=0 NormalZ=1 AngleXU=0 Radius=1
    g3: BSplineCurve PolesCount=3 KnotsCount=2 Degree=2 IsPeriodic=0
    g4: GeomPoint X=0 Y=0 Z=0
    g5: GeomPoint X=8 Y=6 Z=0
    g6: LineSegment StartX=0 StartY=6 StartZ=0 EndX=8 EndY=6 EndZ=0
  constraints (14):
    c: Coincident(g0,g-1)
    c: Distance(g0) = 6
    c: Vertical(g0)
    c: Coincident(g3,g0)
    c: Weight(g1) = 1
    c: Equal(g1,g2)
    c: InternalAlignment(g1,g3)
    c: InternalAlignment(g2,g3)
    c: InternalAlignment(g4,g3)
    c: InternalAlignment(g5,g3)
    c: Block(g3)
    c: Coincident(g6,g0)
    c: Coincident(g6,g3)
    c: Horizontal(g6)
FEATURE [Sketcher::SketchObject] Sketch040
  FullyConstrained = true
  sketch-geometry (7):
    g0: LineSegment StartX=0 StartY=0 StartZ=0 EndX=0 EndY=6 EndZ=0
    g1: Circle CenterX=0 CenterY=0 CenterZ=0 NormalX=0 NormalY=0 NormalZ=1 AngleXU=0 Radius=1
    g2: Circle CenterX=8 CenterY=6 CenterZ=0 NormalX=0 NormalY=0 NormalZ=1 AngleXU=0 Radius=1
    g3: BSplineCurve PolesCount=3 KnotsCount=2 Degree=2 IsPeriodic=0
    g4: GeomPoint X=0 Y=0 Z=0
    g5: GeomPoint X=8 Y=6 Z=0
    g6: LineSegment StartX=0 StartY=6 StartZ=0 EndX=8 EndY=6 EndZ=0
  constraints (14):
    c: Coincident(g0,g-1)
    c: Distance(g0) = 6
    c: Vertical(g0)
    c: Coincident(g3,g0)
    c: Weight(g1) = 1
    c: Equal(g1,g2)
    c: InternalAlignment(g1,g3)
    c: InternalAlignment(g2,g3)
    c: InternalAlignment(g4,g3)
    c: InternalAlignment(g5,g3)
    c: Block(g3)
    c: Coincident(g6,g0)
    c: Coincident(g6,g3)
    c: Horizontal(g6)
FEATURE [Sketcher::SketchObject] Sketch041
  FullyConstrained = true
  sketch-geometry (7):
    g0: LineSegment StartX=0 StartY=0 StartZ=0 EndX=0 EndY=6 EndZ=0
    g1: Circle CenterX=0 CenterY=0 CenterZ=0 NormalX=0 NormalY=0 NormalZ=1 AngleXU=0 Radius=1
    g2: Circle CenterX=8 CenterY=6 CenterZ=0 NormalX=0 NormalY=0 NormalZ=1 AngleXU=0 Radius=1
    g3: BSplineCurve PolesCount=3 KnotsCount=2 Degree=2 IsPeriodic=0
    g4: GeomPoint X=0 Y=0 Z=0
    g5: GeomPoint X=8 Y=6 Z=0
    g6: LineSegment StartX=0 StartY=6 StartZ=0 EndX=8 EndY=6 EndZ=0
  constraints (14):
    c: Coincident(g0,g-1)
    c: Distance(g0) = 6
    c: Vertical(g0)
    c: Coincident(g3,g0)
    c: Weight(g1) = 1
    c: Equal(g1,g2)
    c: InternalAlignment(g1,g3)
    c: InternalAlignment(g2,g3)
    c: InternalAlignment(g4,g3)
    c: InternalAlignment(g5,g3)
    c: Block(g3)
    c: Coincident(g6,g0)
    c: Coincident(g6,g3)
    c: Horizontal(g6)
FEATURE [Sketcher::SketchObject] Sketch042
  FullyConstrained = true
  sketch-geometry (7):
    g0: LineSegment StartX=0 StartY=0 StartZ=0 EndX=0 EndY=6 EndZ=0
    g1: Circle CenterX=0 CenterY=0 CenterZ=0 NormalX=0 NormalY=0 NormalZ=1 AngleXU=0 Radius=1
    g2: Circle CenterX=8 CenterY=6 CenterZ=0 NormalX=0 NormalY=0 NormalZ=1 AngleXU=0 Radius=1
    g3: BSplineCurve PolesCount=3 KnotsCount=2 Degree=2 IsPeriodic=0
    g4: GeomPoint X=0 Y=0 Z=0
    g5: GeomPoint X=8 Y=6 Z=0
    g6: LineSegment StartX=0 StartY=6 StartZ=0 EndX=8 EndY=6 EndZ=0
  constraints (14):
    c: Coincident(g0,g-1)
    c: Distance(g0) = 6
    c: Vertical(g0)
    c: Coincident(g3,g0)
    c: Weight(g1) = 1
    c: Equal(g1,g2)
    c: InternalAlignment(g1,g3)
    c: InternalAlignment(g2,g3)
    c: InternalAlignment(g4,g3)
    c: InternalAlignment(g5,g3)
    c: Block(g3)
    c: Coincident(g6,g0)
    c: Coincident(g6,g3)
    c: Horizontal(g6)
FEATURE [Part::Extrusion] Extrude030  label="caseScrewPillarBracket008"
  Base = -> Sketch039
  Dir = (0,0,1)
  DirMode = 2
  FaceMakerClass = Part::FaceMakerBullseye
  LengthFwd = 2.4
  LengthRev = 0
  Placement = pos=(15.76,29,8.8) rot=(0,1,0;0rad)
  Solid = true
  Symmetric = false
FEATURE [Part::Extrusion] Extrude031  label="caseScrewPillarBracket009"
  Base = -> Sketch040
  Dir = (0,0,1)
  DirMode = 2
  FaceMakerClass = Part::FaceMakerBullseye
  LengthFwd = 2.4
  LengthRev = 0
  Placement = pos=(15.76,29,60.8) rot=(0,0,1;0rad)
  Solid = true
  Symmetric = false
FEATURE [Part::Extrusion] Extrude032  label="caseScrewPillarBracket010"
  Base = -> Sketch041
  Dir = (0,0,1)
  DirMode = 2
  FaceMakerClass = Part::FaceMakerBullseye
  LengthFwd = 2.4
  LengthRev = 0
  Placement = pos=(13.7,29,13.26) rot=(0,-1,0;1.5708rad)
  Solid = true
  Symmetric = false
FEATURE [Part::Extrusion] Extrude033  label="caseScrewPillarBracket011"
  Base = -> Sketch042
  Dir = (0,0,1)
  DirMode = 2
  FaceMakerClass = Part::FaceMakerBullseye
  LengthFwd = 2.4
  LengthRev = 0
  Placement = pos=(11.3,29,58.74) rot=(0,1,0;1.5708rad)
  Solid = true
  Symmetric = false
FEATURE [Sketcher::SketchObject] Sketch043
  FullyConstrained = true
  sketch-geometry (7):
    g0: LineSegment StartX=0 StartY=0 StartZ=0 EndX=0 EndY=6 EndZ=0
    g1: Circle CenterX=0 CenterY=0 CenterZ=0 NormalX=0 NormalY=0 NormalZ=1 AngleXU=0 Radius=1
    g2: Circle CenterX=8 CenterY=6 CenterZ=0 NormalX=0 NormalY=0 NormalZ=1 AngleXU=0 Radius=1
    g3: BSplineCurve PolesCount=3 KnotsCount=2 Degree=2 IsPeriodic=0
    g4: GeomPoint X=0 Y=0 Z=0
    g5: GeomPoint X=8 Y=6 Z=0
    g6: LineSegment StartX=0 StartY=6 StartZ=0 EndX=8 EndY=6 EndZ=0
  constraints (14):
    c: Coincident(g0,g-1)
    c: Distance(g0) = 6
    c: Vertical(g0)
    c: Coincident(g3,g0)
    c: Weight(g1) = 1
    c: Equal(g1,g2)
    c: InternalAlignment(g1,g3)
    c: InternalAlignment(g2,g3)
    c: InternalAlignment(g4,g3)
    c: InternalAlignment(g5,g3)
    c: Block(g3)
    c: Coincident(g6,g0)
    c: Coincident(g6,g3)
    c: Horizontal(g6)
FEATURE [Part::Extrusion] Extrude034  label="caseScrewPillarBracket012"
  Base = -> Sketch043
  Dir = (0,0,1)
  DirMode = 2
  FaceMakerClass = Part::FaceMakerBullseye
  LengthFwd = 2.4
  LengthRev = 0
  Placement = pos=(88.3,29,65.23) rot=(0,1,0;1.5708rad)
  Solid = true
  Symmetric = false
FEATURE [Sketcher::SketchObject] Sketch044
  FullyConstrained = true
  sketch-geometry (7):
    g0: LineSegment StartX=0 StartY=0 StartZ=0 EndX=0 EndY=6 EndZ=0
    g1: Circle CenterX=0 CenterY=0 CenterZ=0 NormalX=0 NormalY=0 NormalZ=1 AngleXU=0 Radius=1
    g2: Circle CenterX=8 CenterY=6 CenterZ=0 NormalX=0 NormalY=0 NormalZ=1 AngleXU=0 Radius=1
    g3: BSplineCurve PolesCount=3 KnotsCount=2 Degree=2 IsPeriodic=0
    g4: GeomPoint X=0 Y=0 Z=0
    g5: GeomPoint X=8 Y=6 Z=0
    g6: LineSegment StartX=0 StartY=6 StartZ=0 EndX=8 EndY=6 EndZ=0
  constraints (14):
    c: Coincident(g0,g-1)
    c: Distance(g0) = 6
    c: Vertical(g0)
    c: Coincident(g3,g0)
    c: Weight(g1) = 1
    c: Equal(g1,g2)
    c: InternalAlignment(g1,g3)
    c: InternalAlignment(g2,g3)
    c: InternalAlignment(g4,g3)
    c: InternalAlignment(g5,g3)
    c: Block(g3)
    c: Coincident(g6,g0)
    c: Coincident(g6,g3)
    c: Horizontal(g6)
FEATURE [Part::Extrusion] Extrude035  label="caseScrewPillarBracket013"
  Base = -> Sketch044
  Dir = (0,0,1)
  DirMode = 2
  FaceMakerClass = Part::FaceMakerBullseye
  LengthFwd = 2.4
  LengthRev = 0
  Placement = pos=(90.7,29,6.77) rot=(0,-1,0;1.5708rad)
  Solid = true
  Symmetric = false
FEATURE [Sketcher::SketchObject] Sketch045
  FullyConstrained = true
  sketch-geometry (7):
    g0: LineSegment StartX=0 StartY=0 StartZ=0 EndX=0 EndY=6 EndZ=0
    g1: Circle CenterX=0 CenterY=0 CenterZ=0 NormalX=0 NormalY=0 NormalZ=1 AngleXU=0 Radius=1
    g2: Circle CenterX=8 CenterY=6 CenterZ=0 NormalX=0 NormalY=0 NormalZ=1 AngleXU=0 Radius=1
    g3: BSplineCurve PolesCount=3 KnotsCount=2 Degree=2 IsPeriodic=0
    g4: GeomPoint X=0 Y=0 Z=0
    g5: GeomPoint X=8 Y=6 Z=0
    g6: LineSegment StartX=0 StartY=6 StartZ=0 EndX=8 EndY=6 EndZ=0
  constraints (14):
    c: Coincident(g0,g-1)
    c: Distance(g0) = 6
    c: Vertical(g0)
    c: Coincident(g3,g0)
    c: Weight(g1) = 1
    c: Equal(g1,g2)
    c: InternalAlignment(g1,g3)
    c: InternalAlignment(g2,g3)
    c: InternalAlignment(g4,g3)
    c: InternalAlignment(g5,g3)
    c: Block(g3)
    c: Coincident(g6,g0)
    c: Coincident(g6,g3)
    c: Horizontal(g6)
FEATURE [Sketcher::SketchObject] Sketch046
  FullyConstrained = true
  sketch-geometry (7):
    g0: LineSegment StartX=0 StartY=0 StartZ=0 EndX=0 EndY=6 EndZ=0
    g1: Circle CenterX=0 CenterY=0 CenterZ=0 NormalX=0 NormalY=0 NormalZ=1 AngleXU=0 Radius=1
    g2: Circle CenterX=8 CenterY=6 CenterZ=0 NormalX=0 NormalY=0 NormalZ=1 AngleXU=0 Radius=1
    g3: BSplineCurve PolesCount=3 KnotsCount=2 Degree=2 IsPeriodic=0
    g4: GeomPoint X=0 Y=0 Z=0
    g5: GeomPoint X=8 Y=6 Z=0
    g6: LineSegment StartX=0 StartY=6 StartZ=0 EndX=8 EndY=6 EndZ=0
  constraints (14):
    c: Coincident(g0,g-1)
    c: Distance(g0) = 6
    c: Vertical(g0)
    c: Coincident(g3,g0)
    c: Weight(g1) = 1
    c: Equal(g1,g2)
    c: InternalAlignment(g1,g3)
    c: InternalAlignment(g2,g3)
    c: InternalAlignment(g4,g3)
    c: InternalAlignment(g5,g3)
    c: Block(g3)
    c: Coincident(g6,g0)
    c: Coincident(g6,g3)
    c: Horizontal(g6)
FEATURE [Part::Extrusion] Extrude036  label="caseScrewPillarBracket014"
  Base = -> Sketch045
  Dir = (0,0,1)
  DirMode = 2
  FaceMakerClass = Part::FaceMakerBullseye
  LengthFwd = 2.4
  LengthRev = 0
  Placement = pos=(110.7,29,6.77) rot=(0,-1,0;1.5708rad)
  Solid = true
  Symmetric = false
FEATURE [Part::Extrusion] Extrude037  label="caseScrewPillarBracket015"
  Base = -> Sketch046
  Dir = (0,0,1)
  DirMode = 2
  FaceMakerClass = Part::FaceMakerBullseye
  LengthFwd = 2.4
  LengthRev = 0
  Placement = pos=(108.3,29,65.23) rot=(0,1,0;1.5708rad)
  Solid = true
  Symmetric = false
FEATURE [Part::Box] Box013  label="frontCaseScrewPillarBracket002"
  AttacherType = Attacher::AttachEngine3D
  Height = 2.4
  Length = 22
  Placement = pos=(87,28,2.3) rot=(0,0,1;0rad)
  Width = 7
FEATURE [Part::Box] Box014  label="frontCaseScrewPillarBracket003"
  AttacherType = Attacher::AttachEngine3D
  Height = 2.4
  Length = 22
  Placement = pos=(87,28,67.3) rot=(0,0,1;0rad)
  Width = 7
FEATURE [Part::Feature] Face087
  shape: bbox 4.8 x 30.2 x 2e-07 mm, 1 faces, 0 solids (baked)
FEATURE [Part::Revolution] Revolve091  label="frontCaseScrewPost004"
  Angle = 360
  Axis = (0,1,0)
  Base = (0,0,0)
  FaceMakerClass = Part::FaceMakerBullseye
  Placement = pos=(89.5,4.5,3.5) rot=(0,0,1;0rad)
  Solid = false
  Source = -> Face087
  Symmetric = false
FEATURE [Part::Feature] Face088
  shape: bbox 4.8 x 30.2 x 2e-07 mm, 1 faces, 0 solids (baked)
FEATURE [Part::Revolution] Revolve092  label="frontCaseScrewPost005"
  Angle = 360
  Axis = (0,1,0)
  Base = (0,0,0)
  FaceMakerClass = Part::FaceMakerBullseye
  Placement = pos=(89.5,4.5,68.5) rot=(0,0,1;0rad)
  Solid = false
  Source = -> Face088
  Symmetric = false
FEATURE [Part::Feature] Face089
  shape: bbox 3.5 x 30.2 x 2e-07 mm, 1 faces, 0 solids (baked)
FEATURE [Part::Revolution] Revolve093  label="backCaseScrewPost002"
  Angle = 360
  Axis = (0,1,0)
  Base = (0,0,0)
  FaceMakerClass = Part::FaceMakerBullseye
  Placement = pos=(12.5,4.5,10) rot=(0,0,1;0rad)
  Solid = false
  Source = -> Face089
  Symmetric = false
FEATURE [Part::Feature] Face090
  shape: bbox 3.5 x 30.2 x 2e-07 mm, 1 faces, 0 solids (baked)
FEATURE [Part::Revolution] Revolve094  label="backCaseScrewPost003"
  Angle = 360
  Axis = (0,1,0)
  Base = (0,0,0)
  FaceMakerClass = Part::FaceMakerBullseye
  Placement = pos=(12.5,4.5,62) rot=(0,0,1;0rad)
  Solid = false
  Source = -> Face090
  Symmetric = false
FEATURE [Part::Box] Box015  label="Cube011"
  AttacherType = Attacher::AttachEngine3D
  Height = 28.8
  Length = 3
  Placement = pos=(107.3,28,21.6) rot=(0,0,1;0rad)
  Width = 7
FEATURE [Part::Box] Box016  label="Cube012"
  AttacherType = Attacher::AttachEngine3D
  Height = 3
  Length = 7.4
  Placement = pos=(107.3,28,18.6) rot=(0,0,1;0rad)
  Width = 7
FEATURE [Part::Box] Box017  label="Cube013"
  AttacherType = Attacher::AttachEngine3D
  Height = 3
  Length = 7.4
  Placement = pos=(107.3,28,50.4) rot=(0,0,1;0rad)
  Width = 7
FEATURE [Part::Cylinder] Cylinder024
  Angle = 360
  AttacherType = Attacher::AttachEngine3D
  Height = 20
  Placement = pos=(0,0,36.15) rot=(0,0,1;0rad)
  Radius = 14.3
FEATURE [Part::Cylinder] Cylinder025
  Angle = 360
  AttacherType = Attacher::AttachEngine3D
  Height = 10
  Placement = pos=(0,0,36.15) rot=(0,0,1;0rad)
  Radius = 4
FEATURE [Part::MultiFuse] Fusion066  label="removeToCreteHoleForPlugHousing009"
  Placement = pos=(70,19,36) rot=(0,1,0;1.5708rad)
  Shapes = -> [Cylinder024,Cylinder025]
FEATURE [Part::MultiFuse] Fusion065  label="plugHousingBracketHolder002"
  Shapes = -> [Box017,Box015,Box016]
FEATURE [Part::Cut] Cut025  label="plugHousingBracketHolder003"
  Base = -> Fusion065
  Placement = pos=(7,0,0) rot=(0,0,1;0rad)
  Tool = -> Fusion066
FEATURE [Sketcher::SketchObject] Sketch047
  FullyConstrained = false
  Placement = pos=(0,0,0) rot=(1,0,0;1.5708rad)
  sketch-geometry (24):
    g0: ArcOfCircle CenterX=-4 CenterY=-10.5 CenterZ=0 NormalX=0 NormalY=0 NormalZ=1 AngleXU=0 Radius=1.5 StartAngle=6e-16 EndAngle=3.14159
    g1: ArcOfCircle CenterX=-34.2 CenterY=-10.5 CenterZ=0 NormalX=0 NormalY=0 NormalZ=1 AngleXU=0 Radius=1.5 StartAngle=0 EndAngle=3.14159
    g2: ArcOfCircle CenterX=-34.2 CenterY=-27.7 CenterZ=0 NormalX=0 NormalY=0 NormalZ=1 AngleXU=0 Radius=1.5 StartAngle=3.14159 EndAngle=6.28319
    g3: ArcOfCircle CenterX=-4 CenterY=-27.7 CenterZ=0 NormalX=0 NormalY=0 NormalZ=1 AngleXU=0 Radius=1.5 StartAngle=3.1416 EndAngle=6.28319
    g4: ArcOfCircle CenterX=-10 CenterY=-4.3 CenterZ=0 NormalX=0 NormalY=0 NormalZ=1 AngleXU=0 Radius=1.5 StartAngle=2e-16 EndAngle=3.14159
    g5: ArcOfCircle CenterX=-16.1 CenterY=-1.8 CenterZ=0 NormalX=0 NormalY=0 NormalZ=1 AngleXU=0 Radius=1.5 StartAngle=5e-16 EndAngle=3.14159
    g6: ArcOfCircle CenterX=-22.1 CenterY=-1.8 CenterZ=0 NormalX=0 NormalY=0 NormalZ=1 AngleXU=0 Radius=1.5 StartAngle=5e-16 EndAngle=3.14159
    g7: ArcOfCircle CenterX=-28.2 CenterY=-4.3 CenterZ=0 NormalX=0 NormalY=0 NormalZ=1 AngleXU=0 Radius=1.5 StartAngle=2e-16 EndAngle=3.14159
    g8: ArcOfCircle CenterX=-10 CenterY=-33.9 CenterZ=0 NormalX=0 NormalY=0 NormalZ=1 AngleXU=0 Radius=1.5 StartAngle=3.14159 EndAngle=6.28319
    g9: ArcOfCircle CenterX=-16.1 CenterY=-36.4 CenterZ=0 NormalX=0 NormalY=0 NormalZ=1 AngleXU=0 Radius=1.5 StartAngle=3.14159 EndAngle=6.28319
    g10: ArcOfCircle CenterX=-22.1 CenterY=-36.4 CenterZ=0 NormalX=0 NormalY=0 NormalZ=1 AngleXU=0 Radius=1.5 StartAngle=3.14159 EndAngle=6.28319
    g11: ArcOfCircle CenterX=-28.2 CenterY=-33.9 CenterZ=0 NormalX=0 NormalY=0 NormalZ=1 AngleXU=0 Radius=1.5 StartAngle=3.14159 EndAngle=6.28319
    g12: LineSegment StartX=-35.7 StartY=-10.5 StartZ=0 EndX=-35.7 EndY=-27.7 EndZ=0
    g13: LineSegment StartX=-32.7 StartY=-10.5 StartZ=0 EndX=-32.7 EndY=-27.7 EndZ=0
    g14: LineSegment StartX=-29.7 StartY=-33.9 StartZ=0 EndX=-29.7 EndY=-4.3 EndZ=0
    g15: LineSegment StartX=-26.7 StartY=-33.9 StartZ=0 EndX=-26.7 EndY=-4.3 EndZ=0
    g16: LineSegment StartX=-2.5 StartY=-10.5 StartZ=0 EndX=-2.5 EndY=-27.7 EndZ=0
    g17: LineSegment StartX=-8.5 StartY=-4.3 StartZ=0 EndX=-8.5 EndY=-33.9 EndZ=0
    g18: LineSegment StartX=-5.5 StartY=-10.5 StartZ=0 EndX=-5.5 EndY=-27.7 EndZ=0
    g19: LineSegment StartX=-11.5 StartY=-4.3 StartZ=0 EndX=-11.5 EndY=-33.9 EndZ=0
    g20: LineSegment StartX=-14.6 StartY=-1.8 StartZ=0 EndX=-14.6 EndY=-36.4 EndZ=0
    g21: LineSegment StartX=-17.6 StartY=-1.8 StartZ=0 EndX=-17.6 EndY=-36.4 EndZ=0
    g22: LineSegment StartX=-20.6 StartY=-36.4 StartZ=0 EndX=-20.6 EndY=-1.8 EndZ=0
    g23: LineSegment StartX=-23.6 StartY=-1.8 StartZ=0 EndX=-23.6 EndY=-36.4 EndZ=0
  constraints (48):
    c: Block(g0)
    c: Block(g1)
    c: Block(g2)
    c: Block(g3)
    c: Block(g4)
    c: Block(g5)
    c: Block(g6)
    c: Block(g7)
    c: Block(g8)
    c: Block(g9)
    c: Block(g10)
    c: Block(g11)
    c: Coincident(g12,g1)
    c: Coincident(g12,g2)
    c: Vertical(g12)
    c: Coincident(g13,g1)
    c: Coincident(g13,g2)
    c: Vertical(g13)
    c: Coincident(g14,g11)
    c: Coincident(g14,g7)
    c: Vertical(g14)
    c: Coincident(g15,g11)
    c: Coincident(g15,g7)
    c: Vertical(g15)
    c: Coincident(g16,g0)
    c: Coincident(g16,g3)
    c: Vertical(g16)
    c: Coincident(g17,g4)
    c: Coincident(g17,g8)
    c: Vertical(g17)
    c: Coincident(g18,g0)
    c: Coincident(g18,g3)
    c: Vertical(g18)
    c: Coincident(g19,g4)
    c: Coincident(g19,g8)
    c: Vertical(g19)
    c: Coincident(g20,g5)
    c: Coincident(g20,g9)
    c: Vertical(g20)
    c: Coincident(g21,g5)
    c: Coincident(g21,g9)
    c: Vertical(g21)
    c: Coincident(g22,g10)
    c: Coincident(g22,g6)
    c: Vertical(g22)
    c: Coincident(g23,g6)
    c: Coincident(g23,g10)
    c: Vertical(g23)
FEATURE [Part::Extrusion] Extrude038  label="removeToCreateFanGrillHoles001"
  Base = -> Sketch047
  Dir = (0,-1,6e-16)
  DirMode = 2
  FaceMakerClass = Part::FaceMakerBullseye
  LengthFwd = 10
  LengthRev = 0
  Placement = pos=(65.4,44,54.82) rot=(0,0,1;0rad)
  Solid = true
  Symmetric = false
FEATURE [Part::Feature] Wire004
  shape: bbox 11 x 5.2 x 2e-07 mm, 0 faces, 0 solids (baked)
FEATURE [Part::Revolution] Revolve095
  Angle = 360
  Axis = (0,1,0)
  Base = (0,0,0)
  FaceMakerClass = Part::FaceMakerBullseye
  Placement = pos=(30.3,38,19.7) rot=(0,0,1;0rad)
  Solid = true
  Source = -> Wire004
  Symmetric = false
FEATURE [Part::Feature] Wire005
  shape: bbox 11 x 5.2 x 2e-07 mm, 0 faces, 0 solids (baked)
FEATURE [Part::Revolution] Revolve096
  Angle = 360
  Axis = (0,1,0)
  Base = (0,0,0)
  FaceMakerClass = Part::FaceMakerBullseye
  Placement = pos=(30.3,38,51.7) rot=(0,0,1;0rad)
  Solid = true
  Source = -> Wire005
  Symmetric = false
FEATURE [Part::Feature] Wire006
  shape: bbox 11 x 5.2 x 2e-07 mm, 0 faces, 0 solids (baked)
FEATURE [Part::Revolution] Revolve097
  Angle = 360
  Axis = (0,1,0)
  Base = (0,0,0)
  FaceMakerClass = Part::FaceMakerBullseye
  Placement = pos=(62.3,38,51.7) rot=(0,0,1;0rad)
  Solid = true
  Source = -> Wire006
  Symmetric = false
FEATURE [Part::Feature] Wire007
  shape: bbox 11 x 5.2 x 2e-07 mm, 0 faces, 0 solids (baked)
FEATURE [Part::Revolution] Revolve098
  Angle = 360
  Axis = (0,1,0)
  Base = (0,0,0)
  FaceMakerClass = Part::FaceMakerBullseye
  Placement = pos=(62.3,38,19.7) rot=(0,0,1;0rad)
  Solid = true
  Source = -> Wire007
  Symmetric = false
FEATURE [Part::MultiFuse] Fusion067  label="fanScrewHousing002"
  Shapes = -> [Revolve098,Revolve097,Revolve096,Revolve095]
FEATURE [Part::Feature] Face091 .. Face094  x4 (patterned run collapsed; names and placements below)
  shape: bbox 3.5 x 17.8 x 2e-07 mm, 1 faces, 0 solids (baked)
FEATURE [Part::Revolution] Revolve099  label="removeToCreateScrewAndThreadedInsertHole026"
  Angle = 360
  Axis = (0,1,0)
  Base = (0,0,0)
  FaceMakerClass = Part::FaceMakerBullseye
  Placement = pos=(62.3,30.3,19.7) rot=(0,0,1;0rad)
  Solid = false
  Source = -> Face091
  Symmetric = false
FEATURE [Part::Revolution] Revolve100  label="removeToCreateScrewAndThreadedInsertHole027"
  Angle = 360
  Axis = (0,1,0)
  Base = (0,0,0)
  FaceMakerClass = Part::FaceMakerBullseye
  Placement = pos=(62.3,30.3,51.7) rot=(0,0,1;0rad)
  Solid = false
  Source = -> Face092
  Symmetric = false
FEATURE [Part::Revolution] Revolve101  label="removeToCreateScrewAndThreadedInsertHole028"
  Angle = 360
  Axis = (0,1,0)
  Base = (0,0,0)
  FaceMakerClass = Part::FaceMakerBullseye
  Placement = pos=(30.3,30.3,19.7) rot=(0,0,1;0rad)
  Solid = false
  Source = -> Face093
  Symmetric = false
FEATURE [Part::Revolution] Revolve102  label="removeToCreateScrewAndThreadedInsertHole029"
  Angle = 360
  Axis = (0,1,0)
  Base = (0,0,0)
  FaceMakerClass = Part::FaceMakerBullseye
  Placement = pos=(30.3,30.3,51.7) rot=(0,0,1;0rad)
  Solid = false
  Source = -> Face094
  Symmetric = false
FEATURE [Part::MultiFuse] Fusion068  label="createThreadedInsertHolesForFan002"
  Shapes = -> [Revolve099,Revolve100,Revolve101,Revolve102]
FEATURE [Part::Cut] Cut026  label="fanScrewHousing003"
  Base = -> Fusion067
  Tool = -> Fusion068
FEATURE [Sketcher::SketchObject] Sketch048
  FullyConstrained = false
  Placement = pos=(0,0,0) rot=(1,0,0;1.5708rad)
  sketch-geometry (24):
    g0: ArcOfCircle CenterX=-4 CenterY=-10.5 CenterZ=0 NormalX=0 NormalY=0 NormalZ=1 AngleXU=0 Radius=1.5 StartAngle=6e-16 EndAngle=3.14159
    g1: ArcOfCircle CenterX=-34.2 CenterY=-10.5 CenterZ=0 NormalX=0 NormalY=0 NormalZ=1 AngleXU=0 Radius=1.5 StartAngle=0 EndAngle=3.14159
    g2: ArcOfCircle CenterX=-34.2 CenterY=-27.7 CenterZ=0 NormalX=0 NormalY=0 NormalZ=1 AngleXU=0 Radius=1.5 StartAngle=3.14159 EndAngle=6.28319
    g3: ArcOfCircle CenterX=-4 CenterY=-27.7 CenterZ=0 NormalX=0 NormalY=0 NormalZ=1 AngleXU=0 Radius=1.5 StartAngle=3.1416 EndAngle=6.28319
    g4: ArcOfCircle CenterX=-10 CenterY=-4.3 CenterZ=0 NormalX=0 NormalY=0 NormalZ=1 AngleXU=0 Radius=1.5 StartAngle=2e-16 EndAngle=3.14159
    g5: ArcOfCircle CenterX=-16.1 CenterY=-1.8 CenterZ=0 NormalX=0 NormalY=0 NormalZ=1 AngleXU=0 Radius=1.5 StartAngle=5e-16 EndAngle=3.14159
    g6: ArcOfCircle CenterX=-22.1 CenterY=-1.8 CenterZ=0 NormalX=0 NormalY=0 NormalZ=1 AngleXU=0 Radius=1.5 StartAngle=5e-16 EndAngle=3.14159
    g7: ArcOfCircle CenterX=-28.2 CenterY=-4.3 CenterZ=0 NormalX=0 NormalY=0 NormalZ=1 AngleXU=0 Radius=1.5 StartAngle=2e-16 EndAngle=3.14159
    g8: ArcOfCircle CenterX=-10 CenterY=-33.9 CenterZ=0 NormalX=0 NormalY=0 NormalZ=1 AngleXU=0 Radius=1.5 StartAngle=3.14159 EndAngle=6.28319
    g9: ArcOfCircle CenterX=-16.1 CenterY=-36.4 CenterZ=0 NormalX=0 NormalY=0 NormalZ=1 AngleXU=0 Radius=1.5 StartAngle=3.14159 EndAngle=6.28319
    g10: ArcOfCircle CenterX=-22.1 CenterY=-36.4 CenterZ=0 NormalX=0 NormalY=0 NormalZ=1 AngleXU=0 Radius=1.5 StartAngle=3.14159 EndAngle=6.28319
    g11: ArcOfCircle CenterX=-28.2 CenterY=-33.9 CenterZ=0 NormalX=0 NormalY=0 NormalZ=1 AngleXU=0 Radius=1.5 StartAngle=3.14159 EndAngle=6.28319
    g12: LineSegment StartX=-35.7 StartY=-10.5 StartZ=0 EndX=-35.7 EndY=-27.7 EndZ=0
    g13: LineSegment StartX=-32.7 StartY=-10.5 StartZ=0 EndX=-32.7 EndY=-27.7 EndZ=0
    g14: LineSegment StartX=-29.7 StartY=-33.9 StartZ=0 EndX=-29.7 EndY=-4.3 EndZ=0
    g15: LineSegment StartX=-26.7 StartY=-33.9 StartZ=0 EndX=-26.7 EndY=-4.3 EndZ=0
    g16: LineSegment StartX=-2.5 StartY=-10.5 StartZ=0 EndX=-2.5 EndY=-27.7 EndZ=0
    g17: LineSegment StartX=-8.5 StartY=-4.3 StartZ=0 EndX=-8.5 EndY=-33.9 EndZ=0
    g18: LineSegment StartX=-5.5 StartY=-10.5 StartZ=0 EndX=-5.5 EndY=-27.7 EndZ=0
    g19: LineSegment StartX=-11.5 StartY=-4.3 StartZ=0 EndX=-11.5 EndY=-33.9 EndZ=0
    g20: LineSegment StartX=-14.6 StartY=-1.8 StartZ=0 EndX=-14.6 EndY=-36.4 EndZ=0
    g21: LineSegment StartX=-17.6 StartY=-1.8 StartZ=0 EndX=-17.6 EndY=-36.4 EndZ=0
    g22: LineSegment StartX=-20.6 StartY=-36.4 StartZ=0 EndX=-20.6 EndY=-1.8 EndZ=0
    g23: LineSegment StartX=-23.6 StartY=-1.8 StartZ=0 EndX=-23.6 EndY=-36.4 EndZ=0
  constraints (48):
    c: Block(g0)
    c: Block(g1)
    c: Block(g2)
    c: Block(g3)
    c: Block(g4)
    c: Block(g5)
    c: Block(g6)
    c: Block(g7)
    c: Block(g8)
    c: Block(g9)
    c: Block(g10)
    c: Block(g11)
    c: Coincident(g12,g1)
    c: Coincident(g12,g2)
    c: Vertical(g12)
    c: Coincident(g13,g1)
    c: Coincident(g13,g2)
    c: Vertical(g13)
    c: Coincident(g14,g11)
    c: Coincident(g14,g7)
    c: Vertical(g14)
    c: Coincident(g15,g11)
    c: Coincident(g15,g7)
    c: Vertical(g15)
    c: Coincident(g16,g0)
    c: Coincident(g16,g3)
    c: Vertical(g16)
    c: Coincident(g17,g4)
    c: Coincident(g17,g8)
    c: Vertical(g17)
    c: Coincident(g18,g0)
    c: Coincident(g18,g3)
    c: Vertical(g18)
    c: Coincident(g19,g4)
    c: Coincident(g19,g8)
    c: Vertical(g19)
    c: Coincident(g20,g5)
    c: Coincident(g20,g9)
    c: Vertical(g20)
    c: Coincident(g21,g5)
    c: Coincident(g21,g9)
    c: Vertical(g21)
    c: Coincident(g22,g10)
    c: Coincident(g22,g6)
    c: Vertical(g22)
    c: Coincident(g23,g6)
    c: Coincident(g23,g10)
    c: Vertical(g23)
FEATURE [Part::Extrusion] Extrude039  label="removeToCreateFanGrillHoles002"
  Base = -> Sketch048
  Dir = (0,-1,6e-16)
  DirMode = 2
  FaceMakerClass = Part::FaceMakerBullseye
  LengthFwd = 10
  LengthRev = 0
  Placement = pos=(65.4,44,54.82) rot=(0,0,1;0rad)
  Solid = true
  Symmetric = false
FEATURE [Part::Cut] Cut027  label="fanScrewHousing004"
  Base = -> Cut026
  Tool = -> Extrude038
FEATURE [Part::Cut] Cut028  label="top014"
  Base = -> Fillet026
  Tool = -> Extrude039
FEATURE [Part::Feature] Face095 .. Face098  x4 (patterned run collapsed; names and placements below)
  shape: bbox 3.5 x 17.8 x 2e-07 mm, 1 faces, 0 solids (baked)
FEATURE [Part::Revolution] Revolve103  label="removeToCreateScrewAndThreadedInsertHole030"
  Angle = 360
  Axis = (0,1,0)
  Base = (0,0,0)
  FaceMakerClass = Part::FaceMakerBullseye
  Placement = pos=(62.3,30.3,19.7) rot=(0,0,1;0rad)
  Solid = false
  Source = -> Face095
  Symmetric = false
FEATURE [Part::Revolution] Revolve104  label="removeToCreateScrewAndThreadedInsertHole031"
  Angle = 360
  Axis = (0,1,0)
  Base = (0,0,0)
  FaceMakerClass = Part::FaceMakerBullseye
  Placement = pos=(62.3,30.3,51.7) rot=(0,0,1;0rad)
  Solid = false
  Source = -> Face096
  Symmetric = false
FEATURE [Part::Revolution] Revolve105  label="removeToCreateScrewAndThreadedInsertHole032"
  Angle = 360
  Axis = (0,1,0)
  Base = (0,0,0)
  FaceMakerClass = Part::FaceMakerBullseye
  Placement = pos=(30.3,30.3,19.7) rot=(0,0,1;0rad)
  Solid = false
  Source = -> Face097
  Symmetric = false
FEATURE [Part::Revolution] Revolve106  label="removeToCreateScrewAndThreadedInsertHole033"
  Angle = 360
  Axis = (0,1,0)
  Base = (0,0,0)
  FaceMakerClass = Part::FaceMakerBullseye
  Placement = pos=(30.3,30.3,51.7) rot=(0,0,1;0rad)
  Solid = false
  Source = -> Face098
  Symmetric = false
FEATURE [Part::MultiFuse] Fusion069  label="createThreadedInsertHolesForFan003"
  Shapes = -> [Revolve103,Revolve104,Revolve105,Revolve106]
FEATURE [Part::Cut] Cut029  label="top015"
  Base = -> Cut028
  Tool = -> Fusion054
FEATURE [Part::Cut] Cut030  label="fanScrewHousing005"
  Base = -> Cut027
  Tool = -> Fusion069
FEATURE [Part::Cylinder] Cylinder026  label="removeToCreteHoleForPlugHousing010"
  Angle = 360
  AttacherType = Attacher::AttachEngine3D
  Height = 20
  Placement = pos=(-2,19,36) rot=(0,1,0;1.5708rad)
  Radius = 14.3
FEATURE [Part::Box] Box018  label="removeToCreteHoleForPlugHousing011"
  AttacherType = Attacher::AttachEngine3D
  Height = 28.6
  Length = 10
  Placement = pos=(-2,0,21.7) rot=(0,0,1;0rad)
  Width = 19
FEATURE [Part::Box] Box019  label="wireHolderBottomCaseBit"
  AttacherType = Attacher::AttachEngine3D
  Height = 28
  Length = 3
  Placement = pos=(0,0,22) rot=(0,0,1;0rad)
  Width = 21
FEATURE [Part::Cylinder] Cylinder027  label="removeToCreteHoleForPlugHousing012"
  Angle = 360
  AttacherType = Attacher::AttachEngine3D
  Height = 20
  Placement = pos=(-2,19,36) rot=(0,1,0;1.5708rad)
  Radius = 14.3
FEATURE [Part::Cut] Cut031  label="wireHolderBottomCaseBit001"
  Base = -> Box019
  Tool = -> Cylinder027
FEATURE [Part::MultiFuse] Fusion070  label="removeToCreteHoleForPlugHousing013"
  Shapes = -> [Box018,Cylinder026]
FEATURE [Part::Cut] Cut032  label="top016"
  Base = -> Cut029
  Tool = -> Fusion070
FEATURE [Part::Cylinder] Cylinder028
  Angle = 360
  AttacherType = Attacher::AttachEngine3D
  Height = 20
  Placement = pos=(0,0,36.15) rot=(0,0,1;0rad)
  Radius = 14.3
FEATURE [Part::Cylinder] Cylinder029
  Angle = 360
  AttacherType = Attacher::AttachEngine3D
  Height = 10
  Placement = pos=(0,0,36.15) rot=(0,0,1;0rad)
  Radius = 4
FEATURE [Part::MultiFuse] Fusion071  label="removeToCreteHoleForPlugHousing014"
  Placement = pos=(70,19,36) rot=(0,1,0;1.5708rad)
  Shapes = -> [Cylinder028,Cylinder029]
FEATURE [Sketcher::SketchObject] Sketch049  label="topSketch011"
  FullyConstrained = true
  sketch-geometry (4):
    g0: ArcOfCircle CenterX=105 CenterY=19 CenterZ=0 NormalX=0 NormalY=0 NormalZ=1 AngleXU=0 Radius=20.6155 StartAngle=5.54125 EndAngle=6.28319
    g1: ArcOfCircle CenterX=105 CenterY=19 CenterZ=0 NormalX=0 NormalY=0 NormalZ=1 AngleXU=0 Radius=13 StartAngle=5.54125 EndAngle=6.28319
    g2: LineSegment StartX=118 StartY=19 StartZ=0 EndX=125.616 EndY=19 EndZ=0
    g3: LineSegment StartX=114.583 StartY=10.2157 StartZ=0 EndX=120.197 EndY=5.06982 EndZ=0
  constraints (7):
    c: Block(g0)
    c: Block(g1)
    c: Coincident(g2,g1)
    c: Coincident(g2,g0)
    c: Horizontal(g2)
    c: Coincident(g3,g1)
    c: Coincident(g3,g0)
FEATURE [Part::Box] Box020  label="removeToCreteHoleForPlugHousing015"
  AttacherType = Attacher::AttachEngine3D
  Height = 28.6
  Length = 20
  Placement = pos=(106.15,0,21.7) rot=(0,0,1;0rad)
  Width = 19
FEATURE [Part::MultiFuse] Fusion072  label="removeToCreteHoleForPlugHousing016"
  Shapes = -> [Box020,Fusion071]
FEATURE [Part::Cut] Cut033  label="removeToCreteHoleForPlugHousing017"
  Base = -> Cut032
  Tool = -> Fusion072
FEATURE [Part::Cylinder] Cylinder030
  Angle = 360
  AttacherType = Attacher::AttachEngine3D
  Height = 20
  Placement = pos=(0,0,36.15) rot=(0,0,1;0rad)
  Radius = 14.3
FEATURE [Part::Cylinder] Cylinder031
  Angle = 360
  AttacherType = Attacher::AttachEngine3D
  Height = 10
  Placement = pos=(0,0,36.15) rot=(0,0,1;0rad)
  Radius = 4
FEATURE [Part::Box] Box021  label="removeToCreteHoleForPlugHousing019"
  AttacherType = Attacher::AttachEngine3D
  Height = 28.6
  Length = 20
  Placement = pos=(106.15,0,21.7) rot=(0,0,1;0rad)
  Width = 19
FEATURE [Part::MultiFuse] Fusion074  label="removeToCreteHoleForPlugHousing020"
  Placement = pos=(70,19,36) rot=(0,1,0;1.5708rad)
  Shapes = -> [Cylinder030,Cylinder031]
FEATURE [Part::MultiFuse] Fusion073  label="removeToCreteHoleForPlugHousing018"
  Placement = pos=(0,0,28.3) rot=(0,0,1;0rad)
  Shapes = -> [Box021,Fusion074]
FEATURE [Part::Cylinder] Cylinder032
  Angle = 360
  AttacherType = Attacher::AttachEngine3D
  Height = 20
  Placement = pos=(0,0,36.15) rot=(0,0,1;0rad)
  Radius = 14.3
FEATURE [Part::Cylinder] Cylinder033
  Angle = 360
  AttacherType = Attacher::AttachEngine3D
  Height = 10
  Placement = pos=(0,0,36.15) rot=(0,0,1;0rad)
  Radius = 4
FEATURE [Part::Box] Box022  label="removeToCreteHoleForPlugHousing021"
  AttacherType = Attacher::AttachEngine3D
  Height = 28.6
  Length = 20
  Placement = pos=(106.15,0,21.7) rot=(0,0,1;0rad)
  Width = 19
FEATURE [Part::MultiFuse] Fusion076  label="removeToCreteHoleForPlugHousing023"
  Placement = pos=(70,19,36) rot=(0,1,0;1.5708rad)
  Shapes = -> [Cylinder032,Cylinder033]
FEATURE [Part::MultiFuse] Fusion075  label="removeToCreteHoleForPlugHousing022"
  Placement = pos=(0,0,-28.3) rot=(0,0,1;0rad)
  Shapes = -> [Box022,Fusion076]
FEATURE [Part::MultiFuse] Fusion077  label="removeToCreatePlugHousingBottomBit"
  Shapes = -> [Fusion075,Fusion073]
FEATURE [Part::Cylinder] Cylinder034
  Angle = 360
  AttacherType = Attacher::AttachEngine3D
  Height = 20
  Placement = pos=(0,0,36.15) rot=(0,0,1;0rad)
  Radius = 14
FEATURE [Part::Cylinder] Cylinder035
  Angle = 360
  AttacherType = Attacher::AttachEngine3D
  Height = 10
  Placement = pos=(0,0,36.15) rot=(0,0,1;0rad)
  Radius = 4
FEATURE [Part::MultiFuse] Fusion078  label="removeToCreteHoleForPlugHousing024"
  Placement = pos=(70,19,36) rot=(0,1,0;1.5708rad)
  Shapes = -> [Cylinder034,Cylinder035]
FEATURE [Part::MultiFuse] Fusion079  label="removeToCreatePlugHousingBottomBit001"
  Shapes = -> [Fusion078,Fusion077]
FEATURE [Part::Extrusion] Extrude040  label="bottomPlugHousingBit"
  Base = -> Sketch049
  Dir = (0,0,1)
  DirMode = 2
  FaceMakerClass = Part::FaceMakerBullseye
  LengthFwd = 72
  LengthRev = 0
  Solid = true
  Symmetric = false
FEATURE [Part::Cut] Cut034  label="bottomPlugHousingBit001"
  Base = -> Extrude040
  Placement = pos=(-0.09,0,0) rot=(0,0,1;0rad)
  Tool = -> Fusion079
FEATURE [Part::Box] Box023  label="Cube014"
  AttacherType = Attacher::AttachEngine3D
  Height = 16
  Length = 8
  Placement = pos=(12.7,31.52,28) rot=(0,0,1;0rad)
  Width = 4
FEATURE [Part::Cylinder] Cylinder036
  Angle = 360
  AttacherType = Attacher::AttachEngine3D
  Height = 10
  Placement = pos=(0,0,36.15) rot=(0,0,1;0rad)
  Radius = 4
FEATURE [Part::Cylinder] Cylinder037
  Angle = 360
  AttacherType = Attacher::AttachEngine3D
  Height = 20
  Placement = pos=(0,0,36.15) rot=(0,0,1;0rad)
  Radius = 8.2
FEATURE [Part::MultiFuse] Fusion080  label="removeToCreteHoleForPlugHousing025"
  Placement = pos=(-42,19,36) rot=(0,1,0;1.5708rad)
  Shapes = -> [Cylinder037,Cylinder036]
FEATURE [Sketcher::SketchObject] Sketch050  label="topSketch012"
  FullyConstrained = true
  sketch-geometry (4):
    g0: LineSegment StartX=16.8446 StartY=31.512 StartZ=0 EndX=16.3251 EndY=34.4666 EndZ=0
    g1: ArcOfCircle CenterX=19 CenterY=19.2524 CenterZ=0 NormalX=0 NormalY=0 NormalZ=1 AngleXU=0 Radius=15.4476 StartAngle=1.74483 EndAngle=2.72717
    g2: ArcOfCircle CenterX=19 CenterY=19.2524 CenterZ=0 NormalX=0 NormalY=0 NormalZ=1 AngleXU=0 Radius=12.4476 StartAngle=1.74483 EndAngle=2.73189
    g3: LineSegment StartX=4.86004 StartY=25.4725 StartZ=0 EndX=7.58253 EndY=24.2107 EndZ=0
  constraints (7):
    c: Block(g0)
    c: Coincident(g1,g0)
    c: Coincident(g2,g0)
    c: Coincident(g3,g1)
    c: Coincident(g3,g2)
    c: Block(g1)
    c: Block(g2)
FEATURE [Part::Extrusion] Extrude041
  Base = -> Sketch050
  Dir = (0,0,1)
  DirMode = 2
  FaceMakerClass = Part::FaceMakerBullseye
  LengthFwd = 10.6
  LengthRev = 0
  Placement = pos=(0,0,31) rot=(0,0,1;0rad)
  Solid = true
  Symmetric = false
FEATURE [Part::Cut] Cut035
  Base = -> Extrude041
  Placement = pos=(0,0,-0.3) rot=(0,0,1;0rad)
  Tool = -> Fusion080
FEATURE [Part::Cut] Cut036
  Base = -> Box023
  Tool = -> Cut035
FEATURE [Part::Fillet] Fillet027
  Base = -> Cut036
  Edges = 1 edges r=0.7: [Edge13]
FEATURE [Part::Fillet] Fillet028
  Base = -> Fillet027
  Edges = 1 edges r=0.7: [Edge13]
FEATURE [Part::Fillet] Fillet029
  Base = -> Fillet028
  Edges = 1 edges r=0.7: [Edge16]
FEATURE [Part::Fillet] Fillet030
  Base = -> Fillet029
  Edges = 1 edges r=0.7: [Edge11]
FEATURE [Part::Fillet] Fillet031
  Base = -> Fillet030
  Edges = 1 edges r=0.7: [Edge10]
FEATURE [Part::Fillet] Fillet032
  Base = -> Fillet031
  Edges = 1 edges r=1.2: [Edge5]
FEATURE [Part::Fillet] Fillet033
  Base = -> Fillet032
  Edges = 1 edges r=1.2: [Edge12]
FEATURE [Part::Fillet] Fillet034  label="wireHousingRetainer"
  Base = -> Fillet033
  Edges = 1 edges r=2: [Edge1]
  Placement = pos=(0.3,0,0) rot=(0,0,1;0rad)
FEATURE [Part::Feature] Face099
  shape: bbox 3.5 x 17.8 x 2e-07 mm, 1 faces, 0 solids (baked)
FEATURE [Part::Revolution] Revolve107  label="removeToCreateScrewAndThreadedInsertHole034"
  Angle = 360
  Axis = (0,1,0)
  Base = (0,0,0)
  FaceMakerClass = Part::FaceMakerBullseye
  Placement = pos=(12.5,0,10) rot=(0,0,1;0rad)
  Solid = false
  Source = -> Face099
  Symmetric = false
FEATURE [Part::Feature] Face100
  shape: bbox 3.5 x 17.8 x 2e-07 mm, 1 faces, 0 solids (baked)
FEATURE [Part::Revolution] Revolve108  label="removeToCreateScrewAndThreadedInsertHole035"
  Angle = 360
  Axis = (0,1,0)
  Base = (0,0,0)
  FaceMakerClass = Part::FaceMakerBullseye
  Placement = pos=(12.5,0,62) rot=(0,0,1;0rad)
  Solid = false
  Source = -> Face100
  Symmetric = false
FEATURE [Part::Feature] Face101
  shape: bbox 3.5 x 17.8 x 2e-07 mm, 1 faces, 0 solids (baked)
FEATURE [Part::Revolution] Revolve109  label="removeToCreateScrewAndThreadedInsertHole036"
  Angle = 360
  Axis = (0,1,0)
  Base = (0,0,0)
  FaceMakerClass = Part::FaceMakerBullseye
  Placement = pos=(89.5,0,68.5) rot=(0,0,1;0rad)
  Solid = false
  Source = -> Face101
  Symmetric = false
FEATURE [Part::Feature] Face102
  shape: bbox 3.5 x 17.8 x 2e-07 mm, 1 faces, 0 solids (baked)
FEATURE [Part::Revolution] Revolve110  label="removeToCreateScrewAndThreadedInsertHole037"
  Angle = 360
  Axis = (0,1,0)
  Base = (0,0,0)
  FaceMakerClass = Part::FaceMakerBullseye
  Placement = pos=(89.5,0,3.5) rot=(0,0,1;0rad)
  Solid = false
  Source = -> Face102
  Symmetric = false
FEATURE [Part::Feature] Face103
  shape: bbox 3.5 x 17.8 x 2e-07 mm, 1 faces, 0 solids (baked)
FEATURE [Part::Revolution] Revolve111  label="removeToCreateScrewAndThreadedInsertHole038"
  Angle = 360
  Axis = (0,1,0)
  Base = (0,0,0)
  FaceMakerClass = Part::FaceMakerBullseye
  Placement = pos=(109.5,4.7,3.5) rot=(0,0,1;0rad)
  Solid = false
  Source = -> Face103
  Symmetric = false
FEATURE [Part::Feature] Face104
  shape: bbox 3.5 x 17.8 x 2e-07 mm, 1 faces, 0 solids (baked)
FEATURE [Part::Revolution] Revolve112  label="removeToCreateScrewAndThreadedInsertHole039"
  Angle = 360
  Axis = (0,1,0)
  Base = (0,0,0)
  FaceMakerClass = Part::FaceMakerBullseye
  Placement = pos=(109.5,4.7,68.5) rot=(0,0,1;0rad)
  Solid = false
  Source = -> Face104
  Symmetric = false
FEATURE [Part::MultiFuse] Fusion081  label="removeToCreateScrewAndThreadedInsertHole040"
  Shapes = -> [Revolve107,Revolve108,Revolve109,Revolve110,Revolve111,Revolve112]
FEATURE [Part::MultiFuse] Fusion082  label="casePillars002"
  Shapes = -> [Revolve094,Revolve092,Revolve090,Revolve089,Revolve091,Revolve093]
FEATURE [Part::Cut] Cut037  label="casePillars003"
  Base = -> Fusion082
  Tool = -> Fusion081
FEATURE [Sketcher::SketchObject] Sketch051
  FullyConstrained = true
  Placement = pos=(117,19,0) rot=(0.57735,0.57735,0.57735;2.0944rad)
  sketch-geometry (48):
    g0: LineSegment StartX=-49.19 StartY=69.25 StartZ=0 EndX=-49.19 EndY=66.25 EndZ=0
    g1: LineSegment StartX=-49.19 StartY=63.5 StartZ=0 EndX=-49.19 EndY=60.5 EndZ=0
    g2: LineSegment StartX=-49.19 StartY=57.75 StartZ=0 EndX=-49.19 EndY=54.75 EndZ=0
    g3: LineSegment StartX=-49.19 StartY=52 StartZ=0 EndX=-49.19 EndY=49 EndZ=0
    g4: LineSegment StartX=-49.19 StartY=46.25 StartZ=0 EndX=-49.19 EndY=43.25 EndZ=0
    g5: LineSegment StartX=-49.19 StartY=40.5 StartZ=0 EndX=-49.19 EndY=37.5 EndZ=0
    g6: LineSegment StartX=-49.19 StartY=34.5 StartZ=0 EndX=-49.19 EndY=31.5 EndZ=0
    g7: LineSegment StartX=-49.19 StartY=28.75 StartZ=0 EndX=-49.19 EndY=25.75 EndZ=0
    g8: LineSegment StartX=-49.19 StartY=23 StartZ=0 EndX=-49.19 EndY=20 EndZ=0
    g9: LineSegment StartX=-49.19 StartY=17.25 StartZ=0 EndX=-49.19 EndY=14.25 EndZ=0
    g10: LineSegment StartX=-49.19 StartY=11.5 StartZ=0 EndX=-49.19 EndY=8.5 EndZ=0
    g11: LineSegment StartX=-49.19 StartY=5.75 StartZ=0 EndX=-49.19 EndY=2.75 EndZ=0
    g12: ArcOfCircle CenterX=-1.5 CenterY=67.75 CenterZ=0 NormalX=0 NormalY=0 NormalZ=1 AngleXU=0 Radius=1.5 StartAngle=4.71239 EndAngle=7.85398
    g13: ArcOfCircle CenterX=-1.5 CenterY=62 CenterZ=0 NormalX=0 NormalY=0 NormalZ=1 AngleXU=0 Radius=1.5 StartAngle=4.71239 EndAngle=7.85398
    g14: ArcOfCircle CenterX=-1.5 CenterY=56.25 CenterZ=0 NormalX=0 NormalY=0 NormalZ=1 AngleXU=0 Radius=1.5 StartAngle=4.71239 EndAngle=7.85398
    g15: ArcOfCircle CenterX=-11.49 CenterY=50.5 CenterZ=0 NormalX=0 NormalY=0 NormalZ=1 AngleXU=0 Radius=1.5 StartAngle=4.71239 EndAngle=7.85398
    g16: ArcOfCircle CenterX=-16.28 CenterY=44.75 CenterZ=0 NormalX=0 NormalY=0 NormalZ=1 AngleXU=0 Radius=1.5 StartAngle=4.71239 EndAngle=7.85398
    g17: ArcOfCircle CenterX=-18.2337 CenterY=39 CenterZ=0 NormalX=0 NormalY=0 NormalZ=1 AngleXU=0 Radius=1.5 StartAngle=4.71485 EndAngle=7.85398
    g18: ArcOfCircle CenterX=-16.2837 CenterY=27.25 CenterZ=0 NormalX=0 NormalY=0 NormalZ=1 AngleXU=0 Radius=1.5 StartAngle=4.71485 EndAngle=7.85398
    g19: ArcOfCircle CenterX=-18.2337 CenterY=33 CenterZ=0 NormalX=0 NormalY=0 NormalZ=1 AngleXU=0 Radius=1.5 StartAngle=4.71485 EndAngle=7.85398
    g20: ArcOfCircle CenterX=-11.49 CenterY=21.5 CenterZ=0 NormalX=0 NormalY=0 NormalZ=1 AngleXU=0 Radius=1.5 StartAngle=4.71239 EndAngle=7.85398
    g21: ArcOfCircle CenterX=-1.5 CenterY=4.25 CenterZ=0 NormalX=0 NormalY=0 NormalZ=1 AngleXU=0 Radius=1.5 StartAngle=4.71239 EndAngle=7.85398
    g22: ArcOfCircle CenterX=-1.5 CenterY=10 CenterZ=0 NormalX=0 NormalY=0 NormalZ=1 AngleXU=0 Radius=1.5 StartAngle=4.71239 EndAngle=7.85398
    g23: ArcOfCircle CenterX=-1.5 CenterY=15.75 CenterZ=0 NormalX=0 NormalY=0 NormalZ=1 AngleXU=0 Radius=1.5 StartAngle=4.71239 EndAngle=7.85398
    g24: LineSegment StartX=-49.19 StartY=69.25 StartZ=0 EndX=-1.5 EndY=69.25 EndZ=0
    g25: LineSegment StartX=-49.19 StartY=66.25 StartZ=0 EndX=-1.5 EndY=66.25 EndZ=0
    g26: LineSegment StartX=-49.19 StartY=63.5 StartZ=0 EndX=-1.5 EndY=63.5 EndZ=0
    g27: LineSegment StartX=-49.19 StartY=60.5 StartZ=0 EndX=-1.5 EndY=60.5 EndZ=0
    g28: LineSegment StartX=-49.19 StartY=57.75 StartZ=0 EndX=-1.5 EndY=57.75 EndZ=0
    g29: LineSegment StartX=-49.19 StartY=54.75 StartZ=0 EndX=-1.5 EndY=54.75 EndZ=0
    g30: LineSegment StartX=-49.19 StartY=52 StartZ=0 EndX=-11.49 EndY=52 EndZ=0
    g31: LineSegment StartX=-49.19 StartY=49 StartZ=0 EndX=-11.49 EndY=49 EndZ=0
    g32: LineSegment StartX=-49.19 StartY=46.25 StartZ=0 EndX=-16.28 EndY=46.25 EndZ=0
    g33: LineSegment StartX=-49.19 StartY=43.25 StartZ=0 EndX=-16.28 EndY=43.25 EndZ=0
    g34: LineSegment StartX=-49.19 StartY=40.5 StartZ=0 EndX=-18.2337 EndY=40.5 EndZ=0
    g35: LineSegment StartX=-49.19 StartY=37.5 StartZ=0 EndX=-18.23 EndY=37.5 EndZ=0
    g36: LineSegment StartX=-49.19 StartY=34.5 StartZ=0 EndX=-18.2337 EndY=34.5 EndZ=0
    g37: LineSegment StartX=-49.19 StartY=31.5 StartZ=0 EndX=-18.23 EndY=31.5 EndZ=0
    g38: LineSegment StartX=-49.19 StartY=28.75 StartZ=0 EndX=-16.2837 EndY=28.75 EndZ=0
    g39: LineSegment StartX=-49.19 StartY=25.75 StartZ=0 EndX=-16.28 EndY=25.75 EndZ=0
    g40: LineSegment StartX=-49.19 StartY=23 StartZ=0 EndX=-11.49 EndY=23 EndZ=0
    g41: LineSegment StartX=-49.19 StartY=20 StartZ=0 EndX=-11.49 EndY=20 EndZ=0
    g42: LineSegment StartX=-49.19 StartY=17.25 StartZ=0 EndX=-1.5 EndY=17.25 EndZ=0
    g43: LineSegment StartX=-49.19 StartY=14.25 StartZ=0 EndX=-1.5 EndY=14.25 EndZ=0
    g44: LineSegment StartX=-49.19 StartY=11.5 StartZ=0 EndX=-1.5 EndY=11.5 EndZ=0
    g45: LineSegment StartX=-49.19 StartY=8.5 StartZ=0 EndX=-1.5 EndY=8.5 EndZ=0
    g46: LineSegment StartX=-49.19 StartY=5.75 StartZ=0 EndX=-1.5 EndY=5.75 EndZ=0
    g47: LineSegment StartX=-49.19 StartY=2.75 StartZ=0 EndX=-1.5 EndY=2.75 EndZ=0
  constraints (120):
    c: Vertical(g0)
    c: Distance(g0) = 3
    c: Block(g0)
    c: Vertical(g1)
    c: Distance(g1) = 3
    c: Vertical(g2)
    c: Equal(g0,g2) = 3
    c: Block(g2)
    c: Vertical(g3)
    c: Equal(g1,g3) = 3
    c: Vertical(g4)
    c: Equal(g0,g4) = 3
    c: Block(g4)
    c: Vertical(g5)
    c: Equal(g1,g5) = 3
    c: Vertical(g6)
    c: Equal(g0,g6) = 3
    c: Block(g6)
    c: Vertical(g7)
    c: Equal(g1,g7) = 3
    c: Vertical(g8)
    c: Equal(g0,g8) = 3
    c: Block(g8)
    c: Vertical(g9)
    c: Equal(g1,g9) = 3
    c: Vertical(g10)
    c: Equal(g0,g10) = 3
    c: Block(g10)
    c: Vertical(g11)
    c: Equal(g1,g11) = 3
    c: Block(g12)
    c: Block(g13)
    c: Block(g14)
    c: Block(g15)
    c: Block(g16)
    c: Block(g17)
    c: Block(g18)
    c: Block(g19)
    c: Block(g20)
    c: Block(g21)
    c: Block(g22)
    c: Block(g23)
    c: Block(g11)
    c: Block(g9)
    c: Block(g7)
    c: Block(g5)
    c: Block(g3)
    c: Block(g1)
    c: Coincident(g24,g0)
    c: Coincident(g24,g12)
    c: Horizontal(g24)
    c: Coincident(g25,g0)
    c: Coincident(g25,g12)
    c: Horizontal(g25)
    c: Coincident(g26,g1)
    c: Coincident(g26,g13)
    c: Horizontal(g26)
    c: Coincident(g27,g1)
    c: Coincident(g27,g13)
    c: Horizontal(g27)
    c: Coincident(g28,g2)
    c: Coincident(g28,g14)
    c: Horizontal(g28)
    c: Coincident(g29,g2)
    c: Coincident(g29,g14)
    c: Horizontal(g29)
    c: Coincident(g30,g3)
    c: Coincident(g30,g15)
    c: Horizontal(g30)
    c: Coincident(g31,g3)
    c: Coincident(g31,g15)
    c: Horizontal(g31)
    c: Coincident(g32,g4)
    c: Coincident(g32,g16)
    c: Horizontal(g32)
    c: Coincident(g33,g4)
    c: Coincident(g33,g16)
    c: Horizontal(g33)
    c: Coincident(g34,g5)
    c: Coincident(g34,g17)
    c: Horizontal(g34)
    c: Coincident(g35,g5)
    c: Coincident(g35,g17)
    c: Horizontal(g35)
    c: Coincident(g36,g6)
    c: Coincident(g36,g19)
    c: Horizontal(g36)
    c: Coincident(g37,g6)
    c: Coincident(g37,g19)
    c: Horizontal(g37)
    c: Coincident(g38,g7)
    c: Coincident(g38,g18)
    c: Horizontal(g38)
    c: Coincident(g39,g7)
    c: Coincident(g39,g18)
    c: Horizontal(g39)
    c: Coincident(g40,g8)
    c: Coincident(g40,g20)
    c: Horizontal(g40)
    c: Coincident(g41,g8)
    c: Coincident(g41,g20)
    c: Horizontal(g41)
    c: Coincident(g42,g9)
    c: Coincident(g42,g23)
    c: Horizontal(g42)
    c: Coincident(g43,g9)
    c: Coincident(g43,g23)
    c: Horizontal(g43)
    c: Coincident(g44,g10)
    c: Coincident(g44,g22)
    c: Horizontal(g44)
    c: Coincident(g45,g10)
    c: Coincident(g45,g22)
    c: Horizontal(g45)
    c: Coincident(g46,g11)
    c: Coincident(g46,g21)
    c: Horizontal(g46)
    c: Coincident(g47,g11)
    c: Coincident(g47,g21)
    c: Horizontal(g47)
FEATURE [Part::Extrusion] Extrude042
  Base = -> Sketch051
  Dir = (1,-2e-16,2e-16)
  DirMode = 2
  FaceMakerClass = Part::FaceMakerBullseye
  LengthFwd = 19
  LengthRev = 0
  Placement = pos=(-19,0,0) rot=(0,0,1;0rad)
  Solid = true
  Symmetric = false
FEATURE [Part::Fillet] Fillet035  label="removeToCreateVentalationHoles"
  Base = -> Extrude042
  Edges = <same value as first occurrence — deduplicated (x4 in doc)>
  Placement = pos=(7,0,0) rot=(0,0,1;0rad)
FEATURE [Part::Cut] Cut038  label="top017"
  Base = -> Cut033
  Tool = -> Fillet035
FEATURE [Sketcher::SketchObject] Sketch052  label="bottomSketch001"
  FullyConstrained = true
  sketch-geometry (26):
    g0: LineSegment StartX=6.29999 StartY=8 StartZ=0 EndX=3.29999 EndY=8 EndZ=0
    g1: LineSegment StartX=3.29999 StartY=8 StartZ=0 EndX=3.29999 EndY=-6.03275e-07 EndZ=0
    g2: ArcOfCircle CenterX=8.29999 CenterY=5 CenterZ=0 NormalX=0 NormalY=0 NormalZ=1 AngleXU=0 Radius=2 StartAngle=3.14159 EndAngle=4.71239
    g3: LineSegment StartX=6.29999 StartY=8 StartZ=0 EndX=6.29999 EndY=5 EndZ=0
    g4: ArcOfCircle CenterX=105 CenterY=19 CenterZ=0 NormalX=0 NormalY=0 NormalZ=1 AngleXU=0 Radius=12.7 StartAngle=4.71239 EndAngle=6.28319
    g5-g11: Circle x7 (B-spline internal-alignment scaffolding for g12; pole/knot coordinates omitted)
    g12: BSplineCurve PolesCount=7 KnotsCount=5 Degree=3 IsPeriodic=0
    g13-g17: GeomPoint x5 (B-spline internal-alignment scaffolding for g12; pole/knot coordinates omitted)
    g18: ArcOfCircle CenterX=105 CenterY=19 CenterZ=0 NormalX=0 NormalY=0 NormalZ=1 AngleXU=0 Radius=15.7 StartAngle=5.81226 EndAngle=6.28319
    g19: LineSegment StartX=117.7 StartY=19 StartZ=0 EndX=120.7 EndY=19 EndZ=0
    g20: BSplineCurve PolesCount=5 KnotsCount=3 Degree=3 IsPeriodic=0
    g21: LineSegment StartX=8.29999 StartY=3 StartZ=0 EndX=101.7 EndY=3 EndZ=0
    g22: LineSegment StartX=3.29999 StartY=-6.03275e-07 StartZ=0 EndX=105 EndY=-6.03275e-07 EndZ=0
    g23: LineSegment StartX=120.974 StartY=8.71251 StartZ=0 EndX=122.332 EndY=7.83778 EndZ=0
    g24: LineSegment StartX=105 StartY=-6.03274e-07 StartZ=0 EndX=113 EndY=-6.03274e-07 EndZ=0
    g25: ArcOfCircle CenterX=105 CenterY=19 CenterZ=0 NormalX=0 NormalY=0 NormalZ=1 AngleXU=0 Radius=20.6155 StartAngle=5.11091 EndAngle=5.71103
  constraints (38):
    c: Horizontal(g0)
    c: Distance(g0) = 3
    c: Coincident(g1,g0)
    c: Vertical(g1)
    c: Block(g2)
    c: Block(g0)
    c: Coincident(g3,g0)
    c: Coincident(g3,g2)
    c: Vertical(g3)
    c: Block(g1)
    c: Block(g4)
    c: Coincident(g20,g4)
    c: Block(g20)
    c: Equal(g5, g6-g11) x6
    c: InternalAlignment(g5-g11 -> g12) x7
    c: InternalAlignment(g13-g17 -> g12) x5
    c: Block(g12)
    c: Coincident(g18,g12)
    c: Coincident(g19,g4)
    c: Coincident(g19,g18)
    c: Horizontal(g19)
    c: Block(g19)
    c: Block(g18)
    c: Coincident(g21,g2)
    c: Coincident(g21,g20)
    c: Horizontal(g21)
    c: Distance(g21) = 93.4
    c: Coincident(g22,g1)
    c: Horizontal(g22)
    c: Distance(g22) = 101.7
    c: Horizontal(g24)
    c: Distance(g24) = 8
    c: Coincident(g25,g24)
    c: Block(g24)
    c: Coincident(g23,g25)
    c: Block(g25)
    c: Block(g23)
    c: Distance(g23) = 1.61553
FEATURE [Part::Extrusion] Extrude043  label="bottom010"
  Base = -> Sketch052
  Dir = (0,0,1)
  DirMode = 2
  FaceMakerClass = Part::FaceMakerBullseye
  LengthFwd = 71.4
  LengthRev = 0
  Placement = pos=(0,0,0.3) rot=(0,0,1;0rad)
  Solid = true
  Symmetric = false
FEATURE [Sketcher::SketchObject] Sketch053  label="topSketch013"
  FullyConstrained = true
  sketch-geometry (22):
    g0: LineSegment StartX=5.21097e-06 StartY=3 StartZ=0 EndX=5.21097e-06 EndY=19 EndZ=0
    g1: ArcOfCircle CenterX=19 CenterY=19 CenterZ=0 NormalX=0 NormalY=0 NormalZ=1 AngleXU=0 Radius=19 StartAngle=1.5708 EndAngle=3.14159
    g2: ArcOfCircle CenterX=19 CenterY=19 CenterZ=0 NormalX=0 NormalY=0 NormalZ=1 AngleXU=0 Radius=16 StartAngle=1.5708 EndAngle=3.14159
    g3: LineSegment StartX=114 StartY=35 StartZ=0 EndX=19 EndY=35 EndZ=0
    g4: LineSegment StartX=5.21097e-06 StartY=3 StartZ=0 EndX=5.21097e-06 EndY=0 EndZ=0
    g5: LineSegment StartX=3 StartY=0 StartZ=0 EndX=5.21097e-06 EndY=0 EndZ=0
    g6: LineSegment StartX=3 StartY=19 StartZ=0 EndX=3 EndY=0 EndZ=0
    g7: LineSegment StartX=19 StartY=38 StartZ=0 EndX=124 EndY=38 EndZ=0
    g8: Circle CenterX=119 CenterY=35 CenterZ=0 NormalX=0 NormalY=0 NormalZ=1 AngleXU=0 Radius=1
    g9: Circle CenterX=121 CenterY=35 CenterZ=0 NormalX=0 NormalY=0 NormalZ=1 AngleXU=0 Radius=1
    g10: Circle CenterX=121 CenterY=33 CenterZ=0 NormalX=0 NormalY=0 NormalZ=1 AngleXU=0 Radius=1
    g11: BSplineCurve PolesCount=3 KnotsCount=2 Degree=2 IsPeriodic=0
    g12: GeomPoint X=119 Y=35 Z=0
    g13: GeomPoint X=121 Y=33 Z=0
    g14: LineSegment StartX=119 StartY=35 StartZ=0 EndX=114 EndY=35 EndZ=0
    g15: ArcOfCircle CenterX=105 CenterY=19 CenterZ=0 NormalX=0 NormalY=0 NormalZ=1 AngleXU=0 Radius=16 StartAngle=5.60905 EndAngle=6.28319
    g16: LineSegment StartX=121 StartY=33 StartZ=0 EndX=121 EndY=19 EndZ=0
    g17: LineSegment StartX=117.5 StartY=9.01251 StartZ=0 EndX=121.163 EndY=9.0125 EndZ=0
    g18: ArcOfCircle CenterX=105 CenterY=19 CenterZ=0 NormalX=0 NormalY=0 NormalZ=1 AngleXU=0 Radius=20.6155 StartAngle=5.7297 EndAngle=6.28319
    g19: LineSegment StartX=121.163 StartY=9.0125 StartZ=0 EndX=122.538 EndY=8.16329 EndZ=0
    g20: LineSegment StartX=124 StartY=38 StartZ=0 EndX=125.616 EndY=38 EndZ=0
    g21: LineSegment StartX=125.616 StartY=19 StartZ=0 EndX=125.616 EndY=38 EndZ=0
  constraints (50):
    c: Vertical(g0)
    c: Block(g0)
    c: Coincident(g1,g0)
    c: Block(g1)
    c: Coincident(g2,g1)
    c: Block(g2)
    c: Coincident(g3,g2)
    c: Horizontal(g3)
    c: Tangent(g3,g2)
    c: Coincident(g4,g0)
    c: Distance(g4) = 3
    c: Vertical(g4)
    c: Coincident(g5,g4)
    c: Horizontal(g5)
    c: Coincident(g6,g2)
    c: Coincident(g6,g5)
    c: Vertical(g6)
    c: Horizontal(g7)
    c: Distance(g7) = 105
    c: Coincident(g7,g1)
    c: Block(g3)
    c: Weight(g8) = 1
    c: Equal(g8,g9)
    c: Equal(g8,g10)
    c: InternalAlignment(g8,g11)
    c: InternalAlignment(g9,g11)
    c: InternalAlignment(g10,g11)
    c: InternalAlignment(g12,g11)
    c: InternalAlignment(g13,g11)
    c: Block(g11)
    c: Coincident(g14,g11)
    c: Coincident(g14,g3)
    c: Horizontal(g14)
    c: Block(g15)
    c: Coincident(g16,g11)
    c: Coincident(g16,g15)
    c: Vertical(g16)
    c: Distance(g16) = 14
    c: Coincident(g17,g15)
    c: Block(g18)
    c: Coincident(g19,g18)
    c: Coincident(g20,g7)
    c: Horizontal(g20)
    c: Vertical(g21)
    c: Coincident(g20,g21)
    c: Block(g20)
    c: Block(g21)
    c: Block(g19)
    c: Block(g17)
    c: Distance(g20) = 1.61553
FEATURE [Part::Extrusion] Extrude044
  Base = -> Sketch053
  Dir = (0,0,1)
  DirMode = 2
  FaceMakerClass = Part::FaceMakerBullseye
  LengthFwd = 72
  LengthRev = 0
  Solid = true
  Symmetric = false
FEATURE [Part::Fillet] Fillet036  label="top018"
  Base = -> Extrude044
  Edges = 1 edges r=2: [Edge41]
FEATURE [Part::Fillet] Fillet037  label="bottom011"
  Base = -> Extrude043
  Edges = 1 edges r=2.4: [Edge26]
FEATURE [Sketcher::SketchObject] Sketch054
  FullyConstrained = false
  Placement = pos=(0,0,0) rot=(1,0,0;1.5708rad)
  sketch-geometry (24):
    g0: ArcOfCircle CenterX=-4 CenterY=-10.5 CenterZ=0 NormalX=0 NormalY=0 NormalZ=1 AngleXU=0 Radius=1.5 StartAngle=6e-16 EndAngle=3.14159
    g1: ArcOfCircle CenterX=-34.2 CenterY=-10.5 CenterZ=0 NormalX=0 NormalY=0 NormalZ=1 AngleXU=0 Radius=1.5 StartAngle=0 EndAngle=3.14159
    g2: ArcOfCircle CenterX=-34.2 CenterY=-27.7 CenterZ=0 NormalX=0 NormalY=0 NormalZ=1 AngleXU=0 Radius=1.5 StartAngle=3.14159 EndAngle=6.28319
    g3: ArcOfCircle CenterX=-4 CenterY=-27.7 CenterZ=0 NormalX=0 NormalY=0 NormalZ=1 AngleXU=0 Radius=1.5 StartAngle=3.1416 EndAngle=6.28319
    g4: ArcOfCircle CenterX=-10 CenterY=-4.3 CenterZ=0 NormalX=0 NormalY=0 NormalZ=1 AngleXU=0 Radius=1.5 StartAngle=2e-16 EndAngle=3.14159
    g5: ArcOfCircle CenterX=-16.1 CenterY=-1.8 CenterZ=0 NormalX=0 NormalY=0 NormalZ=1 AngleXU=0 Radius=1.5 StartAngle=5e-16 EndAngle=3.14159
    g6: ArcOfCircle CenterX=-22.1 CenterY=-1.8 CenterZ=0 NormalX=0 NormalY=0 NormalZ=1 AngleXU=0 Radius=1.5 StartAngle=5e-16 EndAngle=3.14159
    g7: ArcOfCircle CenterX=-28.2 CenterY=-4.3 CenterZ=0 NormalX=0 NormalY=0 NormalZ=1 AngleXU=0 Radius=1.5 StartAngle=2e-16 EndAngle=3.14159
    g8: ArcOfCircle CenterX=-10 CenterY=-33.9 CenterZ=0 NormalX=0 NormalY=0 NormalZ=1 AngleXU=0 Radius=1.5 StartAngle=3.14159 EndAngle=6.28319
    g9: ArcOfCircle CenterX=-16.1 CenterY=-36.4 CenterZ=0 NormalX=0 NormalY=0 NormalZ=1 AngleXU=0 Radius=1.5 StartAngle=3.14159 EndAngle=6.28319
    g10: ArcOfCircle CenterX=-22.1 CenterY=-36.4 CenterZ=0 NormalX=0 NormalY=0 NormalZ=1 AngleXU=0 Radius=1.5 StartAngle=3.14159 EndAngle=6.28319
    g11: ArcOfCircle CenterX=-28.2 CenterY=-33.9 CenterZ=0 NormalX=0 NormalY=0 NormalZ=1 AngleXU=0 Radius=1.5 StartAngle=3.14159 EndAngle=6.28319
    g12: LineSegment StartX=-35.7 StartY=-10.5 StartZ=0 EndX=-35.7 EndY=-27.7 EndZ=0
    g13: LineSegment StartX=-32.7 StartY=-10.5 StartZ=0 EndX=-32.7 EndY=-27.7 EndZ=0
    g14: LineSegment StartX=-29.7 StartY=-33.9 StartZ=0 EndX=-29.7 EndY=-4.3 EndZ=0
    g15: LineSegment StartX=-26.7 StartY=-33.9 StartZ=0 EndX=-26.7 EndY=-4.3 EndZ=0
    g16: LineSegment StartX=-2.5 StartY=-10.5 StartZ=0 EndX=-2.5 EndY=-27.7 EndZ=0
    g17: LineSegment StartX=-8.5 StartY=-4.3 StartZ=0 EndX=-8.5 EndY=-33.9 EndZ=0
    g18: LineSegment StartX=-5.5 StartY=-10.5 StartZ=0 EndX=-5.5 EndY=-27.7 EndZ=0
    g19: LineSegment StartX=-11.5 StartY=-4.3 StartZ=0 EndX=-11.5 EndY=-33.9 EndZ=0
    g20: LineSegment StartX=-14.6 StartY=-1.8 StartZ=0 EndX=-14.6 EndY=-36.4 EndZ=0
    g21: LineSegment StartX=-17.6 StartY=-1.8 StartZ=0 EndX=-17.6 EndY=-36.4 EndZ=0
    g22: LineSegment StartX=-20.6 StartY=-36.4 StartZ=0 EndX=-20.6 EndY=-1.8 EndZ=0
    g23: LineSegment StartX=-23.6 StartY=-1.8 StartZ=0 EndX=-23.6 EndY=-36.4 EndZ=0
  constraints (48):
    c: Block(g0)
    c: Block(g1)
    c: Block(g2)
    c: Block(g3)
    c: Block(g4)
    c: Block(g5)
    c: Block(g6)
    c: Block(g7)
    c: Block(g8)
    c: Block(g9)
    c: Block(g10)
    c: Block(g11)
    c: Coincident(g12,g1)
    c: Coincident(g12,g2)
    c: Vertical(g12)
    c: Coincident(g13,g1)
    c: Coincident(g13,g2)
    c: Vertical(g13)
    c: Coincident(g14,g11)
    c: Coincident(g14,g7)
    c: Vertical(g14)
    c: Coincident(g15,g11)
    c: Coincident(g15,g7)
    c: Vertical(g15)
    c: Coincident(g16,g0)
    c: Coincident(g16,g3)
    c: Vertical(g16)
    c: Coincident(g17,g4)
    c: Coincident(g17,g8)
    c: Vertical(g17)
    c: Coincident(g18,g0)
    c: Coincident(g18,g3)
    c: Vertical(g18)
    c: Coincident(g19,g4)
    c: Coincident(g19,g8)
    c: Vertical(g19)
    c: Coincident(g20,g5)
    c: Coincident(g20,g9)
    c: Vertical(g20)
    c: Coincident(g21,g5)
    c: Coincident(g21,g9)
    c: Vertical(g21)
    c: Coincident(g22,g10)
    c: Coincident(g22,g6)
    c: Vertical(g22)
    c: Coincident(g23,g6)
    c: Coincident(g23,g10)
    c: Vertical(g23)
FEATURE [Part::Extrusion] Extrude045  label="removeToCreateFanGrillHoles003"
  Base = -> Sketch054
  Dir = (0,-1,6e-16)
  DirMode = 2
  FaceMakerClass = Part::FaceMakerBullseye
  LengthFwd = 10
  LengthRev = 0
  Placement = pos=(65.4,44,54.82) rot=(0,0,1;0rad)
  Solid = true
  Symmetric = false
FEATURE [Part::Feature] Face105 .. Face108  x4 (patterned run collapsed; names and placements below)
  shape: bbox 3.5 x 17.8 x 2e-07 mm, 1 faces, 0 solids (baked)
FEATURE [Part::Revolution] Revolve113  label="removeToCreateScrewAndThreadedInsertHole041"
  Angle = 360
  Axis = (0,1,0)
  Base = (0,0,0)
  FaceMakerClass = Part::FaceMakerBullseye
  Placement = pos=(62.3,30.3,19.7) rot=(0,0,1;0rad)
  Solid = false
  Source = -> Face105
  Symmetric = false
FEATURE [Part::Revolution] Revolve114  label="removeToCreateScrewAndThreadedInsertHole042"
  Angle = 360
  Axis = (0,1,0)
  Base = (0,0,0)
  FaceMakerClass = Part::FaceMakerBullseye
  Placement = pos=(62.3,30.3,51.7) rot=(0,0,1;0rad)
  Solid = false
  Source = -> Face106
  Symmetric = false
FEATURE [Part::Revolution] Revolve115  label="removeToCreateScrewAndThreadedInsertHole043"
  Angle = 360
  Axis = (0,1,0)
  Base = (0,0,0)
  FaceMakerClass = Part::FaceMakerBullseye
  Placement = pos=(30.3,30.3,19.7) rot=(0,0,1;0rad)
  Solid = false
  Source = -> Face107
  Symmetric = false
FEATURE [Part::Revolution] Revolve116  label="removeToCreateScrewAndThreadedInsertHole044"
  Angle = 360
  Axis = (0,1,0)
  Base = (0,0,0)
  FaceMakerClass = Part::FaceMakerBullseye
  Placement = pos=(30.3,30.3,51.7) rot=(0,0,1;0rad)
  Solid = false
  Source = -> Face108
  Symmetric = false
FEATURE [Part::MultiFuse] Fusion083  label="createThreadedInsertHolesForFan004"
  Shapes = -> [Revolve113,Revolve114,Revolve115,Revolve116]
FEATURE [Part::Box] Box024  label="removeToCreteHoleForPlugHousing026"
  AttacherType = Attacher::AttachEngine3D
  Height = 28.6
  Length = 10
  Placement = pos=(-2,0,21.7) rot=(0,0,1;0rad)
  Width = 19
FEATURE [Part::Cylinder] Cylinder038  label="removeToCreteHoleForPlugHousing027"
  Angle = 360
  AttacherType = Attacher::AttachEngine3D
  Height = 20
  Placement = pos=(-2,19,36) rot=(0,1,0;1.5708rad)
  Radius = 14.3
FEATURE [Part::MultiFuse] Fusion084  label="removeToCreteHoleForPlugHousing028"
  Shapes = -> [Box024,Cylinder038]
FEATURE [Part::Cylinder] Cylinder039
  Angle = 360
  AttacherType = Attacher::AttachEngine3D
  Height = 20
  Placement = pos=(0,0,36.15) rot=(0,0,1;0rad)
  Radius = 14.3
FEATURE [Part::Cylinder] Cylinder040
  Angle = 360
  AttacherType = Attacher::AttachEngine3D
  Height = 10
  Placement = pos=(0,0,36.15) rot=(0,0,1;0rad)
  Radius = 4
FEATURE [Part::Box] Box025  label="removeToCreteHoleForPlugHousing030"
  AttacherType = Attacher::AttachEngine3D
  Height = 28.6
  Length = 20
  Placement = pos=(106.15,0,21.7) rot=(0,0,1;0rad)
  Width = 19
FEATURE [Part::MultiFuse] Fusion086  label="removeToCreteHoleForPlugHousing031"
  Placement = pos=(70,19,36) rot=(0,1,0;1.5708rad)
  Shapes = -> [Cylinder039,Cylinder040]
FEATURE [Part::MultiFuse] Fusion085  label="removeToCreteHoleForPlugHousing029"
  Shapes = -> [Box025,Fusion086]
FEATURE [Sketcher::SketchObject] Sketch055
  FullyConstrained = true
  Placement = pos=(117,19,0) rot=(0.57735,0.57735,0.57735;2.0944rad)
  sketch-geometry (48):
    g0: LineSegment StartX=-49.19 StartY=69.25 StartZ=0 EndX=-49.19 EndY=66.25 EndZ=0
    g1: LineSegment StartX=-49.19 StartY=63.5 StartZ=0 EndX=-49.19 EndY=60.5 EndZ=0
    g2: LineSegment StartX=-49.19 StartY=57.75 StartZ=0 EndX=-49.19 EndY=54.75 EndZ=0
    g3: LineSegment StartX=-49.19 StartY=52 StartZ=0 EndX=-49.19 EndY=49 EndZ=0
    g4: LineSegment StartX=-49.19 StartY=46.25 StartZ=0 EndX=-49.19 EndY=43.25 EndZ=0
    g5: LineSegment StartX=-49.19 StartY=40.5 StartZ=0 EndX=-49.19 EndY=37.5 EndZ=0
    g6: LineSegment StartX=-49.19 StartY=34.5 StartZ=0 EndX=-49.19 EndY=31.5 EndZ=0
    g7: LineSegment StartX=-49.19 StartY=28.75 StartZ=0 EndX=-49.19 EndY=25.75 EndZ=0
    g8: LineSegment StartX=-49.19 StartY=23 StartZ=0 EndX=-49.19 EndY=20 EndZ=0
    g9: LineSegment StartX=-49.19 StartY=17.25 StartZ=0 EndX=-49.19 EndY=14.25 EndZ=0
    g10: LineSegment StartX=-49.19 StartY=11.5 StartZ=0 EndX=-49.19 EndY=8.5 EndZ=0
    g11: LineSegment StartX=-49.19 StartY=5.75 StartZ=0 EndX=-49.19 EndY=2.75 EndZ=0
    g12: ArcOfCircle CenterX=-1.5 CenterY=67.75 CenterZ=0 NormalX=0 NormalY=0 NormalZ=1 AngleXU=0 Radius=1.5 StartAngle=4.71239 EndAngle=7.85398
    g13: ArcOfCircle CenterX=-1.5 CenterY=62 CenterZ=0 NormalX=0 NormalY=0 NormalZ=1 AngleXU=0 Radius=1.5 StartAngle=4.71239 EndAngle=7.85398
    g14: ArcOfCircle CenterX=-1.5 CenterY=56.25 CenterZ=0 NormalX=0 NormalY=0 NormalZ=1 AngleXU=0 Radius=1.5 StartAngle=4.71239 EndAngle=7.85398
    g15: ArcOfCircle CenterX=-11.49 CenterY=50.5 CenterZ=0 NormalX=0 NormalY=0 NormalZ=1 AngleXU=0 Radius=1.5 StartAngle=4.71239 EndAngle=7.85398
    g16: ArcOfCircle CenterX=-16.28 CenterY=44.75 CenterZ=0 NormalX=0 NormalY=0 NormalZ=1 AngleXU=0 Radius=1.5 StartAngle=4.71239 EndAngle=7.85398
    g17: ArcOfCircle CenterX=-18.2337 CenterY=39 CenterZ=0 NormalX=0 NormalY=0 NormalZ=1 AngleXU=0 Radius=1.5 StartAngle=4.71485 EndAngle=7.85398
    g18: ArcOfCircle CenterX=-16.2837 CenterY=27.25 CenterZ=0 NormalX=0 NormalY=0 NormalZ=1 AngleXU=0 Radius=1.5 StartAngle=4.71485 EndAngle=7.85398
    g19: ArcOfCircle CenterX=-18.2337 CenterY=33 CenterZ=0 NormalX=0 NormalY=0 NormalZ=1 AngleXU=0 Radius=1.5 StartAngle=4.71485 EndAngle=7.85398
    g20: ArcOfCircle CenterX=-11.49 CenterY=21.5 CenterZ=0 NormalX=0 NormalY=0 NormalZ=1 AngleXU=0 Radius=1.5 StartAngle=4.71239 EndAngle=7.85398
    g21: ArcOfCircle CenterX=-1.5 CenterY=4.25 CenterZ=0 NormalX=0 NormalY=0 NormalZ=1 AngleXU=0 Radius=1.5 StartAngle=4.71239 EndAngle=7.85398
    g22: ArcOfCircle CenterX=-1.5 CenterY=10 CenterZ=0 NormalX=0 NormalY=0 NormalZ=1 AngleXU=0 Radius=1.5 StartAngle=4.71239 EndAngle=7.85398
    g23: ArcOfCircle CenterX=-1.5 CenterY=15.75 CenterZ=0 NormalX=0 NormalY=0 NormalZ=1 AngleXU=0 Radius=1.5 StartAngle=4.71239 EndAngle=7.85398
    g24: LineSegment StartX=-49.19 StartY=69.25 StartZ=0 EndX=-1.5 EndY=69.25 EndZ=0
    g25: LineSegment StartX=-49.19 StartY=66.25 StartZ=0 EndX=-1.5 EndY=66.25 EndZ=0
    g26: LineSegment StartX=-49.19 StartY=63.5 StartZ=0 EndX=-1.5 EndY=63.5 EndZ=0
    g27: LineSegment StartX=-49.19 StartY=60.5 StartZ=0 EndX=-1.5 EndY=60.5 EndZ=0
    g28: LineSegment StartX=-49.19 StartY=57.75 StartZ=0 EndX=-1.5 EndY=57.75 EndZ=0
    g29: LineSegment StartX=-49.19 StartY=54.75 StartZ=0 EndX=-1.5 EndY=54.75 EndZ=0
    g30: LineSegment StartX=-49.19 StartY=52 StartZ=0 EndX=-11.49 EndY=52 EndZ=0
    g31: LineSegment StartX=-49.19 StartY=49 StartZ=0 EndX=-11.49 EndY=49 EndZ=0
    g32: LineSegment StartX=-49.19 StartY=46.25 StartZ=0 EndX=-16.28 EndY=46.25 EndZ=0
    g33: LineSegment StartX=-49.19 StartY=43.25 StartZ=0 EndX=-16.28 EndY=43.25 EndZ=0
    g34: LineSegment StartX=-49.19 StartY=40.5 StartZ=0 EndX=-18.2337 EndY=40.5 EndZ=0
    g35: LineSegment StartX=-49.19 StartY=37.5 StartZ=0 EndX=-18.23 EndY=37.5 EndZ=0
    g36: LineSegment StartX=-49.19 StartY=34.5 StartZ=0 EndX=-18.2337 EndY=34.5 EndZ=0
    g37: LineSegment StartX=-49.19 StartY=31.5 StartZ=0 EndX=-18.23 EndY=31.5 EndZ=0
    g38: LineSegment StartX=-49.19 StartY=28.75 StartZ=0 EndX=-16.2837 EndY=28.75 EndZ=0
    g39: LineSegment StartX=-49.19 StartY=25.75 StartZ=0 EndX=-16.28 EndY=25.75 EndZ=0
    g40: LineSegment StartX=-49.19 StartY=23 StartZ=0 EndX=-11.49 EndY=23 EndZ=0
    g41: LineSegment StartX=-49.19 StartY=20 StartZ=0 EndX=-11.49 EndY=20 EndZ=0
    g42: LineSegment StartX=-49.19 StartY=17.25 StartZ=0 EndX=-1.5 EndY=17.25 EndZ=0
    g43: LineSegment StartX=-49.19 StartY=14.25 StartZ=0 EndX=-1.5 EndY=14.25 EndZ=0
    g44: LineSegment StartX=-49.19 StartY=11.5 StartZ=0 EndX=-1.5 EndY=11.5 EndZ=0
    g45: LineSegment StartX=-49.19 StartY=8.5 StartZ=0 EndX=-1.5 EndY=8.5 EndZ=0
    g46: LineSegment StartX=-49.19 StartY=5.75 StartZ=0 EndX=-1.5 EndY=5.75 EndZ=0
    g47: LineSegment StartX=-49.19 StartY=2.75 StartZ=0 EndX=-1.5 EndY=2.75 EndZ=0
  constraints (120):
    c: Vertical(g0)
    c: Distance(g0) = 3
    c: Block(g0)
    c: Vertical(g1)
    c: Distance(g1) = 3
    c: Vertical(g2)
    c: Equal(g0,g2) = 3
    c: Block(g2)
    c: Vertical(g3)
    c: Equal(g1,g3) = 3
    c: Vertical(g4)
    c: Equal(g0,g4) = 3
    c: Block(g4)
    c: Vertical(g5)
    c: Equal(g1,g5) = 3
    c: Vertical(g6)
    c: Equal(g0,g6) = 3
    c: Block(g6)
    c: Vertical(g7)
    c: Equal(g1,g7) = 3
    c: Vertical(g8)
    c: Equal(g0,g8) = 3
    c: Block(g8)
    c: Vertical(g9)
    c: Equal(g1,g9) = 3
    c: Vertical(g10)
    c: Equal(g0,g10) = 3
    c: Block(g10)
    c: Vertical(g11)
    c: Equal(g1,g11) = 3
    c: Block(g12)
    c: Block(g13)
    c: Block(g14)
    c: Block(g15)
    c: Block(g16)
    c: Block(g17)
    c: Block(g18)
    c: Block(g19)
    c: Block(g20)
    c: Block(g21)
    c: Block(g22)
    c: Block(g23)
    c: Block(g11)
    c: Block(g9)
    c: Block(g7)
    c: Block(g5)
    c: Block(g3)
    c: Block(g1)
    c: Coincident(g24,g0)
    c: Coincident(g24,g12)
    c: Horizontal(g24)
    c: Coincident(g25,g0)
    c: Coincident(g25,g12)
    c: Horizontal(g25)
    c: Coincident(g26,g1)
    c: Coincident(g26,g13)
    c: Horizontal(g26)
    c: Coincident(g27,g1)
    c: Coincident(g27,g13)
    c: Horizontal(g27)
    c: Coincident(g28,g2)
    c: Coincident(g28,g14)
    c: Horizontal(g28)
    c: Coincident(g29,g2)
    c: Coincident(g29,g14)
    c: Horizontal(g29)
    c: Coincident(g30,g3)
    c: Coincident(g30,g15)
    c: Horizontal(g30)
    c: Coincident(g31,g3)
    c: Coincident(g31,g15)
    c: Horizontal(g31)
    c: Coincident(g32,g4)
    c: Coincident(g32,g16)
    c: Horizontal(g32)
    c: Coincident(g33,g4)
    c: Coincident(g33,g16)
    c: Horizontal(g33)
    c: Coincident(g34,g5)
    c: Coincident(g34,g17)
    c: Horizontal(g34)
    c: Coincident(g35,g5)
    c: Coincident(g35,g17)
    c: Horizontal(g35)
    c: Coincident(g36,g6)
    c: Coincident(g36,g19)
    c: Horizontal(g36)
    c: Coincident(g37,g6)
    c: Coincident(g37,g19)
    c: Horizontal(g37)
    c: Coincident(g38,g7)
    c: Coincident(g38,g18)
    c: Horizontal(g38)
    c: Coincident(g39,g7)
    c: Coincident(g39,g18)
    c: Horizontal(g39)
    c: Coincident(g40,g8)
    c: Coincident(g40,g20)
    c: Horizontal(g40)
    c: Coincident(g41,g8)
    c: Coincident(g41,g20)
    c: Horizontal(g41)
    c: Coincident(g42,g9)
    c: Coincident(g42,g23)
    c: Horizontal(g42)
    c: Coincident(g43,g9)
    c: Coincident(g43,g23)
    c: Horizontal(g43)
    c: Coincident(g44,g10)
    c: Coincident(g44,g22)
    c: Horizontal(g44)
    c: Coincident(g45,g10)
    c: Coincident(g45,g22)
    c: Horizontal(g45)
    c: Coincident(g46,g11)
    c: Coincident(g46,g21)
    c: Horizontal(g46)
    c: Coincident(g47,g11)
    c: Coincident(g47,g21)
    c: Horizontal(g47)
FEATURE [Part::Extrusion] Extrude046
  Base = -> Sketch055
  Dir = (1,0,0)
  DirMode = 2
  FaceMakerClass = Part::FaceMakerBullseye
  LengthFwd = 23
  LengthRev = 0
  Placement = pos=(-19,0,0) rot=(0,0,1;0rad)
  Solid = true
  Symmetric = false
FEATURE [Part::Fillet] Fillet038  label="removeToCreateVentalationHoles001"
  Base = -> Extrude046
  Edges = <same value as first occurrence — deduplicated (x4 in doc)>
  Placement = pos=(7,0,0) rot=(0,0,1;0rad)
FEATURE [Sketcher::SketchObject] Sketch056  label="topSketch014"
  FullyConstrained = true
  sketch-geometry (22):
    g0: LineSegment StartX=5.21097e-06 StartY=3 StartZ=0 EndX=5.21097e-06 EndY=19 EndZ=0
    g1: ArcOfCircle CenterX=19 CenterY=19 CenterZ=0 NormalX=0 NormalY=0 NormalZ=1 AngleXU=0 Radius=19 StartAngle=1.5708 EndAngle=3.14159
    g2: ArcOfCircle CenterX=19 CenterY=19 CenterZ=0 NormalX=0 NormalY=0 NormalZ=1 AngleXU=0 Radius=16 StartAngle=1.5708 EndAngle=3.14159
    g3: LineSegment StartX=114 StartY=35 StartZ=0 EndX=19 EndY=35 EndZ=0
    g4: LineSegment StartX=5.21097e-06 StartY=3 StartZ=0 EndX=5.21097e-06 EndY=0 EndZ=0
    g5: LineSegment StartX=3 StartY=0 StartZ=0 EndX=5.21097e-06 EndY=0 EndZ=0
    g6: LineSegment StartX=3 StartY=19 StartZ=0 EndX=3 EndY=0 EndZ=0
    g7: LineSegment StartX=19 StartY=38 StartZ=0 EndX=124 EndY=38 EndZ=0
    g8: Circle CenterX=119 CenterY=35 CenterZ=0 NormalX=0 NormalY=0 NormalZ=1 AngleXU=0 Radius=1
    g9: Circle CenterX=121 CenterY=35 CenterZ=0 NormalX=0 NormalY=0 NormalZ=1 AngleXU=0 Radius=1
    g10: Circle CenterX=121 CenterY=33 CenterZ=0 NormalX=0 NormalY=0 NormalZ=1 AngleXU=0 Radius=1
    g11: BSplineCurve PolesCount=3 KnotsCount=2 Degree=2 IsPeriodic=0
    g12: GeomPoint X=119 Y=35 Z=0
    g13: GeomPoint X=121 Y=33 Z=0
    g14: LineSegment StartX=119 StartY=35 StartZ=0 EndX=114 EndY=35 EndZ=0
    g15: ArcOfCircle CenterX=105 CenterY=19 CenterZ=0 NormalX=0 NormalY=0 NormalZ=1 AngleXU=0 Radius=16 StartAngle=5.60905 EndAngle=6.28319
    g16: LineSegment StartX=121 StartY=33 StartZ=0 EndX=121 EndY=19 EndZ=0
    g17: LineSegment StartX=117.5 StartY=9.01251 StartZ=0 EndX=121.163 EndY=9.0125 EndZ=0
    g18: ArcOfCircle CenterX=105 CenterY=19 CenterZ=0 NormalX=0 NormalY=0 NormalZ=1 AngleXU=0 Radius=20.6155 StartAngle=5.7297 EndAngle=6.28319
    g19: LineSegment StartX=121.163 StartY=9.0125 StartZ=0 EndX=122.538 EndY=8.16329 EndZ=0
    g20: LineSegment StartX=124 StartY=38 StartZ=0 EndX=125.616 EndY=38 EndZ=0
    g21: LineSegment StartX=125.616 StartY=19 StartZ=0 EndX=125.616 EndY=38 EndZ=0
  constraints (49):
    c: Vertical(g0)
    c: Block(g0)
    c: Coincident(g1,g0)
    c: Block(g1)
    c: Coincident(g2,g1)
    c: Block(g2)
    c: Coincident(g3,g2)
    c: Horizontal(g3)
    c: Tangent(g3,g2)
    c: Coincident(g4,g0)
    c: Distance(g4) = 3
    c: Vertical(g4)
    c: Coincident(g5,g4)
    c: Horizontal(g5)
    c: Coincident(g6,g2)
    c: Coincident(g6,g5)
    c: Vertical(g6)
    c: Horizontal(g7)
    c: Distance(g7) = 105
    c: Coincident(g7,g1)
    c: Block(g3)
    c: Weight(g8) = 1
    c: Equal(g8,g9)
    c: Equal(g8,g10)
    c: InternalAlignment(g8,g11)
    c: InternalAlignment(g9,g11)
    c: InternalAlignment(g10,g11)
    c: InternalAlignment(g12,g11)
    c: InternalAlignment(g13,g11)
    c: Block(g11)
    c: Coincident(g14,g11)
    c: Coincident(g14,g3)
    c: Horizontal(g14)
    c: Block(g15)
    c: Coincident(g16,g11)
    c: Coincident(g16,g15)
    c: Vertical(g16)
    c: Distance(g16) = 14
    c: Coincident(g17,g15)
    c: Block(g18)
    c: Coincident(g19,g18)
    c: Coincident(g20,g7)
    c: Horizontal(g20)
    c: Vertical(g21)
    c: Coincident(g20,g21)
    c: Block(g20)
    c: Block(g21)
    c: Block(g19)
    c: Block(g17)
FEATURE [Part::Box] Box026  label="removeToCreteHoleForPlugHousing032"
  AttacherType = Attacher::AttachEngine3D
  Height = 28.6
  Length = 10
  Placement = pos=(-2,0,21.7) rot=(0,0,1;0rad)
  Width = 19
FEATURE [Part::Feature] Face109 .. Face112  x4 (patterned run collapsed; names and placements below)
  shape: bbox 3.5 x 17.8 x 2e-07 mm, 1 faces, 0 solids (baked)
FEATURE [Part::Revolution] Revolve117  label="removeToCreateScrewAndThreadedInsertHole045"
  Angle = 360
  Axis = (0,1,0)
  Base = (0,0,0)
  FaceMakerClass = Part::FaceMakerBullseye
  Placement = pos=(62.3,30.3,19.7) rot=(0,0,1;0rad)
  Solid = false
  Source = -> Face109
  Symmetric = false
FEATURE [Part::Revolution] Revolve118  label="removeToCreateScrewAndThreadedInsertHole046"
  Angle = 360
  Axis = (0,1,0)
  Base = (0,0,0)
  FaceMakerClass = Part::FaceMakerBullseye
  Placement = pos=(62.3,30.3,51.7) rot=(0,0,1;0rad)
  Solid = false
  Source = -> Face110
  Symmetric = false
FEATURE [Part::Revolution] Revolve119  label="removeToCreateScrewAndThreadedInsertHole047"
  Angle = 360
  Axis = (0,1,0)
  Base = (0,0,0)
  FaceMakerClass = Part::FaceMakerBullseye
  Placement = pos=(30.3,30.3,19.7) rot=(0,0,1;0rad)
  Solid = false
  Source = -> Face111
  Symmetric = false
FEATURE [Part::Revolution] Revolve120  label="removeToCreateScrewAndThreadedInsertHole048"
  Angle = 360
  Axis = (0,1,0)
  Base = (0,0,0)
  FaceMakerClass = Part::FaceMakerBullseye
  Placement = pos=(30.3,30.3,51.7) rot=(0,0,1;0rad)
  Solid = false
  Source = -> Face112
  Symmetric = false
FEATURE [Part::MultiFuse] Fusion087  label="createThreadedInsertHolesForFan005"
  Shapes = -> [Revolve117,Revolve118,Revolve119,Revolve120]
FEATURE [Part::Extrusion] Extrude047
  Base = -> Sketch056
  Dir = (0,0,1)
  DirMode = 2
  FaceMakerClass = Part::FaceMakerBullseye
  LengthFwd = 72
  LengthRev = 0
  Solid = true
  Symmetric = false
FEATURE [Part::Fillet] Fillet039  label="top019"
  Base = -> Extrude047
  Edges = 1 edges r=2: [Edge35]
FEATURE [Sketcher::SketchObject] Sketch057
  FullyConstrained = false
  Placement = pos=(0,0,0) rot=(1,0,0;1.5708rad)
  sketch-geometry (24):
    g0: ArcOfCircle CenterX=-4 CenterY=-10.5 CenterZ=0 NormalX=0 NormalY=0 NormalZ=1 AngleXU=0 Radius=1.5 StartAngle=6e-16 EndAngle=3.14159
    g1: ArcOfCircle CenterX=-34.2 CenterY=-10.5 CenterZ=0 NormalX=0 NormalY=0 NormalZ=1 AngleXU=0 Radius=1.5 StartAngle=0 EndAngle=3.14159
    g2: ArcOfCircle CenterX=-34.2 CenterY=-27.7 CenterZ=0 NormalX=0 NormalY=0 NormalZ=1 AngleXU=0 Radius=1.5 StartAngle=3.14159 EndAngle=6.28319
    g3: ArcOfCircle CenterX=-4 CenterY=-27.7 CenterZ=0 NormalX=0 NormalY=0 NormalZ=1 AngleXU=0 Radius=1.5 StartAngle=3.1416 EndAngle=6.28319
    g4: ArcOfCircle CenterX=-10 CenterY=-4.3 CenterZ=0 NormalX=0 NormalY=0 NormalZ=1 AngleXU=0 Radius=1.5 StartAngle=2e-16 EndAngle=3.14159
    g5: ArcOfCircle CenterX=-16.1 CenterY=-1.8 CenterZ=0 NormalX=0 NormalY=0 NormalZ=1 AngleXU=0 Radius=1.5 StartAngle=5e-16 EndAngle=3.14159
    g6: ArcOfCircle CenterX=-22.1 CenterY=-1.8 CenterZ=0 NormalX=0 NormalY=0 NormalZ=1 AngleXU=0 Radius=1.5 StartAngle=5e-16 EndAngle=3.14159
    g7: ArcOfCircle CenterX=-28.2 CenterY=-4.3 CenterZ=0 NormalX=0 NormalY=0 NormalZ=1 AngleXU=0 Radius=1.5 StartAngle=2e-16 EndAngle=3.14159
    g8: ArcOfCircle CenterX=-10 CenterY=-33.9 CenterZ=0 NormalX=0 NormalY=0 NormalZ=1 AngleXU=0 Radius=1.5 StartAngle=3.14159 EndAngle=6.28319
    g9: ArcOfCircle CenterX=-16.1 CenterY=-36.4 CenterZ=0 NormalX=0 NormalY=0 NormalZ=1 AngleXU=0 Radius=1.5 StartAngle=3.14159 EndAngle=6.28319
    g10: ArcOfCircle CenterX=-22.1 CenterY=-36.4 CenterZ=0 NormalX=0 NormalY=0 NormalZ=1 AngleXU=0 Radius=1.5 StartAngle=3.14159 EndAngle=6.28319
    g11: ArcOfCircle CenterX=-28.2 CenterY=-33.9 CenterZ=0 NormalX=0 NormalY=0 NormalZ=1 AngleXU=0 Radius=1.5 StartAngle=3.14159 EndAngle=6.28319
    g12: LineSegment StartX=-35.7 StartY=-10.5 StartZ=0 EndX=-35.7 EndY=-27.7 EndZ=0
    g13: LineSegment StartX=-32.7 StartY=-10.5 StartZ=0 EndX=-32.7 EndY=-27.7 EndZ=0
    g14: LineSegment StartX=-29.7 StartY=-33.9 StartZ=0 EndX=-29.7 EndY=-4.3 EndZ=0
    g15: LineSegment StartX=-26.7 StartY=-33.9 StartZ=0 EndX=-26.7 EndY=-4.3 EndZ=0
    g16: LineSegment StartX=-2.5 StartY=-10.5 StartZ=0 EndX=-2.5 EndY=-27.7 EndZ=0
    g17: LineSegment StartX=-8.5 StartY=-4.3 StartZ=0 EndX=-8.5 EndY=-33.9 EndZ=0
    g18: LineSegment StartX=-5.5 StartY=-10.5 StartZ=0 EndX=-5.5 EndY=-27.7 EndZ=0
    g19: LineSegment StartX=-11.5 StartY=-4.3 StartZ=0 EndX=-11.5 EndY=-33.9 EndZ=0
    g20: LineSegment StartX=-14.6 StartY=-1.8 StartZ=0 EndX=-14.6 EndY=-36.4 EndZ=0
    g21: LineSegment StartX=-17.6 StartY=-1.8 StartZ=0 EndX=-17.6 EndY=-36.4 EndZ=0
    g22: LineSegment StartX=-20.6 StartY=-36.4 StartZ=0 EndX=-20.6 EndY=-1.8 EndZ=0
    g23: LineSegment StartX=-23.6 StartY=-1.8 StartZ=0 EndX=-23.6 EndY=-36.4 EndZ=0
  constraints (48):
    c: Block(g0)
    c: Block(g1)
    c: Block(g2)
    c: Block(g3)
    c: Block(g4)
    c: Block(g5)
    c: Block(g6)
    c: Block(g7)
    c: Block(g8)
    c: Block(g9)
    c: Block(g10)
    c: Block(g11)
    c: Coincident(g12,g1)
    c: Coincident(g12,g2)
    c: Vertical(g12)
    c: Coincident(g13,g1)
    c: Coincident(g13,g2)
    c: Vertical(g13)
    c: Coincident(g14,g11)
    c: Coincident(g14,g7)
    c: Vertical(g14)
    c: Coincident(g15,g11)
    c: Coincident(g15,g7)
    c: Vertical(g15)
    c: Coincident(g16,g0)
    c: Coincident(g16,g3)
    c: Vertical(g16)
    c: Coincident(g17,g4)
    c: Coincident(g17,g8)
    c: Vertical(g17)
    c: Coincident(g18,g0)
    c: Coincident(g18,g3)
    c: Vertical(g18)
    c: Coincident(g19,g4)
    c: Coincident(g19,g8)
    c: Vertical(g19)
    c: Coincident(g20,g5)
    c: Coincident(g20,g9)
    c: Vertical(g20)
    c: Coincident(g21,g5)
    c: Coincident(g21,g9)
    c: Vertical(g21)
    c: Coincident(g22,g10)
    c: Coincident(g22,g6)
    c: Vertical(g22)
    c: Coincident(g23,g6)
    c: Coincident(g23,g10)
    c: Vertical(g23)
FEATURE [Part::Extrusion] Extrude048  label="removeToCreateFanGrillHoles004"
  Base = -> Sketch057
  Dir = (0,-1,6e-16)
  DirMode = 2
  FaceMakerClass = Part::FaceMakerBullseye
  LengthFwd = 10
  LengthRev = 0
  Placement = pos=(65.4,44,54.82) rot=(0,0,1;0rad)
  Solid = true
  Symmetric = false
FEATURE [Part::Cut] Cut040  label="top021"
  Base = -> Fillet039
  Tool = -> Extrude048
FEATURE [Part::Cylinder] Cylinder041  label="removeToCreteHoleForPlugHousing034"
  Angle = 360
  AttacherType = Attacher::AttachEngine3D
  Height = 20
  Placement = pos=(-2,19,36) rot=(0,1,0;1.5708rad)
  Radius = 14.3
FEATURE [Part::MultiFuse] Fusion089  label="removeToCreteHoleForPlugHousing035"
  Shapes = -> [Box026,Cylinder041]
FEATURE [Part::Cylinder] Cylinder042
  Angle = 360
  AttacherType = Attacher::AttachEngine3D
  Height = 20
  Placement = pos=(0,0,36.15) rot=(0,0,1;0rad)
  Radius = 14.3
FEATURE [Part::Cylinder] Cylinder043
  Angle = 360
  AttacherType = Attacher::AttachEngine3D
  Height = 10
  Placement = pos=(0,0,36.15) rot=(0,0,1;0rad)
  Radius = 4
FEATURE [Part::Box] Box027  label="removeToCreteHoleForPlugHousing036"
  AttacherType = Attacher::AttachEngine3D
  Height = 28.6
  Length = 20
  Placement = pos=(106.15,0,21.7) rot=(0,0,1;0rad)
  Width = 19
FEATURE [Part::Cut] Cut041  label="top022"
  Base = -> Cut040
  Tool = -> Fusion087
FEATURE [Part::Cut] Cut039  label="top020"
  Base = -> Cut041
  Tool = -> Fusion089
FEATURE [Part::MultiFuse] Fusion090  label="removeToCreteHoleForPlugHousing037"
  Placement = pos=(70,19,36) rot=(0,1,0;1.5708rad)
  Shapes = -> [Cylinder042,Cylinder043]
FEATURE [Part::MultiFuse] Fusion088  label="removeToCreteHoleForPlugHousing033"
  Shapes = -> [Box027,Fusion090]
FEATURE [Part::Cut] Cut042  label="removeToCreteHoleForPlugHousing038"
  Base = -> Cut039
  Tool = -> Fusion088
FEATURE [Part::MultiFuse] Fusion091  label="removeFromTop"
  Shapes = -> [Fillet038,Fusion085,Fusion084,Fusion083,Extrude045]
FEATURE [Part::Cut] Cut043  label="top026"
  Base = -> Fillet036
  Tool = -> Fusion091
FEATURE [Part::MultiFuse] Fusion092  label="caseScrewPillarBracket016"
  Shapes = -> [Extrude030,Extrude031,Extrude032,Extrude033,Extrude034,Extrude035,Extrude036,Extrude037,Box013,Box014]
FEATURE [Sketcher::SketchObject] Sketch058  label="topSketch015"
  FullyConstrained = true
  sketch-geometry (20):
    g0: LineSegment StartX=5.21097e-06 StartY=3 StartZ=0 EndX=5.21097e-06 EndY=19 EndZ=0
    g1: ArcOfCircle CenterX=19 CenterY=19 CenterZ=0 NormalX=0 NormalY=0 NormalZ=1 AngleXU=0 Radius=19 StartAngle=1.5708 EndAngle=3.14159
    g2: ArcOfCircle CenterX=19 CenterY=19 CenterZ=0 NormalX=0 NormalY=0 NormalZ=1 AngleXU=0 Radius=16 StartAngle=1.5708 EndAngle=3.14159
    g3: LineSegment StartX=114 StartY=35 StartZ=0 EndX=19 EndY=35 EndZ=0
    g4: LineSegment StartX=5.21097e-06 StartY=3 StartZ=0 EndX=5.21097e-06 EndY=0 EndZ=0
    g5: LineSegment StartX=3 StartY=0 StartZ=0 EndX=5.21097e-06 EndY=0 EndZ=0
    g6: LineSegment StartX=3 StartY=19 StartZ=0 EndX=3 EndY=0 EndZ=0
    g7: LineSegment StartX=19 StartY=38 StartZ=0 EndX=124 EndY=38 EndZ=0
    g8: Circle CenterX=119 CenterY=35 CenterZ=0 NormalX=0 NormalY=0 NormalZ=1 AngleXU=0 Radius=1
    g9: Circle CenterX=121 CenterY=35 CenterZ=0 NormalX=0 NormalY=0 NormalZ=1 AngleXU=0 Radius=1
    g10: Circle CenterX=121 CenterY=33 CenterZ=0 NormalX=0 NormalY=0 NormalZ=1 AngleXU=0 Radius=1
    g11: BSplineCurve PolesCount=3 KnotsCount=2 Degree=2 IsPeriodic=0
    g12: GeomPoint X=119 Y=35 Z=0
    g13: GeomPoint X=121 Y=33 Z=0
    g14: LineSegment StartX=119 StartY=35 StartZ=0 EndX=114 EndY=35 EndZ=0
    g15: ArcOfCircle CenterX=105 CenterY=19 CenterZ=0 NormalX=0 NormalY=0 NormalZ=1 AngleXU=0 Radius=19 StartAngle=5.7297 EndAngle=6.28319
    g16: ArcOfCircle CenterX=105 CenterY=19 CenterZ=0 NormalX=0 NormalY=0 NormalZ=1 AngleXU=0 Radius=16 StartAngle=5.60905 EndAngle=6.28319
    g17: LineSegment StartX=121 StartY=33 StartZ=0 EndX=121 EndY=19 EndZ=0
    g18: LineSegment StartX=124 StartY=38 StartZ=0 EndX=124 EndY=19 EndZ=0
    g19: LineSegment StartX=117.5 StartY=9.01251 StartZ=0 EndX=121.163 EndY=9.0125 EndZ=0
  constraints (46):
    c: Vertical(g0)
    c: Block(g0)
    c: Coincident(g1,g0)
    c: Block(g1)
    c: Coincident(g2,g1)
    c: Block(g2)
    c: Coincident(g3,g2)
    c: Horizontal(g3)
    c: Tangent(g3,g2)
    c: Coincident(g4,g0)
    c: Distance(g4) = 3
    c: Vertical(g4)
    c: Coincident(g5,g4)
    c: Horizontal(g5)
    c: Coincident(g6,g2)
    c: Coincident(g6,g5)
    c: Vertical(g6)
    c: Horizontal(g7)
    c: Distance(g7) = 105
    c: Coincident(g7,g1)
    c: Block(g3)
    c: Weight(g8) = 1
    c: Equal(g8,g9)
    c: Equal(g8,g10)
    c: InternalAlignment(g8,g11)
    c: InternalAlignment(g9,g11)
    c: InternalAlignment(g10,g11)
    c: InternalAlignment(g12,g11)
    c: InternalAlignment(g13,g11)
    c: Block(g11)
    c: Coincident(g14,g11)
    c: Coincident(g14,g3)
    c: Horizontal(g14)
    c: Block(g15)
    c: Coincident(g16,g15)
    c: Block(g16)
    c: Coincident(g17,g11)
    c: Coincident(g17,g16)
    c: Vertical(g17)
    c: Distance(g17) = 14
    c: Coincident(g18,g7)
    c: Coincident(g18,g15)
    c: Vertical(g18)
    c: Distance(g18) = 19
    c: Coincident(g19,g16)
    c: Coincident(g19,g15)
FEATURE [Part::Extrusion] Extrude049  label="top023"
  Base = -> Sketch058
  Dir = (0,0,1)
  DirMode = 2
  FaceMakerClass = Part::FaceMakerBullseye
  LengthFwd = 72
  LengthRev = 0
  Solid = true
  Symmetric = false
FEATURE [Sketcher::SketchObject] Sketch059
  FullyConstrained = true
  MapMode = 3
  Placement = pos=(0,0,0) rot=(1,0,0;1.5708rad)
  Support = -> [Extrude049]
  sketch-geometry (8):
    g0: Circle CenterX=80.351 CenterY=-67.6202 CenterZ=0 NormalX=0 NormalY=0 NormalZ=1 AngleXU=0 Radius=2
    g1: Circle CenterX=80.351 CenterY=-67.6202 CenterZ=0 NormalX=0 NormalY=0 NormalZ=1 AngleXU=0 Radius=3
    g2: Circle CenterX=80.351 CenterY=-4.92017 CenterZ=0 NormalX=0 NormalY=0 NormalZ=1 AngleXU=0 Radius=2
    g3: Circle CenterX=80.351 CenterY=-4.92017 CenterZ=0 NormalX=0 NormalY=0 NormalZ=1 AngleXU=0 Radius=3
    g4: Circle CenterX=23.851 CenterY=-4.92017 CenterZ=0 NormalX=0 NormalY=0 NormalZ=1 AngleXU=0 Radius=2
    g5: Circle CenterX=23.851 CenterY=-4.92017 CenterZ=0 NormalX=0 NormalY=0 NormalZ=1 AngleXU=0 Radius=3
    g6: Circle CenterX=23.851 CenterY=-67.6202 CenterZ=0 NormalX=0 NormalY=0 NormalZ=1 AngleXU=0 Radius=2
    g7: Circle CenterX=23.851 CenterY=-67.6202 CenterZ=0 NormalX=0 NormalY=0 NormalZ=1 AngleXU=0 Radius=3
  constraints (8):
    c: Block(g3)
    c: Block(g2)
    c: Block(g1)
    c: Block(g0)
    c: Block(g6)
    c: Block(g7)
    c: Block(g4)
    c: Block(g5)
FEATURE [Sketcher::SketchObject] Sketch060
  FullyConstrained = true
  MapMode = 3
  Placement = pos=(0,0,0) rot=(1,0,0;1.5708rad)
  Support = -> [Extrude049]
  sketch-geometry (8):
    g0: Circle CenterX=80.351 CenterY=-67.6202 CenterZ=0 NormalX=0 NormalY=0 NormalZ=1 AngleXU=0 Radius=3
    g1: Circle CenterX=80.351 CenterY=-4.92017 CenterZ=0 NormalX=0 NormalY=0 NormalZ=1 AngleXU=0 Radius=3
    g2: Circle CenterX=23.851 CenterY=-4.92017 CenterZ=0 NormalX=0 NormalY=0 NormalZ=1 AngleXU=0 Radius=3
    g3: Circle CenterX=23.851 CenterY=-67.6202 CenterZ=0 NormalX=0 NormalY=0 NormalZ=1 AngleXU=0 Radius=3
    g4: Circle CenterX=23.851 CenterY=-67.6202 CenterZ=0 NormalX=0 NormalY=0 NormalZ=1 AngleXU=0 Radius=5
    g5: Circle CenterX=80.351 CenterY=-67.6202 CenterZ=0 NormalX=0 NormalY=0 NormalZ=1 AngleXU=0 Radius=5
    g6: Circle CenterX=23.851 CenterY=-4.92017 CenterZ=0 NormalX=0 NormalY=0 NormalZ=1 AngleXU=0 Radius=5
    g7: Circle CenterX=80.351 CenterY=-4.92017 CenterZ=0 NormalX=0 NormalY=0 NormalZ=1 AngleXU=0 Radius=5
  constraints (8):
    c: Block(g1)
    c: Block(g0)
    c: Block(g3)
    c: Block(g2)
    c: Block(g5)
    c: Block(g4)
    c: Block(g6)
    c: Block(g7)
FEATURE [Sketcher::SketchObject] Sketch061
  FullyConstrained = true
  MapMode = 3
  Placement = pos=(0,0,0) rot=(1,0,0;1.5708rad)
  sketch-geometry (8):
    g0: Circle CenterX=80.351 CenterY=-67.6202 CenterZ=0 NormalX=0 NormalY=0 NormalZ=1 AngleXU=0 Radius=3
    g1: Circle CenterX=80.351 CenterY=-4.92017 CenterZ=0 NormalX=0 NormalY=0 NormalZ=1 AngleXU=0 Radius=3
    g2: Circle CenterX=23.851 CenterY=-4.92017 CenterZ=0 NormalX=0 NormalY=0 NormalZ=1 AngleXU=0 Radius=3
    g3: Circle CenterX=23.851 CenterY=-67.6202 CenterZ=0 NormalX=0 NormalY=0 NormalZ=1 AngleXU=0 Radius=3
    g4: Circle CenterX=23.851 CenterY=-67.6202 CenterZ=0 NormalX=0 NormalY=0 NormalZ=1 AngleXU=0 Radius=5
    g5: Circle CenterX=80.351 CenterY=-67.6202 CenterZ=0 NormalX=0 NormalY=0 NormalZ=1 AngleXU=0 Radius=5
    g6: Circle CenterX=23.851 CenterY=-4.92017 CenterZ=0 NormalX=0 NormalY=0 NormalZ=1 AngleXU=0 Radius=5
    g7: Circle CenterX=80.351 CenterY=-4.92017 CenterZ=0 NormalX=0 NormalY=0 NormalZ=1 AngleXU=0 Radius=5
  constraints (8):
    c: Block(g1)
    c: Block(g0)
    c: Block(g3)
    c: Block(g2)
    c: Block(g5)
    c: Block(g4)
    c: Block(g6)
    c: Block(g7)
FEATURE [Sketcher::SketchObject] Sketch062  label="topSketch016"
  FullyConstrained = true
  sketch-geometry (20):
    g0: LineSegment StartX=5.21097e-06 StartY=3 StartZ=0 EndX=5.21097e-06 EndY=19 EndZ=0
    g1: ArcOfCircle CenterX=19 CenterY=19 CenterZ=0 NormalX=0 NormalY=0 NormalZ=1 AngleXU=0 Radius=19 StartAngle=1.5708 EndAngle=3.14159
    g2: ArcOfCircle CenterX=19 CenterY=19 CenterZ=0 NormalX=0 NormalY=0 NormalZ=1 AngleXU=0 Radius=16 StartAngle=1.5708 EndAngle=3.14159
    g3: LineSegment StartX=114 StartY=35 StartZ=0 EndX=19 EndY=35 EndZ=0
    g4: LineSegment StartX=5.21097e-06 StartY=3 StartZ=0 EndX=5.21097e-06 EndY=0 EndZ=0
    g5: LineSegment StartX=3 StartY=0 StartZ=0 EndX=5.21097e-06 EndY=0 EndZ=0
    g6: LineSegment StartX=3 StartY=19 StartZ=0 EndX=3 EndY=0 EndZ=0
    g7: LineSegment StartX=19 StartY=38 StartZ=0 EndX=124 EndY=38 EndZ=0
    g8: Circle CenterX=119 CenterY=35 CenterZ=0 NormalX=0 NormalY=0 NormalZ=1 AngleXU=0 Radius=1
    g9: Circle CenterX=121 CenterY=35 CenterZ=0 NormalX=0 NormalY=0 NormalZ=1 AngleXU=0 Radius=1
    g10: Circle CenterX=121 CenterY=33 CenterZ=0 NormalX=0 NormalY=0 NormalZ=1 AngleXU=0 Radius=1
    g11: BSplineCurve PolesCount=3 KnotsCount=2 Degree=2 IsPeriodic=0
    g12: GeomPoint X=119 Y=35 Z=0
    g13: GeomPoint X=121 Y=33 Z=0
    g14: LineSegment StartX=119 StartY=35 StartZ=0 EndX=114 EndY=35 EndZ=0
    g15: ArcOfCircle CenterX=105 CenterY=19 CenterZ=0 NormalX=0 NormalY=0 NormalZ=1 AngleXU=0 Radius=19 StartAngle=5.7297 EndAngle=6.28319
    g16: ArcOfCircle CenterX=105 CenterY=19 CenterZ=0 NormalX=0 NormalY=0 NormalZ=1 AngleXU=0 Radius=16 StartAngle=5.60905 EndAngle=6.28319
    g17: LineSegment StartX=121 StartY=33 StartZ=0 EndX=121 EndY=19 EndZ=0
    g18: LineSegment StartX=124 StartY=38 StartZ=0 EndX=124 EndY=19 EndZ=0
    g19: LineSegment StartX=117.5 StartY=9.01251 StartZ=0 EndX=121.163 EndY=9.0125 EndZ=0
  constraints (46):
    c: Vertical(g0)
    c: Block(g0)
    c: Coincident(g1,g0)
    c: Block(g1)
    c: Coincident(g2,g1)
    c: Block(g2)
    c: Coincident(g3,g2)
    c: Horizontal(g3)
    c: Tangent(g3,g2)
    c: Coincident(g4,g0)
    c: Distance(g4) = 3
    c: Vertical(g4)
    c: Coincident(g5,g4)
    c: Horizontal(g5)
    c: Coincident(g6,g2)
    c: Coincident(g6,g5)
    c: Vertical(g6)
    c: Horizontal(g7)
    c: Distance(g7) = 105
    c: Coincident(g7,g1)
    c: Block(g3)
    c: Weight(g8) = 1
    c: Equal(g8,g9)
    c: Equal(g8,g10)
    c: InternalAlignment(g8,g11)
    c: InternalAlignment(g9,g11)
    c: InternalAlignment(g10,g11)
    c: InternalAlignment(g12,g11)
    c: InternalAlignment(g13,g11)
    c: Block(g11)
    c: Coincident(g14,g11)
    c: Coincident(g14,g3)
    c: Horizontal(g14)
    c: Block(g15)
    c: Coincident(g16,g15)
    c: Block(g16)
    c: Coincident(g17,g11)
    c: Coincident(g17,g16)
    c: Vertical(g17)
    c: Distance(g17) = 14
    c: Coincident(g18,g7)
    c: Coincident(g18,g15)
    c: Vertical(g18)
    c: Distance(g18) = 19
    c: Coincident(g19,g16)
    c: Coincident(g19,g15)
FEATURE [Part::Extrusion] Extrude053  label="top024"
  Base = -> Sketch062
  Dir = (0,0,1)
  DirMode = 2
  FaceMakerClass = Part::FaceMakerBullseye
  LengthFwd = 72
  LengthRev = 0
  Solid = true
  Symmetric = false
FEATURE [Sketcher::SketchObject] Sketch063
  FullyConstrained = true
  MapMode = 3
  Placement = pos=(0,0,0) rot=(1,0,0;1.5708rad)
  Support = -> [Extrude053]
  sketch-geometry (8):
    g0: Circle CenterX=80.351 CenterY=-67.6202 CenterZ=0 NormalX=0 NormalY=0 NormalZ=1 AngleXU=0 Radius=2
    g1: Circle CenterX=80.351 CenterY=-67.6202 CenterZ=0 NormalX=0 NormalY=0 NormalZ=1 AngleXU=0 Radius=3
    g2: Circle CenterX=80.351 CenterY=-4.92017 CenterZ=0 NormalX=0 NormalY=0 NormalZ=1 AngleXU=0 Radius=2
    g3: Circle CenterX=80.351 CenterY=-4.92017 CenterZ=0 NormalX=0 NormalY=0 NormalZ=1 AngleXU=0 Radius=3
    g4: Circle CenterX=23.851 CenterY=-4.92017 CenterZ=0 NormalX=0 NormalY=0 NormalZ=1 AngleXU=0 Radius=2
    g5: Circle CenterX=23.851 CenterY=-4.92017 CenterZ=0 NormalX=0 NormalY=0 NormalZ=1 AngleXU=0 Radius=3
    g6: Circle CenterX=23.851 CenterY=-67.6202 CenterZ=0 NormalX=0 NormalY=0 NormalZ=1 AngleXU=0 Radius=2
    g7: Circle CenterX=23.851 CenterY=-67.6202 CenterZ=0 NormalX=0 NormalY=0 NormalZ=1 AngleXU=0 Radius=3
  constraints (8):
    c: Block(g3)
    c: Block(g2)
    c: Block(g1)
    c: Block(g0)
    c: Block(g6)
    c: Block(g7)
    c: Block(g4)
    c: Block(g5)
FEATURE [Part::Extrusion] Extrude054
  Base = -> Sketch063
  Dir = (0,-1,2e-16)
  DirMode = 2
  FaceMakerClass = Part::FaceMakerBullseye
  LengthFwd = 6
  LengthRev = 0
  Placement = pos=(0,9,0) rot=(0,0,1;0rad)
  Solid = true
  Symmetric = false
FEATURE [Sketcher::SketchObject] Sketch064  label="topSketch017"
  FullyConstrained = true
  sketch-geometry (20):
    g0: LineSegment StartX=5.21097e-06 StartY=3 StartZ=0 EndX=5.21097e-06 EndY=19 EndZ=0
    g1: ArcOfCircle CenterX=19 CenterY=19 CenterZ=0 NormalX=0 NormalY=0 NormalZ=1 AngleXU=0 Radius=19 StartAngle=1.5708 EndAngle=3.14159
    g2: ArcOfCircle CenterX=19 CenterY=19 CenterZ=0 NormalX=0 NormalY=0 NormalZ=1 AngleXU=0 Radius=16 StartAngle=1.5708 EndAngle=3.14159
    g3: LineSegment StartX=114 StartY=35 StartZ=0 EndX=19 EndY=35 EndZ=0
    g4: LineSegment StartX=5.21097e-06 StartY=3 StartZ=0 EndX=5.21097e-06 EndY=0 EndZ=0
    g5: LineSegment StartX=3 StartY=0 StartZ=0 EndX=5.21097e-06 EndY=0 EndZ=0
    g6: LineSegment StartX=3 StartY=19 StartZ=0 EndX=3 EndY=0 EndZ=0
    g7: LineSegment StartX=19 StartY=38 StartZ=0 EndX=124 EndY=38 EndZ=0
    g8: Circle CenterX=119 CenterY=35 CenterZ=0 NormalX=0 NormalY=0 NormalZ=1 AngleXU=0 Radius=1
    g9: Circle CenterX=121 CenterY=35 CenterZ=0 NormalX=0 NormalY=0 NormalZ=1 AngleXU=0 Radius=1
    g10: Circle CenterX=121 CenterY=33 CenterZ=0 NormalX=0 NormalY=0 NormalZ=1 AngleXU=0 Radius=1
    g11: BSplineCurve PolesCount=3 KnotsCount=2 Degree=2 IsPeriodic=0
    g12: GeomPoint X=119 Y=35 Z=0
    g13: GeomPoint X=121 Y=33 Z=0
    g14: LineSegment StartX=119 StartY=35 StartZ=0 EndX=114 EndY=35 EndZ=0
    g15: ArcOfCircle CenterX=105 CenterY=19 CenterZ=0 NormalX=0 NormalY=0 NormalZ=1 AngleXU=0 Radius=19 StartAngle=5.7297 EndAngle=6.28319
    g16: ArcOfCircle CenterX=105 CenterY=19 CenterZ=0 NormalX=0 NormalY=0 NormalZ=1 AngleXU=0 Radius=16 StartAngle=5.60905 EndAngle=6.28319
    g17: LineSegment StartX=121 StartY=33 StartZ=0 EndX=121 EndY=19 EndZ=0
    g18: LineSegment StartX=124 StartY=38 StartZ=0 EndX=124 EndY=19 EndZ=0
    g19: LineSegment StartX=117.5 StartY=9.01251 StartZ=0 EndX=121.163 EndY=9.0125 EndZ=0
  constraints (46):
    c: Vertical(g0)
    c: Block(g0)
    c: Coincident(g1,g0)
    c: Block(g1)
    c: Coincident(g2,g1)
    c: Block(g2)
    c: Coincident(g3,g2)
    c: Horizontal(g3)
    c: Tangent(g3,g2)
    c: Coincident(g4,g0)
    c: Distance(g4) = 3
    c: Vertical(g4)
    c: Coincident(g5,g4)
    c: Horizontal(g5)
    c: Coincident(g6,g2)
    c: Coincident(g6,g5)
    c: Vertical(g6)
    c: Horizontal(g7)
    c: Distance(g7) = 105
    c: Coincident(g7,g1)
    c: Block(g3)
    c: Weight(g8) = 1
    c: Equal(g8,g9)
    c: Equal(g8,g10)
    c: InternalAlignment(g8,g11)
    c: InternalAlignment(g9,g11)
    c: InternalAlignment(g10,g11)
    c: InternalAlignment(g12,g11)
    c: InternalAlignment(g13,g11)
    c: Block(g11)
    c: Coincident(g14,g11)
    c: Coincident(g14,g3)
    c: Horizontal(g14)
    c: Block(g15)
    c: Coincident(g16,g15)
    c: Block(g16)
    c: Coincident(g17,g11)
    c: Coincident(g17,g16)
    c: Vertical(g17)
    c: Distance(g17) = 14
    c: Coincident(g18,g7)
    c: Coincident(g18,g15)
    c: Vertical(g18)
    c: Distance(g18) = 19
    c: Coincident(g19,g16)
    c: Coincident(g19,g15)
FEATURE [Sketcher::SketchObject] Sketch065
  FullyConstrained = true
  MapMode = 3
  Placement = pos=(0,0,0) rot=(1,0,0;1.5708rad)
  sketch-geometry (8):
    g0: Circle CenterX=80.351 CenterY=-67.6202 CenterZ=0 NormalX=0 NormalY=0 NormalZ=1 AngleXU=0 Radius=3
    g1: Circle CenterX=80.351 CenterY=-4.92017 CenterZ=0 NormalX=0 NormalY=0 NormalZ=1 AngleXU=0 Radius=3
    g2: Circle CenterX=23.851 CenterY=-4.92017 CenterZ=0 NormalX=0 NormalY=0 NormalZ=1 AngleXU=0 Radius=3
    g3: Circle CenterX=23.851 CenterY=-67.6202 CenterZ=0 NormalX=0 NormalY=0 NormalZ=1 AngleXU=0 Radius=3
    g4: Circle CenterX=23.851 CenterY=-67.6202 CenterZ=0 NormalX=0 NormalY=0 NormalZ=1 AngleXU=0 Radius=5
    g5: Circle CenterX=80.351 CenterY=-67.6202 CenterZ=0 NormalX=0 NormalY=0 NormalZ=1 AngleXU=0 Radius=5
    g6: Circle CenterX=23.851 CenterY=-4.92017 CenterZ=0 NormalX=0 NormalY=0 NormalZ=1 AngleXU=0 Radius=5
    g7: Circle CenterX=80.351 CenterY=-4.92017 CenterZ=0 NormalX=0 NormalY=0 NormalZ=1 AngleXU=0 Radius=5
  constraints (8):
    c: Block(g1)
    c: Block(g0)
    c: Block(g3)
    c: Block(g2)
    c: Block(g5)
    c: Block(g4)
    c: Block(g6)
    c: Block(g7)
FEATURE [Part::Extrusion] Extrude056
  Base = -> Sketch065
  Dir = (0,-1,2e-16)
  DirMode = 2
  FaceMakerClass = Part::FaceMakerBullseye
  LengthFwd = 2
  LengthRev = 0
  Solid = true
  Symmetric = false
FEATURE [Part::Extrusion] Extrude057  label="top025"
  Base = -> Sketch064
  Dir = (0,0,1)
  DirMode = 2
  FaceMakerClass = Part::FaceMakerBullseye
  LengthFwd = 72
  LengthRev = 0
  Solid = true
  Symmetric = false
FEATURE [Sketcher::SketchObject] Sketch066
  FullyConstrained = true
  MapMode = 3
  Placement = pos=(0,0,0) rot=(1,0,0;1.5708rad)
  Support = -> [Extrude057]
  sketch-geometry (8):
    g0: Circle CenterX=80.351 CenterY=-67.6202 CenterZ=0 NormalX=0 NormalY=0 NormalZ=1 AngleXU=0 Radius=3
    g1: Circle CenterX=80.351 CenterY=-4.92017 CenterZ=0 NormalX=0 NormalY=0 NormalZ=1 AngleXU=0 Radius=3
    g2: Circle CenterX=23.851 CenterY=-4.92017 CenterZ=0 NormalX=0 NormalY=0 NormalZ=1 AngleXU=0 Radius=3
    g3: Circle CenterX=23.851 CenterY=-67.6202 CenterZ=0 NormalX=0 NormalY=0 NormalZ=1 AngleXU=0 Radius=3
    g4: Circle CenterX=23.851 CenterY=-67.6202 CenterZ=0 NormalX=0 NormalY=0 NormalZ=1 AngleXU=0 Radius=5
    g5: Circle CenterX=80.351 CenterY=-67.6202 CenterZ=0 NormalX=0 NormalY=0 NormalZ=1 AngleXU=0 Radius=5
    g6: Circle CenterX=23.851 CenterY=-4.92017 CenterZ=0 NormalX=0 NormalY=0 NormalZ=1 AngleXU=0 Radius=5
    g7: Circle CenterX=80.351 CenterY=-4.92017 CenterZ=0 NormalX=0 NormalY=0 NormalZ=1 AngleXU=0 Radius=5
  constraints (8):
    c: Block(g1)
    c: Block(g0)
    c: Block(g3)
    c: Block(g2)
    c: Block(g5)
    c: Block(g4)
    c: Block(g6)
    c: Block(g7)
FEATURE [Part::Extrusion] Extrude055
  Base = -> Sketch066
  Dir = (0,-1,2e-16)
  DirMode = 2
  FaceMakerClass = Part::FaceMakerBullseye
  LengthFwd = 2
  LengthRev = 0
  Solid = true
  Symmetric = false
FEATURE [Part::Fillet] Fillet041
  Base = -> Extrude056
  Edges = 4 edges r=1.99: [Edge6,Edge12,Edge18,Edge24]
FEATURE [Part::Cut] Cut045
  Base = -> Extrude055
  Placement = pos=(0,6,0) rot=(0,0,1;0rad)
  Tool = -> Fillet041
FEATURE [Part::MultiFuse] Fusion095  label="pcbScrewPillars"
  Placement = pos=(-3.2,-1,72.3) rot=(0,0,1;0rad)
  Shapes = -> [Cut045,Extrude054]
FEATURE [Part::Feature] Face113
  shape: bbox 3.2 x 1.5 x 2e-07 mm, 1 faces, 0 solids (baked)
FEATURE [Part::Revolution] Revolve121  label="backCaseScrewRetainer002"
  Angle = 360
  Axis = (0,1,0)
  Base = (0,0,0)
  FaceMakerClass = Part::FaceMakerBullseye
  Placement = pos=(12.5,3,62) rot=(0,0,1;0rad)
  Solid = false
  Source = -> Face113
  Symmetric = false
FEATURE [Part::Feature] Face114
  shape: bbox 3.2 x 1.5 x 2e-07 mm, 1 faces, 0 solids (baked)
FEATURE [Part::Feature] Face115
  shape: bbox 3.2 x 1.5 x 2e-07 mm, 1 faces, 0 solids (baked)
FEATURE [Part::Feature] Face116
  shape: bbox 3.2 x 1.5 x 2e-07 mm, 1 faces, 0 solids (baked)
FEATURE [Part::Revolution] Revolve122  label="frontCaseScrewRetainer004"
  Angle = 360
  Axis = (0,1,0)
  Base = (0,0,0)
  FaceMakerClass = Part::FaceMakerBullseye
  Placement = pos=(89.5,3,68.5) rot=(0,0,1;0rad)
  Solid = false
  Source = -> Face115
  Symmetric = false
FEATURE [Part::Revolution] Revolve123  label="frontCaseScrewRetainer005"
  Angle = 360
  Axis = (0,1,0)
  Base = (0,0,0)
  FaceMakerClass = Part::FaceMakerBullseye
  Placement = pos=(89.5,3,3.5) rot=(0,0,1;0rad)
  Solid = false
  Source = -> Face116
  Symmetric = false
FEATURE [Part::Revolution] Revolve124  label="backCaseScrewRetainer003"
  Angle = 360
  Axis = (0,1,0)
  Base = (0,0,0)
  FaceMakerClass = Part::FaceMakerBullseye
  Placement = pos=(12.5,3,10) rot=(0,0,1;0rad)
  Solid = false
  Source = -> Face114
  Symmetric = false
FEATURE [Part::Feature] Face117
  shape: bbox 3.6 x 3.2 x 2e-07 mm, 1 faces, 0 solids (baked)
FEATURE [Part::Revolution] Revolve125  label="moreFrontCaseScrewRetainer004"
  Angle = 360
  Axis = (0,1,0)
  Base = (0,0,0)
  FaceMakerClass = Part::FaceMakerBullseye
  Placement = pos=(109.5,4.5,68.5) rot=(0,0,1;0rad)
  Solid = false
  Source = -> Face117
  Symmetric = false
FEATURE [Part::Feature] Face118
  shape: bbox 3.6 x 3.2 x 2e-07 mm, 1 faces, 0 solids (baked)
FEATURE [Part::Revolution] Revolve126  label="moreFrontCaseScrewRetainer005"
  Angle = 360
  Axis = (0,1,0)
  Base = (0,0,0)
  FaceMakerClass = Part::FaceMakerBullseye
  Placement = pos=(109.5,4.5,3.5) rot=(0,0,1;0rad)
  Solid = false
  Source = -> Face118
  Symmetric = false
FEATURE [Part::MultiFuse] Fusion096  label="screwRetainers001"
  Shapes = -> [Revolve126,Revolve125,Revolve124,Revolve123,Revolve122,Revolve121]
FEATURE [Part::Feature] Face119
  shape: bbox 10 x 16.5 x 2e-07 mm, 1 faces, 0 solids (baked)
FEATURE [Part::Revolution] Revolve130  label="plugHousing050"
  Angle = 360
  Axis = (0,1,0)
  Base = (0,0,0)
  FaceMakerClass = Part::FaceMakerBullseye
  Placement = pos=(0,0,36.15) rot=(0,0,1;0rad)
  Solid = false
  Source = -> Face119
  Symmetric = false
FEATURE [Part::Feature] Face120
  shape: bbox 10 x 16.5 x 2e-07 mm, 1 faces, 0 solids (baked)
FEATURE [Part::Feature] Face121
  shape: bbox 10 x 16.5 x 2e-07 mm, 1 faces, 0 solids (baked)
FEATURE [Part::Revolution] Revolve127  label="plugHousing047"
  Angle = 360
  Axis = (0,1,0)
  Base = (0,0,0)
  FaceMakerClass = Part::FaceMakerBullseye
  Placement = pos=(0,0,36.15) rot=(0,0,1;0rad)
  Solid = false
  Source = -> Face121
  Symmetric = false
FEATURE [Part::Feature] Face122
  shape: bbox 10 x 16.5 x 2e-07 mm, 1 faces, 0 solids (baked)
FEATURE [Part::Feature] Face123
  shape: bbox 10 x 16.5 x 2e-07 mm, 1 faces, 0 solids (baked)
FEATURE [Part::Revolution] Revolve128  label="plugHousing048"
  Angle = 360
  Axis = (0,1,0)
  Base = (0,0,0)
  FaceMakerClass = Part::FaceMakerBullseye
  Placement = pos=(0,0,36.15) rot=(0,0,1;0rad)
  Solid = false
  Source = -> Face123
  Symmetric = false
FEATURE [Part::MultiFuse] Fusion100  label="plugHousing054"
  Placement = pos=(0,0,0) rot=(0,0,1;1.5708rad)
  Shapes = -> [Revolve130,Revolve128]
FEATURE [Part::Feature] Face124
  shape: bbox 10 x 16.5 x 2e-07 mm, 1 faces, 0 solids (baked)
FEATURE [Part::Feature] Face125
  shape: bbox 10 x 16.5 x 2e-07 mm, 1 faces, 0 solids (baked)
FEATURE [Part::Revolution] Revolve129  label="plugHousing049"
  Angle = 360
  Axis = (0,1,0)
  Base = (0,0,0)
  FaceMakerClass = Part::FaceMakerBullseye
  Placement = pos=(0,0,36.15) rot=(0,0,1;0rad)
  Solid = false
  Source = -> Face125
  Symmetric = false
FEATURE [Part::Feature] Face126
  shape: bbox 10 x 16.5 x 2e-07 mm, 1 faces, 0 solids (baked)
FEATURE [Part::Revolution] Revolve131  label="plugHousing058"
  Angle = 360
  Axis = (0,1,0)
  Base = (0,0,0)
  FaceMakerClass = Part::FaceMakerBullseye
  Placement = pos=(0,0,36.15) rot=(0,0,1;0rad)
  Solid = false
  Source = -> Face120
  Symmetric = false
FEATURE [Part::MultiFuse] Fusion099  label="plugHousing053"
  Placement = pos=(0,0,0) rot=(0,0,1;1.5708rad)
  Shapes = -> [Revolve127,Revolve131]
FEATURE [Part::MultiFuse] Fusion102  label="plugHousing056"
  Placement = pos=(0,19,0) rot=(0,0,1;3.14159rad)
  Shapes = -> [Fusion100,Fusion099]
FEATURE [Part::Revolution] Revolve132  label="plugHousing059"
  Angle = 360
  Axis = (0,1,0)
  Base = (0,0,0)
  FaceMakerClass = Part::FaceMakerBullseye
  Placement = pos=(0,0,36.15) rot=(0,0,1;0rad)
  Solid = false
  Source = -> Face126
  Symmetric = false
FEATURE [Part::Revolution] Revolve133  label="plugHousing060"
  Angle = 360
  Axis = (0,1,0)
  Base = (0,0,0)
  FaceMakerClass = Part::FaceMakerBullseye
  Placement = pos=(0,0,36.15) rot=(0,0,1;0rad)
  Solid = false
  Source = -> Face122
  Symmetric = false
FEATURE [Part::MultiFuse] Fusion097  label="plugHousing051"
  Placement = pos=(0,0,0) rot=(0,0,1;1.5708rad)
  Shapes = -> [Revolve133,Revolve132]
FEATURE [Part::Revolution] Revolve134  label="plugHousing061"
  Angle = 360
  Axis = (0,1,0)
  Base = (0,0,0)
  FaceMakerClass = Part::FaceMakerBullseye
  Placement = pos=(0,0,36.15) rot=(0,0,1;0rad)
  Solid = false
  Source = -> Face124
  Symmetric = false
FEATURE [Part::MultiFuse] Fusion101  label="plugHousing055"
  Placement = pos=(0,0,0) rot=(0,0,1;1.5708rad)
  Shapes = -> [Revolve129,Revolve134]
FEATURE [Part::MultiFuse] Fusion098  label="plugHousing052"
  Placement = pos=(0,19,0) rot=(0,0,1;3.14159rad)
  Shapes = -> [Fusion097,Fusion101]
FEATURE [Part::MultiFuse] Fusion103  label="plugHousing057"
  Placement = pos=(122.621,0,-0.15) rot=(0,0,1;0rad)
  Shapes = -> [Fusion102,Fusion098]
FEATURE [Part::Box] Box028  label="Cube015"
  AttacherType = Attacher::AttachEngine3D
  Height = 28
  Length = 3
  Placement = pos=(110.7,19,22) rot=(0,0,1;0rad)
  Width = 15.7
FEATURE [Part::Cylinder] Cylinder044
  Angle = 360
  AttacherType = Attacher::AttachEngine3D
  Height = 20
  Placement = pos=(0,0,36.15) rot=(0,0,1;0rad)
  Radius = 10.3
FEATURE [Part::Cylinder] Cylinder045
  Angle = 360
  AttacherType = Attacher::AttachEngine3D
  Height = 10
  Placement = pos=(0,0,36.15) rot=(0,0,1;0rad)
  Radius = 4
FEATURE [Part::MultiFuse] Fusion104  label="removeToCreteHoleForPlugHousing040"
  Placement = pos=(70,19,36) rot=(0,1,0;1.5708rad)
  Shapes = -> [Cylinder044,Cylinder045]
FEATURE [Part::Cut] Cut046  label="plugHousingTab003"
  Base = -> Box028
  Tool = -> Fusion104
FEATURE [Part::MultiFuse] Fusion105  label="plugHousing062"
  Shapes = -> [Fusion103,Cut046]
FEATURE [Part::Fillet] Fillet042
  Base = -> Fusion105
  Edges = 1 edges r=2: [Edge25]
FEATURE [Part::Fillet] Fillet043  label="plugHousing063"
  Base = -> Fillet042
  Edges = 1 edges r=2: [Edge8]
  Placement = pos=(7,0,0) rot=(0,0,1;0rad)
FEATURE [Part::Feature] Face127
  shape: bbox 10 x 16.5 x 2e-07 mm, 1 faces, 0 solids (baked)
FEATURE [Part::Feature] Face128
  shape: bbox 10 x 16.5 x 2e-07 mm, 1 faces, 0 solids (baked)
FEATURE [Part::Revolution] Revolve137  label="plugHousing070"
  Angle = 360
  Axis = (0,1,0)
  Base = (0,0,0)
  FaceMakerClass = Part::FaceMakerBullseye
  Placement = pos=(0,0,36.15) rot=(0,0,1;0rad)
  Solid = false
  Source = -> Face127
  Symmetric = false
FEATURE [Part::Revolution] Revolve140  label="plugHousing073"
  Angle = 360
  Axis = (0,1,0)
  Base = (0,0,0)
  FaceMakerClass = Part::FaceMakerBullseye
  Placement = pos=(0,0,36.15) rot=(0,0,1;0rad)
  Solid = false
  Source = -> Face128
  Symmetric = false
FEATURE [Part::Feature] Face129
  shape: bbox 10 x 16.5 x 2e-07 mm, 1 faces, 0 solids (baked)
FEATURE [Part::Revolution] Revolve138  label="plugHousing071"
  Angle = 360
  Axis = (0,1,0)
  Base = (0,0,0)
  FaceMakerClass = Part::FaceMakerBullseye
  Placement = pos=(0,0,36.15) rot=(0,0,1;0rad)
  Solid = false
  Source = -> Face129
  Symmetric = false
FEATURE [Part::Feature] Face130
  shape: bbox 10 x 16.5 x 2e-07 mm, 1 faces, 0 solids (baked)
FEATURE [Part::Revolution] Revolve139  label="plugHousing072"
  Angle = 360
  Axis = (0,1,0)
  Base = (0,0,0)
  FaceMakerClass = Part::FaceMakerBullseye
  Placement = pos=(0,0,36.15) rot=(0,0,1;0rad)
  Solid = false
  Source = -> Face130
  Symmetric = false
FEATURE [Part::Feature] Face131
  shape: bbox 10 x 16.5 x 2e-07 mm, 1 faces, 0 solids (baked)
FEATURE [Part::Revolution] Revolve135  label="plugHousing068"
  Angle = 360
  Axis = (0,1,0)
  Base = (0,0,0)
  FaceMakerClass = Part::FaceMakerBullseye
  Placement = pos=(0,0,36.15) rot=(0,0,1;0rad)
  Solid = false
  Source = -> Face131
  Symmetric = false
FEATURE [Part::MultiFuse] Fusion112  label="plugHousing078"
  Placement = pos=(0,0,0) rot=(0,0,1;1.5708rad)
  Shapes = -> [Revolve135,Revolve139]
FEATURE [Part::Feature] Face132
  shape: bbox 10 x 16.5 x 2e-07 mm, 1 faces, 0 solids (baked)
FEATURE [Part::Revolution] Revolve141  label="plugHousing074"
  Angle = 360
  Axis = (0,1,0)
  Base = (0,0,0)
  FaceMakerClass = Part::FaceMakerBullseye
  Placement = pos=(0,0,36.15) rot=(0,0,1;0rad)
  Solid = false
  Source = -> Face132
  Symmetric = false
FEATURE [Part::MultiFuse] Fusion110  label="plugHousing076"
  Placement = pos=(0,0,0) rot=(0,0,1;1.5708rad)
  Shapes = -> [Revolve141,Revolve140]
FEATURE [Part::Feature] Face133
  shape: bbox 10 x 16.5 x 2e-07 mm, 1 faces, 0 solids (baked)
FEATURE [Part::Revolution] Revolve136  label="plugHousing069"
  Angle = 360
  Axis = (0,1,0)
  Base = (0,0,0)
  FaceMakerClass = Part::FaceMakerBullseye
  Placement = pos=(0,0,36.15) rot=(0,0,1;0rad)
  Solid = false
  Source = -> Face133
  Symmetric = false
FEATURE [Part::MultiFuse] Fusion106  label="plugHousing064"
  Placement = pos=(0,0,0) rot=(0,0,1;1.5708rad)
  Shapes = -> [Revolve138,Revolve136]
FEATURE [Part::MultiFuse] Fusion108  label="plugHousing066"
  Placement = pos=(0,19,0) rot=(0,0,1;3.14159rad)
  Shapes = -> [Fusion106,Fusion112]
FEATURE [Part::Feature] Face134
  shape: bbox 10 x 16.5 x 2e-07 mm, 1 faces, 0 solids (baked)
FEATURE [Part::Revolution] Revolve142  label="plugHousing075"
  Angle = 360
  Axis = (0,1,0)
  Base = (0,0,0)
  FaceMakerClass = Part::FaceMakerBullseye
  Placement = pos=(0,0,36.15) rot=(0,0,1;0rad)
  Solid = false
  Source = -> Face134
  Symmetric = false
FEATURE [Part::MultiFuse] Fusion107  label="plugHousing065"
  Placement = pos=(0,0,0) rot=(0,0,1;1.5708rad)
  Shapes = -> [Revolve137,Revolve142]
FEATURE [Part::MultiFuse] Fusion111  label="plugHousing077"
  Placement = pos=(0,19,0) rot=(0,0,1;3.14159rad)
  Shapes = -> [Fusion110,Fusion107]
FEATURE [Part::MultiFuse] Fusion109  label="plugHousing067"
  Placement = pos=(131.236,0,-0.15) rot=(0,0,1;0rad)
  Shapes = -> [Fusion108,Fusion111]
FEATURE [Part::MultiFuse] Fusion113  label="plugHousing079"
  Shapes = -> [Fillet043,Fusion109]
FEATURE [Part::Feature] Face135
  shape: bbox 3.5 x 17.8 x 2e-07 mm, 1 faces, 0 solids (baked)
FEATURE [Part::Revolution] Revolve143  label="removeToCreateScrewAndThreadedInsertHole049"
  Angle = 360
  Axis = (0,1,0)
  Base = (0,0,0)
  FaceMakerClass = Part::FaceMakerBullseye
  Placement = pos=(12.5,0,10) rot=(0,0,1;0rad)
  Solid = false
  Source = -> Face135
  Symmetric = false
FEATURE [Part::Feature] Face136
  shape: bbox 3.5 x 17.8 x 2e-07 mm, 1 faces, 0 solids (baked)
FEATURE [Part::Revolution] Revolve144  label="removeToCreateScrewAndThreadedInsertHole050"
  Angle = 360
  Axis = (0,1,0)
  Base = (0,0,0)
  FaceMakerClass = Part::FaceMakerBullseye
  Placement = pos=(12.5,0,62) rot=(0,0,1;0rad)
  Solid = false
  Source = -> Face136
  Symmetric = false
FEATURE [Part::Feature] Face137
  shape: bbox 3.5 x 17.8 x 2e-07 mm, 1 faces, 0 solids (baked)
FEATURE [Part::Revolution] Revolve145  label="removeToCreateScrewAndThreadedInsertHole051"
  Angle = 360
  Axis = (0,1,0)
  Base = (0,0,0)
  FaceMakerClass = Part::FaceMakerBullseye
  Placement = pos=(89.5,0,68.5) rot=(0,0,1;0rad)
  Solid = false
  Source = -> Face137
  Symmetric = false
FEATURE [Part::Feature] Face138
  shape: bbox 3.5 x 17.8 x 2e-07 mm, 1 faces, 0 solids (baked)
FEATURE [Part::Revolution] Revolve146  label="removeToCreateScrewAndThreadedInsertHole052"
  Angle = 360
  Axis = (0,1,0)
  Base = (0,0,0)
  FaceMakerClass = Part::FaceMakerBullseye
  Placement = pos=(89.5,0,3.5) rot=(0,0,1;0rad)
  Solid = false
  Source = -> Face138
  Symmetric = false
FEATURE [Part::Feature] Face139
  shape: bbox 3.5 x 17.8 x 2e-07 mm, 1 faces, 0 solids (baked)
FEATURE [Part::Revolution] Revolve147  label="removeToCreateScrewAndThreadedInsertHole053"
  Angle = 360
  Axis = (0,1,0)
  Base = (0,0,0)
  FaceMakerClass = Part::FaceMakerBullseye
  Placement = pos=(109.5,4.7,3.5) rot=(0,0,1;0rad)
  Solid = false
  Source = -> Face139
  Symmetric = false
FEATURE [Part::Feature] Face140
  shape: bbox 3.5 x 17.8 x 2e-07 mm, 1 faces, 0 solids (baked)
FEATURE [Part::Revolution] Revolve148  label="removeToCreateScrewAndThreadedInsertHole054"
  Angle = 360
  Axis = (0,1,0)
  Base = (0,0,0)
  FaceMakerClass = Part::FaceMakerBullseye
  Placement = pos=(109.5,4.7,68.5) rot=(0,0,1;0rad)
  Solid = false
  Source = -> Face140
  Symmetric = false
FEATURE [Part::MultiFuse] Fusion114  label="removeToCreateScrewAndThreadedInsertHole055"
  Shapes = -> [Revolve148,Revolve147,Revolve146,Revolve145,Revolve144,Revolve143]
FEATURE [Part::Cut] Cut047  label="casePillars004"
  Base = -> Cut037
  Tool = -> Fusion114
FEATURE [Part::Feature] Face141
  shape: bbox 3.5 x 17.8 x 2e-07 mm, 1 faces, 0 solids (baked)
FEATURE [Part::Feature] Face142
  shape: bbox 3.5 x 17.8 x 2e-07 mm, 1 faces, 0 solids (baked)
FEATURE [Part::Feature] Face143
  shape: bbox 3.5 x 17.8 x 2e-07 mm, 1 faces, 0 solids (baked)
FEATURE [Part::Revolution] Revolve149  label="removeToCreateScrewAndThreadedInsertHole057"
  Angle = 360
  Axis = (0,1,0)
  Base = (0,0,0)
  FaceMakerClass = Part::FaceMakerBullseye
  Placement = pos=(12.5,0,10) rot=(0,0,1;0rad)
  Solid = false
  Source = -> Face141
  Symmetric = false
FEATURE [Part::Feature] Face144
  shape: bbox 3.5 x 17.8 x 2e-07 mm, 1 faces, 0 solids (baked)
FEATURE [Part::Feature] Face145
  shape: bbox 3.5 x 17.8 x 2e-07 mm, 1 faces, 0 solids (baked)
FEATURE [Part::Feature] Face146
  shape: bbox 3.5 x 17.8 x 2e-07 mm, 1 faces, 0 solids (baked)
FEATURE [Part::Revolution] Revolve150  label="removeToCreateScrewAndThreadedInsertHole058"
  Angle = 360
  Axis = (0,1,0)
  Base = (0,0,0)
  FaceMakerClass = Part::FaceMakerBullseye
  Placement = pos=(12.5,0,62) rot=(0,0,1;0rad)
  Solid = false
  Source = -> Face146
  Symmetric = false
FEATURE [Part::Revolution] Revolve151  label="removeToCreateScrewAndThreadedInsertHole059"
  Angle = 360
  Axis = (0,1,0)
  Base = (0,0,0)
  FaceMakerClass = Part::FaceMakerBullseye
  Placement = pos=(89.5,0,68.5) rot=(0,0,1;0rad)
  Solid = false
  Source = -> Face143
  Symmetric = false
FEATURE [Part::Revolution] Revolve152  label="removeToCreateScrewAndThreadedInsertHole060"
  Angle = 360
  Axis = (0,1,0)
  Base = (0,0,0)
  FaceMakerClass = Part::FaceMakerBullseye
  Placement = pos=(89.5,0,3.5) rot=(0,0,1;0rad)
  Solid = false
  Source = -> Face142
  Symmetric = false
FEATURE [Part::Revolution] Revolve153  label="removeToCreateScrewAndThreadedInsertHole061"
  Angle = 360
  Axis = (0,1,0)
  Base = (0,0,0)
  FaceMakerClass = Part::FaceMakerBullseye
  Placement = pos=(109.5,4.7,3.5) rot=(0,0,1;0rad)
  Solid = false
  Source = -> Face145
  Symmetric = false
FEATURE [Part::Revolution] Revolve154  label="removeToCreateScrewAndThreadedInsertHole062"
  Angle = 360
  Axis = (0,1,0)
  Base = (0,0,0)
  FaceMakerClass = Part::FaceMakerBullseye
  Placement = pos=(109.5,4.7,68.5) rot=(0,0,1;0rad)
  Solid = false
  Source = -> Face144
  Symmetric = false
FEATURE [Part::MultiFuse] Fusion115  label="removeToCreateScrewAndThreadedInsertHole056"
  Shapes = -> [Revolve154,Revolve153,Revolve152,Revolve151,Revolve150,Revolve149]
FEATURE [Part::Feature] Face147
  shape: bbox 9.8 x 26.5 x 2e-07 mm, 1 faces, 0 solids (baked)
FEATURE [Part::Revolution] Revolve155
  Angle = 360
  Axis = (0,1,0)
  Base = (0,0,0)
  FaceMakerClass = Part::FaceMakerBullseye
  Placement = pos=(0,0,0) rot=(0,0,1;1.5708rad)
  Solid = false
  Source = -> Face147
  Symmetric = false
FEATURE [Part::Feature] Face148
  shape: bbox 9.8 x 26.5 x 2e-07 mm, 1 faces, 0 solids (baked)
FEATURE [Part::Revolution] Revolve156
  Angle = 360
  Axis = (0,1,0)
  Base = (0,0,0)
  FaceMakerClass = Part::FaceMakerBullseye
  Placement = pos=(0,0,0) rot=(0,0,1;1.5708rad)
  Solid = false
  Source = -> Face148
  Symmetric = false
FEATURE [Part::MultiFuse] Fusion116
  Placement = pos=(-18,19,36) rot=(0,0,1;0rad)
  Shapes = -> [Revolve156,Revolve155]
FEATURE [Part::Box] Box029  label="Cube016"
  AttacherType = Attacher::AttachEngine3D
  Height = 28
  Length = 3
  Placement = pos=(110.7,19,22) rot=(0,0,1;0rad)
  Width = 15.7
FEATURE [Part::Cylinder] Cylinder046
  Angle = 360
  AttacherType = Attacher::AttachEngine3D
  Height = 10
  Placement = pos=(0,0,36.15) rot=(0,0,1;0rad)
  Radius = 4
FEATURE [Part::Cylinder] Cylinder047
  Angle = 360
  AttacherType = Attacher::AttachEngine3D
  Height = 20
  Placement = pos=(0,0,36.15) rot=(0,0,1;0rad)
  Radius = 10.3
FEATURE [Part::MultiFuse] Fusion117  label="removeToCreteHoleForPlugHousing041"
  Placement = pos=(70,19,36) rot=(0,1,0;1.5708rad)
  Shapes = -> [Cylinder047,Cylinder046]
FEATURE [Part::Cut] Cut049  label="plugHousingTab004"
  Base = -> Box029
  Placement = pos=(-107.4,-14,0) rot=(0,0,1;0rad)
  Tool = -> Fusion117
FEATURE [Part::Box] Box030  label="Cube017"
  AttacherType = Attacher::AttachEngine3D
  Height = 28
  Length = 3
  Placement = pos=(110.7,19,22) rot=(0,0,1;0rad)
  Width = 15.7
FEATURE [Part::Cylinder] Cylinder048
  Angle = 360
  AttacherType = Attacher::AttachEngine3D
  Height = 10
  Placement = pos=(0,0,36.15) rot=(0,0,1;0rad)
  Radius = 4
FEATURE [Part::Cylinder] Cylinder049
  Angle = 360
  AttacherType = Attacher::AttachEngine3D
  Height = 20
  Placement = pos=(0,0,36.15) rot=(0,0,1;0rad)
  Radius = 10.3
FEATURE [Part::MultiFuse] Fusion118  label="removeToCreteHoleForPlugHousing042"
  Placement = pos=(70,19,36) rot=(0,1,0;1.5708rad)
  Shapes = -> [Cylinder049,Cylinder048]
FEATURE [Part::Cut] Cut050  label="plugHousingTab005"
  Base = -> Box030
  Placement = pos=(-107.4,-14,0) rot=(0,0,1;0rad)
  Tool = -> Fusion118
FEATURE [Part::MultiFuse] Fusion119
  Placement = pos=(9.6,23,0) rot=(0,0,1;3.14159rad)
  Shapes = -> [Cut049,Cut050]
FEATURE [Part::Box] Box031  label="Cube018"
  AttacherType = Attacher::AttachEngine3D
  Height = 10
  Length = 3
  Placement = pos=(3.3,4,12) rot=(0,0,1;0rad)
  Width = 10
FEATURE [Part::Fillet] Fillet044
  Base = -> Box031
  Edges = 1 edges r=2: [Edge11]
FEATURE [Part::Box] Box032  label="Cube019"
  AttacherType = Attacher::AttachEngine3D
  Height = 10
  Length = 3
  Placement = pos=(3.3,4,50) rot=(0,0,1;0rad)
  Width = 10
FEATURE [Part::Fillet] Fillet045
  Base = -> Box032
  Edges = 1 edges r=2: [Edge12]
FEATURE [Part::Box] Box033  label="Cube020"
  AttacherType = Attacher::AttachEngine3D
  Height = 28
  Length = 4
  Placement = pos=(5,0,22) rot=(0,0,1;0rad)
  Width = 10
FEATURE [Part::Fillet] Fillet046
  Base = -> Box033
  Edges = 1 edges r=1: [Edge7]
FEATURE [Part::Fillet] Fillet047
  Base = -> Fillet046
  Edges = 1 edges r=2: [Edge5]
FEATURE [Part::Fillet] Fillet048
  Base = -> Fillet047
  Edges = 1 edges r=2: [Edge2]
FEATURE [Part::Cylinder] Cylinder050
  Angle = 360
  AttacherType = Attacher::AttachEngine3D
  Height = 20
  Placement = pos=(0,0,36.15) rot=(0,0,1;0rad)
  Radius = 8.2
FEATURE [Part::Cylinder] Cylinder051
  Angle = 360
  AttacherType = Attacher::AttachEngine3D
  Height = 10
  Placement = pos=(0,0,36.15) rot=(0,0,1;0rad)
  Radius = 4
FEATURE [Part::MultiFuse] Fusion120  label="removeToCreteHoleForPlugHousing043"
  Placement = pos=(-42,19,36) rot=(0,1,0;1.5708rad)
  Shapes = -> [Cylinder050,Cylinder051]
FEATURE [Sketcher::SketchObject] Sketch067  label="topSketch018"
  FullyConstrained = true
  sketch-geometry (4):
    g0: LineSegment StartX=16.8446 StartY=31.512 StartZ=0 EndX=16.3251 EndY=34.4666 EndZ=0
    g1: ArcOfCircle CenterX=19 CenterY=19.2524 CenterZ=0 NormalX=0 NormalY=0 NormalZ=1 AngleXU=0 Radius=15.4476 StartAngle=1.74483 EndAngle=2.72717
    g2: ArcOfCircle CenterX=19 CenterY=19.2524 CenterZ=0 NormalX=0 NormalY=0 NormalZ=1 AngleXU=0 Radius=12.4476 StartAngle=1.74483 EndAngle=2.73189
    g3: LineSegment StartX=4.86004 StartY=25.4725 StartZ=0 EndX=7.58253 EndY=24.2107 EndZ=0
  constraints (7):
    c: Block(g0)
    c: Coincident(g1,g0)
    c: Coincident(g2,g0)
    c: Coincident(g3,g1)
    c: Coincident(g3,g2)
    c: Block(g1)
    c: Block(g2)
FEATURE [Part::Extrusion] Extrude058
  Base = -> Sketch067
  Dir = (0,0,1)
  DirMode = 2
  FaceMakerClass = Part::FaceMakerBullseye
  LengthFwd = 10
  LengthRev = 0
  Placement = pos=(0,0,31) rot=(0,0,1;0rad)
  Solid = true
  Symmetric = false
FEATURE [Part::Cut] Cut051
  Base = -> Extrude058
  Tool = -> Fusion120
FEATURE [Part::Fillet] Fillet049
  Base = -> Cut051
  Edges = 1 edges r=2: [Edge1]
FEATURE [Part::Fillet] Fillet050
  Base = -> Fillet049
  Edges = 1 edges r=2.5: [Edge1]
FEATURE [Part::Fillet] Fillet051
  Base = -> Fillet050
  Edges = 1 edges r=2.5: [Edge2]
FEATURE [Part::MultiFuse] Fusion121  label="wireHolder003"
  Shapes = -> [Fusion116,Fillet051]
FEATURE [Part::MultiFuse] Fusion122
  Shapes = -> [Fillet045,Fusion121]
FEATURE [Part::MultiFuse] Fusion123  label="wireHolder004"
  Shapes = -> [Fusion122,Fillet048]
FEATURE [Part::MultiFuse] Fusion124  label="wireHolder005"
  Shapes = -> [Fillet044,Fusion119,Fusion123]
FEATURE [Part::MultiFuse] Fusion125  label="bottom012"
  Shapes = -> [Fillet037,Cut034]
FEATURE [Part::Cut] Cut052  label="bottom013"
  Base = -> Fusion125
  Tool = -> Fusion115
FEATURE [Part::MultiFuse] Fusion126  label="casePillars005"
  Shapes = -> [Fusion092,Cut047]
